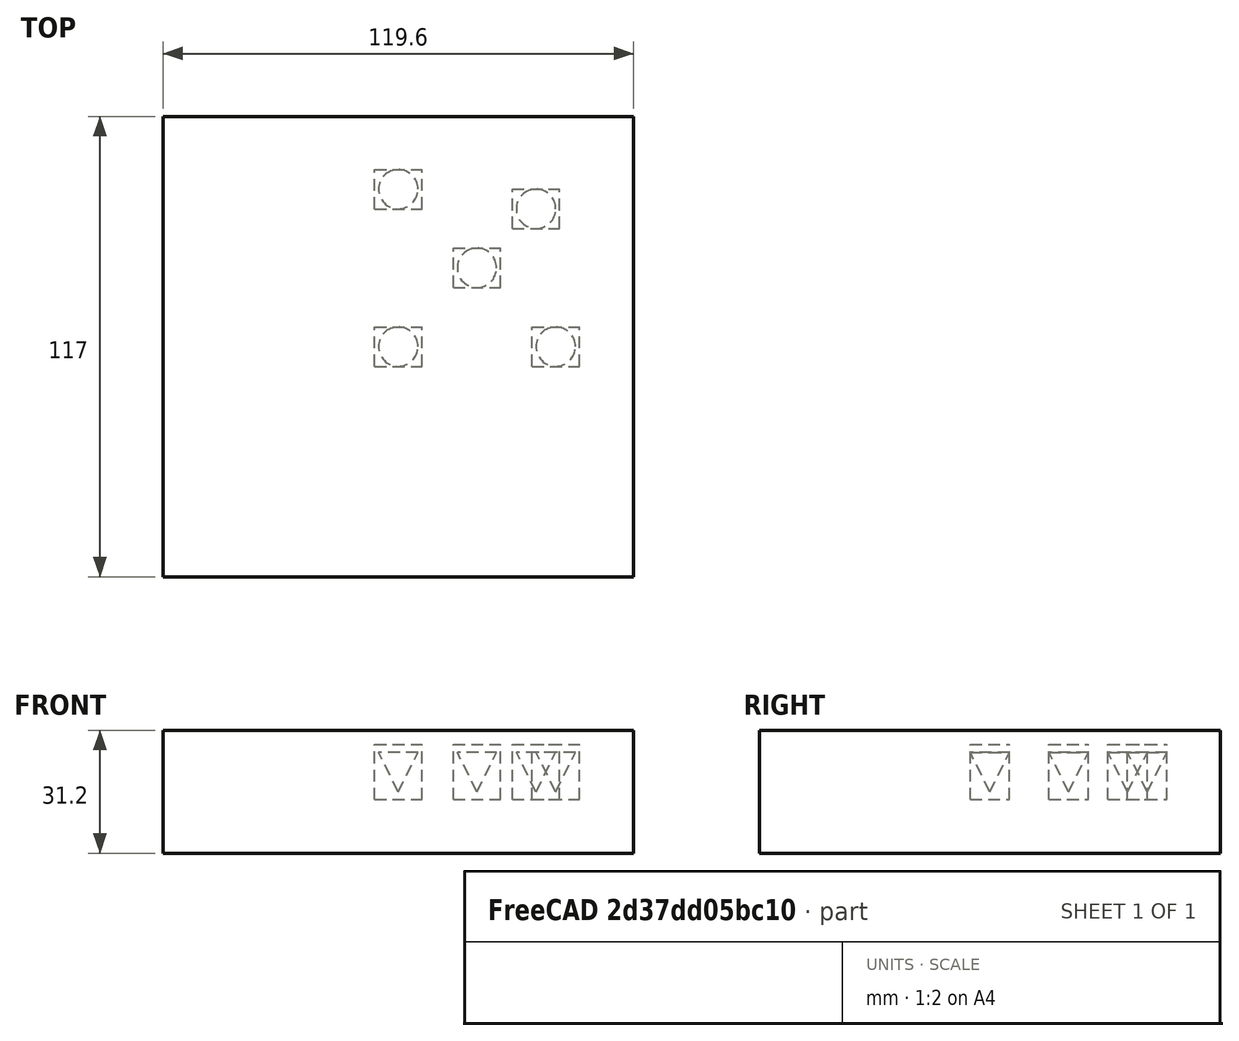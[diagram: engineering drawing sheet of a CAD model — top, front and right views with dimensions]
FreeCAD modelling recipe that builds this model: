
FCSTD DOCUMENT  (FreeCAD 0.21R33694 (Git))
Label: PointArray-of-part
License: All rights reserved
objects: App::DocumentObjectGroupPython×1251, Part::Vertex×5, App::Part×4, Part::FeaturePython×3, Part::Cone×2, Part::Compound×1
note: 11 computed .brp shape members not serialized (recipe doc carries the construction recipe); baked Part::Feature solids carry a one-line shape summary decoded from their .brp

FEATURE [App::DocumentObjectGroupPython] HALFPI  # scripted group (container) (typed FeaturePython)
  name = HALFPI
  value = pi/2.
FEATURE [App::DocumentObjectGroupPython] PI  # scripted group (container) (typed FeaturePython)
  name = PI
  value = 1.*pi
FEATURE [App::DocumentObjectGroupPython] TWOPI  # scripted group (container) (typed FeaturePython)
  name = TWOPI
  value = 2.*pi
FEATURE [App::DocumentObjectGroupPython] Constants  # scripted group (container) (typed FeaturePython)
  Group = -> [HALFPI,PI,TWOPI]
FEATURE [App::DocumentObjectGroupPython] Variables  # scripted group (container) (typed FeaturePython)
FEATURE [App::DocumentObjectGroupPython] Quantities  # scripted group (container) (typed FeaturePython)
FEATURE [App::DocumentObjectGroupPython] Isotopes  # scripted group (container) (typed FeaturePython)
FEATURE [App::DocumentObjectGroupPython] Elements  # scripted group (container) (typed FeaturePython)
FEATURE [App::DocumentObjectGroupPython] Matrix  # scripted group (container) (typed FeaturePython)
FEATURE [App::DocumentObjectGroupPython] Surfaces  # scripted group (container) (typed FeaturePython)
FEATURE [App::DocumentObjectGroupPython] Opticals  # scripted group (container) (typed FeaturePython)
  Group = -> [Matrix,Surfaces]
FEATURE [App::DocumentObjectGroupPython] G4Isotopes  # scripted group (container) (typed FeaturePython)
FEATURE [App::DocumentObjectGroupPython] H_element  # scripted group (container) (typed FeaturePython)
  Z = 1
  atom_value = 1.008
  formula = H
  name = H_element
FEATURE [App::DocumentObjectGroupPython] He_element  # scripted group (container) (typed FeaturePython)
  Z = 2
  atom_value = 4.0026
  formula = He
  name = He_element
FEATURE [App::DocumentObjectGroupPython] Li_element  # scripted group (container) (typed FeaturePython)
  Z = 3
  atom_value = 6.94
  formula = Li
  name = Li_element
FEATURE [App::DocumentObjectGroupPython] Be_element  # scripted group (container) (typed FeaturePython)
  Z = 4
  atom_value = 9.01218
  formula = Be
  name = Be_element
FEATURE [App::DocumentObjectGroupPython] B_element  # scripted group (container) (typed FeaturePython)
  Z = 5
  atom_value = 10.81
  formula = B
  name = B_element
FEATURE [App::DocumentObjectGroupPython] C_element  # scripted group (container) (typed FeaturePython)
  Z = 6
  atom_value = 12.011
  formula = C
  name = C_element
FEATURE [App::DocumentObjectGroupPython] N_element  # scripted group (container) (typed FeaturePython)
  Z = 7
  atom_value = 14.007
  formula = N
  name = N_element
FEATURE [App::DocumentObjectGroupPython] O_element  # scripted group (container) (typed FeaturePython)
  Z = 8
  atom_value = 15.999
  formula = O
  name = O_element
FEATURE [App::DocumentObjectGroupPython] F_element  # scripted group (container) (typed FeaturePython)
  Z = 9
  atom_value = 18.9984
  formula = F
  name = F_element
FEATURE [App::DocumentObjectGroupPython] Ne_element  # scripted group (container) (typed FeaturePython)
  Z = 10
  atom_value = 20.1797
  formula = Ne
  name = Ne_element
FEATURE [App::DocumentObjectGroupPython] Na_element  # scripted group (container) (typed FeaturePython)
  Z = 11
  atom_value = 22.9898
  formula = Na
  name = Na_element
FEATURE [App::DocumentObjectGroupPython] Mg_element  # scripted group (container) (typed FeaturePython)
  Z = 12
  atom_value = 24.305
  formula = Mg
  name = Mg_element
FEATURE [App::DocumentObjectGroupPython] Al_element  # scripted group (container) (typed FeaturePython)
  Z = 13
  atom_value = 26.9815
  formula = Al
  name = Al_element
FEATURE [App::DocumentObjectGroupPython] Si_element  # scripted group (container) (typed FeaturePython)
  Z = 14
  atom_value = 28.085
  formula = Si
  name = Si_element
FEATURE [App::DocumentObjectGroupPython] P_element  # scripted group (container) (typed FeaturePython)
  Z = 15
  atom_value = 30.9738
  formula = P
  name = P_element
FEATURE [App::DocumentObjectGroupPython] S_element  # scripted group (container) (typed FeaturePython)
  Z = 16
  atom_value = 32.06
  formula = S
  name = S_element
FEATURE [App::DocumentObjectGroupPython] Cl_element  # scripted group (container) (typed FeaturePython)
  Z = 17
  atom_value = 35.45
  formula = Cl
  name = Cl_element
FEATURE [App::DocumentObjectGroupPython] Ar_element  # scripted group (container) (typed FeaturePython)
  Z = 18
  atom_value = 39.95
  formula = Ar
  name = Ar_element
FEATURE [App::DocumentObjectGroupPython] K_element  # scripted group (container) (typed FeaturePython)
  Z = 19
  atom_value = 39.0983
  formula = K
  name = K_element
FEATURE [App::DocumentObjectGroupPython] Ca_element  # scripted group (container) (typed FeaturePython)
  Z = 20
  atom_value = 40.078
  formula = Ca
  name = Ca_element
FEATURE [App::DocumentObjectGroupPython] Sc_element  # scripted group (container) (typed FeaturePython)
  Z = 21
  atom_value = 44.9559
  formula = Sc
  name = Sc_element
FEATURE [App::DocumentObjectGroupPython] Ti_element  # scripted group (container) (typed FeaturePython)
  Z = 22
  atom_value = 47.867
  formula = Ti
  name = Ti_element
FEATURE [App::DocumentObjectGroupPython] V_element  # scripted group (container) (typed FeaturePython)
  Z = 23
  atom_value = 50.9415
  formula = V
  name = V_element
FEATURE [App::DocumentObjectGroupPython] Cr_element  # scripted group (container) (typed FeaturePython)
  Z = 24
  atom_value = 51.9961
  formula = Cr
  name = Cr_element
FEATURE [App::DocumentObjectGroupPython] Mn_element  # scripted group (container) (typed FeaturePython)
  Z = 25
  atom_value = 54.938
  formula = Mn
  name = Mn_element
FEATURE [App::DocumentObjectGroupPython] Fe_element  # scripted group (container) (typed FeaturePython)
  Z = 26
  atom_value = 55.845
  formula = Fe
  name = Fe_element
FEATURE [App::DocumentObjectGroupPython] Co_element  # scripted group (container) (typed FeaturePython)
  Z = 27
  atom_value = 58.9332
  formula = Co
  name = Co_element
FEATURE [App::DocumentObjectGroupPython] Ni_element  # scripted group (container) (typed FeaturePython)
  Z = 28
  atom_value = 58.6934
  formula = Ni
  name = Ni_element
FEATURE [App::DocumentObjectGroupPython] Cu_element  # scripted group (container) (typed FeaturePython)
  Z = 29
  atom_value = 63.546
  formula = Cu
  name = Cu_element
FEATURE [App::DocumentObjectGroupPython] Zn_element  # scripted group (container) (typed FeaturePython)
  Z = 30
  atom_value = 65.38
  formula = Zn
  name = Zn_element
FEATURE [App::DocumentObjectGroupPython] Ga_element  # scripted group (container) (typed FeaturePython)
  Z = 31
  atom_value = 69.723
  formula = Ga
  name = Ga_element
FEATURE [App::DocumentObjectGroupPython] Ge_element  # scripted group (container) (typed FeaturePython)
  Z = 32
  atom_value = 72.63
  formula = Ge
  name = Ge_element
FEATURE [App::DocumentObjectGroupPython] As_element  # scripted group (container) (typed FeaturePython)
  Z = 33
  atom_value = 74.9216
  formula = As
  name = As_element
FEATURE [App::DocumentObjectGroupPython] Se_element  # scripted group (container) (typed FeaturePython)
  Z = 34
  atom_value = 78.971
  formula = Se
  name = Se_element
FEATURE [App::DocumentObjectGroupPython] Br_element  # scripted group (container) (typed FeaturePython)
  Z = 35
  atom_value = 79.904
  formula = Br
  name = Br_element
FEATURE [App::DocumentObjectGroupPython] Kr_element  # scripted group (container) (typed FeaturePython)
  Z = 36
  atom_value = 83.798
  formula = Kr
  name = Kr_element
FEATURE [App::DocumentObjectGroupPython] Rb_element  # scripted group (container) (typed FeaturePython)
  Z = 37
  atom_value = 85.4678
  formula = Rb
  name = Rb_element
FEATURE [App::DocumentObjectGroupPython] Sr_element  # scripted group (container) (typed FeaturePython)
  Z = 38
  atom_value = 87.62
  formula = Sr
  name = Sr_element
FEATURE [App::DocumentObjectGroupPython] Y_element  # scripted group (container) (typed FeaturePython)
  Z = 39
  atom_value = 88.9058
  formula = Y
  name = Y_element
FEATURE [App::DocumentObjectGroupPython] Zr_element  # scripted group (container) (typed FeaturePython)
  Z = 40
  atom_value = 91.224
  formula = Zr
  name = Zr_element
FEATURE [App::DocumentObjectGroupPython] Nb_element  # scripted group (container) (typed FeaturePython)
  Z = 41
  atom_value = 92.9064
  formula = Nb
  name = Nb_element
FEATURE [App::DocumentObjectGroupPython] Mo_element  # scripted group (container) (typed FeaturePython)
  Z = 42
  atom_value = 95.95
  formula = Mo
  name = Mo_element
FEATURE [App::DocumentObjectGroupPython] Tc_element  # scripted group (container) (typed FeaturePython)
  Z = 43
  atom_value = 97
  formula = Tc
  name = Tc_element
FEATURE [App::DocumentObjectGroupPython] Ru_element  # scripted group (container) (typed FeaturePython)
  Z = 44
  atom_value = 101.07
  formula = Ru
  name = Ru_element
FEATURE [App::DocumentObjectGroupPython] Rh_element  # scripted group (container) (typed FeaturePython)
  Z = 45
  atom_value = 102.905
  formula = Rh
  name = Rh_element
FEATURE [App::DocumentObjectGroupPython] Pd_element  # scripted group (container) (typed FeaturePython)
  Z = 46
  atom_value = 106.42
  formula = Pd
  name = Pd_element
FEATURE [App::DocumentObjectGroupPython] Ag_element  # scripted group (container) (typed FeaturePython)
  Z = 47
  atom_value = 107.868
  formula = Ag
  name = Ag_element
FEATURE [App::DocumentObjectGroupPython] Cd_element  # scripted group (container) (typed FeaturePython)
  Z = 48
  atom_value = 112.414
  formula = Cd
  name = Cd_element
FEATURE [App::DocumentObjectGroupPython] In_element  # scripted group (container) (typed FeaturePython)
  Z = 49
  atom_value = 114.818
  formula = In
  name = In_element
FEATURE [App::DocumentObjectGroupPython] Sn_element  # scripted group (container) (typed FeaturePython)
  Z = 50
  atom_value = 118.71
  formula = Sn
  name = Sn_element
FEATURE [App::DocumentObjectGroupPython] Sb_element  # scripted group (container) (typed FeaturePython)
  Z = 51
  atom_value = 121.76
  formula = Sb
  name = Sb_element
FEATURE [App::DocumentObjectGroupPython] Te_element  # scripted group (container) (typed FeaturePython)
  Z = 52
  atom_value = 127.6
  formula = Te
  name = Te_element
FEATURE [App::DocumentObjectGroupPython] I_element  # scripted group (container) (typed FeaturePython)
  Z = 53
  atom_value = 126.904
  formula = I
  name = I_element
FEATURE [App::DocumentObjectGroupPython] Xe_element  # scripted group (container) (typed FeaturePython)
  Z = 54
  atom_value = 131.293
  formula = Xe
  name = Xe_element
FEATURE [App::DocumentObjectGroupPython] Cs_element  # scripted group (container) (typed FeaturePython)
  Z = 55
  atom_value = 132.905
  formula = Cs
  name = Cs_element
FEATURE [App::DocumentObjectGroupPython] Ba_element  # scripted group (container) (typed FeaturePython)
  Z = 56
  atom_value = 137.327
  formula = Ba
  name = Ba_element
FEATURE [App::DocumentObjectGroupPython] La_element  # scripted group (container) (typed FeaturePython)
  Z = 57
  atom_value = 138.905
  formula = La
  name = La_element
FEATURE [App::DocumentObjectGroupPython] Ce_element  # scripted group (container) (typed FeaturePython)
  Z = 58
  atom_value = 140.116
  formula = Ce
  name = Ce_element
FEATURE [App::DocumentObjectGroupPython] Pr_element  # scripted group (container) (typed FeaturePython)
  Z = 59
  atom_value = 140.908
  formula = Pr
  name = Pr_element
FEATURE [App::DocumentObjectGroupPython] Nd_element  # scripted group (container) (typed FeaturePython)
  Z = 60
  atom_value = 144.242
  formula = Nd
  name = Nd_element
FEATURE [App::DocumentObjectGroupPython] Pm_element  # scripted group (container) (typed FeaturePython)
  Z = 61
  atom_value = 145
  formula = Pm
  name = Pm_element
FEATURE [App::DocumentObjectGroupPython] Sm_element  # scripted group (container) (typed FeaturePython)
  Z = 62
  atom_value = 150.36
  formula = Sm
  name = Sm_element
FEATURE [App::DocumentObjectGroupPython] Eu_element  # scripted group (container) (typed FeaturePython)
  Z = 63
  atom_value = 151.964
  formula = Eu
  name = Eu_element
FEATURE [App::DocumentObjectGroupPython] Gd_element  # scripted group (container) (typed FeaturePython)
  Z = 64
  atom_value = 157.25
  formula = Gd
  name = Gd_element
FEATURE [App::DocumentObjectGroupPython] Tb_element  # scripted group (container) (typed FeaturePython)
  Z = 65
  atom_value = 158.925
  formula = Tb
  name = Tb_element
FEATURE [App::DocumentObjectGroupPython] Dy_element  # scripted group (container) (typed FeaturePython)
  Z = 66
  atom_value = 162.5
  formula = Dy
  name = Dy_element
FEATURE [App::DocumentObjectGroupPython] Ho_element  # scripted group (container) (typed FeaturePython)
  Z = 67
  atom_value = 164.93
  formula = Ho
  name = Ho_element
FEATURE [App::DocumentObjectGroupPython] Er_element  # scripted group (container) (typed FeaturePython)
  Z = 68
  atom_value = 167.259
  formula = Er
  name = Er_element
FEATURE [App::DocumentObjectGroupPython] Tm_element  # scripted group (container) (typed FeaturePython)
  Z = 69
  atom_value = 168.934
  formula = Tm
  name = Tm_element
FEATURE [App::DocumentObjectGroupPython] Yb_element  # scripted group (container) (typed FeaturePython)
  Z = 70
  atom_value = 173.045
  formula = Yb
  name = Yb_element
FEATURE [App::DocumentObjectGroupPython] Lu_element  # scripted group (container) (typed FeaturePython)
  Z = 71
  atom_value = 174.967
  formula = Lu
  name = Lu_element
FEATURE [App::DocumentObjectGroupPython] Hf_element  # scripted group (container) (typed FeaturePython)
  Z = 72
  atom_value = 178.49
  formula = Hf
  name = Hf_element
FEATURE [App::DocumentObjectGroupPython] Ta_element  # scripted group (container) (typed FeaturePython)
  Z = 73
  atom_value = 180.948
  formula = Ta
  name = Ta_element
FEATURE [App::DocumentObjectGroupPython] W_element  # scripted group (container) (typed FeaturePython)
  Z = 74
  atom_value = 183.84
  formula = W
  name = W_element
FEATURE [App::DocumentObjectGroupPython] Re_element  # scripted group (container) (typed FeaturePython)
  Z = 75
  atom_value = 186.207
  formula = Re
  name = Re_element
FEATURE [App::DocumentObjectGroupPython] Os_element  # scripted group (container) (typed FeaturePython)
  Z = 76
  atom_value = 190.23
  formula = Os
  name = Os_element
FEATURE [App::DocumentObjectGroupPython] Ir_element  # scripted group (container) (typed FeaturePython)
  Z = 77
  atom_value = 192.217
  formula = Ir
  name = Ir_element
FEATURE [App::DocumentObjectGroupPython] Pt_element  # scripted group (container) (typed FeaturePython)
  Z = 78
  atom_value = 195.084
  formula = Pt
  name = Pt_element
FEATURE [App::DocumentObjectGroupPython] Au_element  # scripted group (container) (typed FeaturePython)
  Z = 79
  atom_value = 196.967
  formula = Au
  name = Au_element
FEATURE [App::DocumentObjectGroupPython] Hg_element  # scripted group (container) (typed FeaturePython)
  Z = 80
  atom_value = 200.592
  formula = Hg
  name = Hg_element
FEATURE [App::DocumentObjectGroupPython] Tl_element  # scripted group (container) (typed FeaturePython)
  Z = 81
  atom_value = 204.38
  formula = Tl
  name = Tl_element
FEATURE [App::DocumentObjectGroupPython] Pb_element  # scripted group (container) (typed FeaturePython)
  Z = 82
  atom_value = 207.2
  formula = Pb
  name = Pb_element
FEATURE [App::DocumentObjectGroupPython] Bi_element  # scripted group (container) (typed FeaturePython)
  Z = 83
  atom_value = 208.98
  formula = Bi
  name = Bi_element
FEATURE [App::DocumentObjectGroupPython] Po_element  # scripted group (container) (typed FeaturePython)
  Z = 84
  atom_value = 209
  formula = Po
  name = Po_element
FEATURE [App::DocumentObjectGroupPython] At_element  # scripted group (container) (typed FeaturePython)
  Z = 85
  atom_value = 210
  formula = At
  name = At_element
FEATURE [App::DocumentObjectGroupPython] Rn_element  # scripted group (container) (typed FeaturePython)
  Z = 86
  atom_value = 222
  formula = Rn
  name = Rn_element
FEATURE [App::DocumentObjectGroupPython] Fr_element  # scripted group (container) (typed FeaturePython)
  Z = 87
  atom_value = 223
  formula = Fr
  name = Fr_element
FEATURE [App::DocumentObjectGroupPython] Ra_element  # scripted group (container) (typed FeaturePython)
  Z = 88
  atom_value = 226
  formula = Ra
  name = Ra_element
FEATURE [App::DocumentObjectGroupPython] Ac_element  # scripted group (container) (typed FeaturePython)
  Z = 89
  atom_value = 227
  formula = Ac
  name = Ac_element
FEATURE [App::DocumentObjectGroupPython] Th_element  # scripted group (container) (typed FeaturePython)
  Z = 90
  atom_value = 232.038
  formula = Th
  name = Th_element
FEATURE [App::DocumentObjectGroupPython] Pa_element  # scripted group (container) (typed FeaturePython)
  Z = 91
  atom_value = 231.036
  formula = Pa
  name = Pa_element
FEATURE [App::DocumentObjectGroupPython] U_element  # scripted group (container) (typed FeaturePython)
  Z = 92
  atom_value = 238.029
  formula = U
  name = U_element
FEATURE [App::DocumentObjectGroupPython] Np_element  # scripted group (container) (typed FeaturePython)
  Z = 93
  atom_value = 237
  formula = Np
  name = Np_element
FEATURE [App::DocumentObjectGroupPython] Pu_element  # scripted group (container) (typed FeaturePython)
  Z = 94
  atom_value = 244
  formula = Pu
  name = Pu_element
FEATURE [App::DocumentObjectGroupPython] Am_element  # scripted group (container) (typed FeaturePython)
  Z = 95
  atom_value = 243
  formula = Am
  name = Am_element
FEATURE [App::DocumentObjectGroupPython] Cm_element  # scripted group (container) (typed FeaturePython)
  Z = 96
  atom_value = 247
  formula = Cm
  name = Cm_element
FEATURE [App::DocumentObjectGroupPython] Bk_element  # scripted group (container) (typed FeaturePython)
  Z = 97
  atom_value = 247
  formula = Bk
  name = Bk_element
FEATURE [App::DocumentObjectGroupPython] Cf_element  # scripted group (container) (typed FeaturePython)
  Z = 98
  atom_value = 251
  formula = Cf
  name = Cf_element
FEATURE [App::DocumentObjectGroupPython] G4Elements  # scripted group (container) (typed FeaturePython)
  Group = -> [H_element,He_element,Li_element,Be_element,B_element,C_element,N_element,O_element,F_element,Ne_element,Na_element,Mg_element,Al_element,Si_element,P_element,S_element,Cl_element,Ar_element,K_element,Ca_element,Sc_element,Ti_element,V_element,Cr_element,Mn_element,Fe_element,Co_element,Ni_element,Cu_element,Zn_element,Ga_element,Ge_element,As_element,Se_element,Br_element,Kr_element,Rb_element,+61 more]
FEATURE [App::DocumentObjectGroupPython] H_element001  label="H_element : 0.101"  # scripted group (container) (typed FeaturePython)
  n = 0.101327
FEATURE [App::DocumentObjectGroupPython] C_element001  label="C_element : 0.775"  # scripted group (container) (typed FeaturePython)
  n = 0.7755
FEATURE [App::DocumentObjectGroupPython] N_element001  label="N_element : 0.035"  # scripted group (container) (typed FeaturePython)
  n = 0.035057
FEATURE [App::DocumentObjectGroupPython] O_element001  label="O_element : 0.052"  # scripted group (container) (typed FeaturePython)
  n = 0.0523159
FEATURE [App::DocumentObjectGroupPython] F_element001  label="F_element : 0.017"  # scripted group (container) (typed FeaturePython)
  n = 0.017422
FEATURE [App::DocumentObjectGroupPython] Ca_element001  label="Ca_element : 0.018"  # scripted group (container) (typed FeaturePython)
  n = 0.018378
FEATURE [App::DocumentObjectGroupPython] G4_A_150_TISSUE  label="G4_A-150_TISSUE"  # scripted group (container) (typed FeaturePython)
  Dunit = g/cm3
  Dvalue = 1.127
  Group = -> [H_element001,C_element001,N_element001,O_element001,F_element001,Ca_element001]
  conduct = 2
  density = 1
  expand = 3
  formula = G4_A-150_TISSUE
  name = G4_A-150_TISSUE
  specific = 4
FEATURE [App::DocumentObjectGroupPython] C_element002  label="C_element : 3"  # scripted group (container) (typed FeaturePython)
  n = 3
  ref = C_element
FEATURE [App::DocumentObjectGroupPython] H_element002  label="H_element : 6"  # scripted group (container) (typed FeaturePython)
  n = 6
  ref = H_element
FEATURE [App::DocumentObjectGroupPython] O_element002  label="O_element : 1"  # scripted group (container) (typed FeaturePython)
  n = 1
  ref = O_element
FEATURE [App::DocumentObjectGroupPython] G4_ACETONE  # scripted group (container) (typed FeaturePython)
  Dunit = g/cm3
  Dvalue = 0.7899
  Group = -> [C_element002,H_element002,O_element002]
  conduct = 2
  density = 1
  expand = 3
  formula = G4_ACETONE
  name = G4_ACETONE
  specific = 4
FEATURE [App::DocumentObjectGroupPython] C_element003  label="C_element : 2"  # scripted group (container) (typed FeaturePython)
  n = 2
  ref = C_element
FEATURE [App::DocumentObjectGroupPython] H_element003  label="H_element : 2"  # scripted group (container) (typed FeaturePython)
  n = 2
  ref = H_element
FEATURE [App::DocumentObjectGroupPython] G4_ACETYLENE  # scripted group (container) (typed FeaturePython)
  Dunit = g/cm3
  Dvalue = 0.0010967
  Group = -> [C_element003,H_element003]
  conduct = 2
  density = 1
  expand = 3
  formula = G4_ACETYLENE
  name = G4_ACETYLENE
  specific = 4
FEATURE [App::DocumentObjectGroupPython] C_element004  label="C_element : 5"  # scripted group (container) (typed FeaturePython)
  n = 5
  ref = C_element
FEATURE [App::DocumentObjectGroupPython] H_element004  label="H_element : 5"  # scripted group (container) (typed FeaturePython)
  n = 5
  ref = H_element
FEATURE [App::DocumentObjectGroupPython] N_element002  label="N_element : 5"  # scripted group (container) (typed FeaturePython)
  n = 5
  ref = N_element
FEATURE [App::DocumentObjectGroupPython] G4_ADENINE  # scripted group (container) (typed FeaturePython)
  Dunit = g/cm3
  Dvalue = 1.6
  Group = -> [C_element004,H_element004,N_element002]
  conduct = 2
  density = 1
  expand = 3
  formula = G4_ADENINE
  name = G4_ADENINE
  specific = 4
FEATURE [App::DocumentObjectGroupPython] H_element005  label="H_element : 0.114"  # scripted group (container) (typed FeaturePython)
  n = 0.114
FEATURE [App::DocumentObjectGroupPython] C_element005  label="C_element : 0.598"  # scripted group (container) (typed FeaturePython)
  n = 0.598
FEATURE [App::DocumentObjectGroupPython] N_element003  label="N_element : 0.007"  # scripted group (container) (typed FeaturePython)
  n = 0.007
FEATURE [App::DocumentObjectGroupPython] O_element003  label="O_element : 0.278"  # scripted group (container) (typed FeaturePython)
  n = 0.278
FEATURE [App::DocumentObjectGroupPython] Na_element001  label="Na_element : 0.001"  # scripted group (container) (typed FeaturePython)
  n = 0.001
FEATURE [App::DocumentObjectGroupPython] S_element001  label="S_element : 0.001"  # scripted group (container) (typed FeaturePython)
  n = 0.001
FEATURE [App::DocumentObjectGroupPython] Cl_element001  label="Cl_element : 0.001"  # scripted group (container) (typed FeaturePython)
  n = 0.001
FEATURE [App::DocumentObjectGroupPython] G4_ADIPOSE_TISSUE_ICRP  # scripted group (container) (typed FeaturePython)
  Dunit = g/cm3
  Dvalue = 0.95
  Group = -> [H_element005,C_element005,N_element003,O_element003,Na_element001,S_element001,Cl_element001]
  conduct = 2
  density = 1
  expand = 3
  formula = G4_ADIPOSE_TISSUE_ICRP
  name = G4_ADIPOSE_TISSUE_ICRP
  specific = 4
FEATURE [App::DocumentObjectGroupPython] C_element006  label="C_element : 0.000"  # scripted group (container) (typed FeaturePython)
  n = 0.000124
FEATURE [App::DocumentObjectGroupPython] N_element004  label="N_element : 0.755"  # scripted group (container) (typed FeaturePython)
  n = 0.755268
FEATURE [App::DocumentObjectGroupPython] O_element004  label="O_element : 0.232"  # scripted group (container) (typed FeaturePython)
  n = 0.231781
FEATURE [App::DocumentObjectGroupPython] Ar_element001  label="Ar_element : 0.013"  # scripted group (container) (typed FeaturePython)
  n = 0.012827
FEATURE [App::DocumentObjectGroupPython] G4_AIR  # scripted group (container) (typed FeaturePython)
  Dunit = g/cm3
  Dvalue = 0.00120479
  Group = -> [C_element006,N_element004,O_element004,Ar_element001]
  conduct = 2
  density = 1
  expand = 3
  formula = G4_AIR
  name = G4_AIR
  specific = 4
FEATURE [App::DocumentObjectGroupPython] C_element007  label="C_element : 006"  # scripted group (container) (typed FeaturePython)
  n = 3
  ref = C_element
FEATURE [App::DocumentObjectGroupPython] H_element006  label="H_element : 7"  # scripted group (container) (typed FeaturePython)
  n = 7
  ref = H_element
FEATURE [App::DocumentObjectGroupPython] N_element005  label="N_element : 1"  # scripted group (container) (typed FeaturePython)
  n = 1
  ref = N_element
FEATURE [App::DocumentObjectGroupPython] O_element005  label="O_element : 2"  # scripted group (container) (typed FeaturePython)
  n = 2
  ref = O_element
FEATURE [App::DocumentObjectGroupPython] G4_ALANINE  # scripted group (container) (typed FeaturePython)
  Dunit = g/cm3
  Dvalue = 1.42
  Group = -> [C_element007,H_element006,N_element005,O_element005]
  conduct = 2
  density = 1
  expand = 3
  formula = G4_ALANINE
  name = G4_ALANINE
  specific = 4
FEATURE [App::DocumentObjectGroupPython] Al_element001  label="Al_element : 2"  # scripted group (container) (typed FeaturePython)
  n = 2
  ref = Al_element
FEATURE [App::DocumentObjectGroupPython] O_element006  label="O_element : 3"  # scripted group (container) (typed FeaturePython)
  n = 3
  ref = O_element
FEATURE [App::DocumentObjectGroupPython] G4_ALUMINUM_OXIDE  # scripted group (container) (typed FeaturePython)
  Dunit = g/cm3
  Dvalue = 3.97
  Group = -> [Al_element001,O_element006]
  conduct = 2
  density = 1
  expand = 3
  formula = G4_ALUMINUM_OXIDE
  name = G4_ALUMINUM_OXIDE
  specific = 4
FEATURE [App::DocumentObjectGroupPython] H_element007  label="H_element : 0.106"  # scripted group (container) (typed FeaturePython)
  n = 0.10593
FEATURE [App::DocumentObjectGroupPython] C_element008  label="C_element : 0.789"  # scripted group (container) (typed FeaturePython)
  n = 0.788974
FEATURE [App::DocumentObjectGroupPython] O_element007  label="O_element : 0.105"  # scripted group (container) (typed FeaturePython)
  n = 0.105096
FEATURE [App::DocumentObjectGroupPython] G4_AMBER  # scripted group (container) (typed FeaturePython)
  Dunit = g/cm3
  Dvalue = 1.1
  Group = -> [H_element007,C_element008,O_element007]
  conduct = 2
  density = 1
  expand = 3
  formula = G4_AMBER
  name = G4_AMBER
  specific = 4
FEATURE [App::DocumentObjectGroupPython] N_element006  label="N_element : 006"  # scripted group (container) (typed FeaturePython)
  n = 1
  ref = N_element
FEATURE [App::DocumentObjectGroupPython] H_element008  label="H_element : 3"  # scripted group (container) (typed FeaturePython)
  n = 3
  ref = H_element
FEATURE [App::DocumentObjectGroupPython] G4_AMMONIA  # scripted group (container) (typed FeaturePython)
  Dunit = g/cm3
  Dvalue = 0.000826019
  Group = -> [N_element006,H_element008]
  conduct = 2
  density = 1
  expand = 3
  formula = G4_AMMONIA
  name = G4_AMMONIA
  specific = 4
FEATURE [App::DocumentObjectGroupPython] C_element009  label="C_element : 6"  # scripted group (container) (typed FeaturePython)
  n = 6
  ref = C_element
FEATURE [App::DocumentObjectGroupPython] H_element009  label="H_element : 008"  # scripted group (container) (typed FeaturePython)
  n = 7
  ref = H_element
FEATURE [App::DocumentObjectGroupPython] N_element007  label="N_element : 007"  # scripted group (container) (typed FeaturePython)
  n = 1
  ref = N_element
FEATURE [App::DocumentObjectGroupPython] G4_ANILINE  # scripted group (container) (typed FeaturePython)
  Dunit = g/cm3
  Dvalue = 1.0235
  Group = -> [C_element009,H_element009,N_element007]
  conduct = 2
  density = 1
  expand = 3
  formula = G4_ANILINE
  name = G4_ANILINE
  specific = 4
FEATURE [App::DocumentObjectGroupPython] C_element010  label="C_element : 14"  # scripted group (container) (typed FeaturePython)
  n = 14
  ref = C_element
FEATURE [App::DocumentObjectGroupPython] H_element010  label="H_element : 10"  # scripted group (container) (typed FeaturePython)
  n = 10
  ref = H_element
FEATURE [App::DocumentObjectGroupPython] G4_ANTHRACENE  # scripted group (container) (typed FeaturePython)
  Dunit = g/cm3
  Dvalue = 1.283
  Group = -> [C_element010,H_element010]
  conduct = 2
  density = 1
  expand = 3
  formula = G4_ANTHRACENE
  name = G4_ANTHRACENE
  specific = 4
FEATURE [App::DocumentObjectGroupPython] H_element011  label="H_element : 0.065"  # scripted group (container) (typed FeaturePython)
  n = 0.0654709
FEATURE [App::DocumentObjectGroupPython] C_element011  label="C_element : 0.537"  # scripted group (container) (typed FeaturePython)
  n = 0.536944
FEATURE [App::DocumentObjectGroupPython] N_element008  label="N_element : 0.021"  # scripted group (container) (typed FeaturePython)
  n = 0.0215
FEATURE [App::DocumentObjectGroupPython] O_element008  label="O_element : 0.032"  # scripted group (container) (typed FeaturePython)
  n = 0.032085
FEATURE [App::DocumentObjectGroupPython] F_element002  label="F_element : 0.167"  # scripted group (container) (typed FeaturePython)
  n = 0.167411
FEATURE [App::DocumentObjectGroupPython] Ca_element002  label="Ca_element : 0.177"  # scripted group (container) (typed FeaturePython)
  n = 0.176589
FEATURE [App::DocumentObjectGroupPython] G4_B_100_BONE  label="G4_B-100_BONE"  # scripted group (container) (typed FeaturePython)
  Dunit = g/cm3
  Dvalue = 1.45
  Group = -> [H_element011,C_element011,N_element008,O_element008,F_element002,Ca_element002]
  conduct = 2
  density = 1
  expand = 3
  formula = G4_B-100_BONE
  name = G4_B-100_BONE
  specific = 4
FEATURE [App::DocumentObjectGroupPython] H_element012  label="H_element : 0.057"  # scripted group (container) (typed FeaturePython)
  n = 0.057441
FEATURE [App::DocumentObjectGroupPython] C_element012  label="C_element : 0.790"  # scripted group (container) (typed FeaturePython)
  n = 0.774591
FEATURE [App::DocumentObjectGroupPython] O_element009  label="O_element : 0.168"  # scripted group (container) (typed FeaturePython)
  n = 0.167968
FEATURE [App::DocumentObjectGroupPython] G4_BAKELITE  # scripted group (container) (typed FeaturePython)
  Dunit = g/cm3
  Dvalue = 1.25
  Group = -> [H_element012,C_element012,O_element009]
  conduct = 2
  density = 1
  expand = 3
  formula = G4_BAKELITE
  name = G4_BAKELITE
  specific = 4
FEATURE [App::DocumentObjectGroupPython] Ba_element001  label="Ba_element : 1"  # scripted group (container) (typed FeaturePython)
  n = 1
  ref = Ba_element
FEATURE [App::DocumentObjectGroupPython] F_element003  label="F_element : 2"  # scripted group (container) (typed FeaturePython)
  n = 2
  ref = F_element
FEATURE [App::DocumentObjectGroupPython] G4_BARIUM_FLUORIDE  # scripted group (container) (typed FeaturePython)
  Dunit = g/cm3
  Dvalue = 4.89
  Group = -> [Ba_element001,F_element003]
  conduct = 2
  density = 1
  expand = 3
  formula = G4_BARIUM_FLUORIDE
  name = G4_BARIUM_FLUORIDE
  specific = 4
FEATURE [App::DocumentObjectGroupPython] Ba_element002  label="Ba_element : 002"  # scripted group (container) (typed FeaturePython)
  n = 1
  ref = Ba_element
FEATURE [App::DocumentObjectGroupPython] S_element002  label="S_element : 1"  # scripted group (container) (typed FeaturePython)
  n = 1
  ref = S_element
FEATURE [App::DocumentObjectGroupPython] O_element010  label="O_element : 4"  # scripted group (container) (typed FeaturePython)
  n = 4
  ref = O_element
FEATURE [App::DocumentObjectGroupPython] G4_BARIUM_SULFATE  # scripted group (container) (typed FeaturePython)
  Dunit = g/cm3
  Dvalue = 4.5
  Group = -> [Ba_element002,S_element002,O_element010]
  conduct = 2
  density = 1
  expand = 3
  formula = G4_BARIUM_SULFATE
  name = G4_BARIUM_SULFATE
  specific = 4
FEATURE [App::DocumentObjectGroupPython] C_element013  label="C_element : 007"  # scripted group (container) (typed FeaturePython)
  n = 6
  ref = C_element
FEATURE [App::DocumentObjectGroupPython] H_element013  label="H_element : 009"  # scripted group (container) (typed FeaturePython)
  n = 6
  ref = H_element
FEATURE [App::DocumentObjectGroupPython] G4_BENZENE  # scripted group (container) (typed FeaturePython)
  Dunit = g/cm3
  Dvalue = 0.87865
  Group = -> [C_element013,H_element013]
  conduct = 2
  density = 1
  expand = 3
  formula = G4_BENZENE
  name = G4_BENZENE
  specific = 4
FEATURE [App::DocumentObjectGroupPython] Be_element001  label="Be_element : 1"  # scripted group (container) (typed FeaturePython)
  n = 1
  ref = Be_element
FEATURE [App::DocumentObjectGroupPython] O_element011  label="O_element : 005"  # scripted group (container) (typed FeaturePython)
  n = 1
  ref = O_element
FEATURE [App::DocumentObjectGroupPython] G4_BERYLLIUM_OXIDE  # scripted group (container) (typed FeaturePython)
  Dunit = g/cm3
  Dvalue = 3.01
  Group = -> [Be_element001,O_element011]
  conduct = 2
  density = 1
  expand = 3
  formula = G4_BERYLLIUM_OXIDE
  name = G4_BERYLLIUM_OXIDE
  specific = 4
FEATURE [App::DocumentObjectGroupPython] Bi_element001  label="Bi_element : 4"  # scripted group (container) (typed FeaturePython)
  n = 4
  ref = Bi_element
FEATURE [App::DocumentObjectGroupPython] Ge_element001  label="Ge_element : 3"  # scripted group (container) (typed FeaturePython)
  n = 3
  ref = Ge_element
FEATURE [App::DocumentObjectGroupPython] O_element012  label="O_element : 12"  # scripted group (container) (typed FeaturePython)
  n = 12
  ref = O_element
FEATURE [App::DocumentObjectGroupPython] G4_BGO  # scripted group (container) (typed FeaturePython)
  Dunit = g/cm3
  Dvalue = 7.13
  Group = -> [Bi_element001,Ge_element001,O_element012]
  conduct = 2
  density = 1
  expand = 3
  formula = G4_BGO
  name = G4_BGO
  specific = 4
FEATURE [App::DocumentObjectGroupPython] H_element014  label="H_element : 0.102"  # scripted group (container) (typed FeaturePython)
  n = 0.102
FEATURE [App::DocumentObjectGroupPython] C_element014  label="C_element : 0.110"  # scripted group (container) (typed FeaturePython)
  n = 0.11
FEATURE [App::DocumentObjectGroupPython] N_element009  label="N_element : 0.033"  # scripted group (container) (typed FeaturePython)
  n = 0.033
FEATURE [App::DocumentObjectGroupPython] O_element013  label="O_element : 0.745"  # scripted group (container) (typed FeaturePython)
  n = 0.745
FEATURE [App::DocumentObjectGroupPython] Na_element002  label="Na_element : 0.002"  # scripted group (container) (typed FeaturePython)
  n = 0.001
FEATURE [App::DocumentObjectGroupPython] P_element001  label="P_element : 0.001"  # scripted group (container) (typed FeaturePython)
  n = 0.001
FEATURE [App::DocumentObjectGroupPython] S_element003  label="S_element : 0.002"  # scripted group (container) (typed FeaturePython)
  n = 0.002
FEATURE [App::DocumentObjectGroupPython] Cl_element002  label="Cl_element : 0.003"  # scripted group (container) (typed FeaturePython)
  n = 0.003
FEATURE [App::DocumentObjectGroupPython] K_element001  label="K_element : 0.002"  # scripted group (container) (typed FeaturePython)
  n = 0.002
FEATURE [App::DocumentObjectGroupPython] Fe_element001  label="Fe_element : 0.001"  # scripted group (container) (typed FeaturePython)
  n = 0.001
FEATURE [App::DocumentObjectGroupPython] G4_BLOOD_ICRP  # scripted group (container) (typed FeaturePython)
  Dunit = g/cm3
  Dvalue = 1.06
  Group = -> [H_element014,C_element014,N_element009,O_element013,Na_element002,P_element001,S_element003,Cl_element002,K_element001,Fe_element001]
  conduct = 2
  density = 1
  expand = 3
  formula = G4_BLOOD_ICRP
  name = G4_BLOOD_ICRP
  specific = 4
FEATURE [App::DocumentObjectGroupPython] H_element015  label="H_element : 0.064"  # scripted group (container) (typed FeaturePython)
  n = 0.064
FEATURE [App::DocumentObjectGroupPython] C_element015  label="C_element : 0.278"  # scripted group (container) (typed FeaturePython)
  n = 0.278
FEATURE [App::DocumentObjectGroupPython] N_element010  label="N_element : 0.027"  # scripted group (container) (typed FeaturePython)
  n = 0.027
FEATURE [App::DocumentObjectGroupPython] O_element014  label="O_element : 0.410"  # scripted group (container) (typed FeaturePython)
  n = 0.41
FEATURE [App::DocumentObjectGroupPython] Mg_element001  label="Mg_element : 0.002"  # scripted group (container) (typed FeaturePython)
  n = 0.002
FEATURE [App::DocumentObjectGroupPython] P_element002  label="P_element : 0.070"  # scripted group (container) (typed FeaturePython)
  n = 0.07
FEATURE [App::DocumentObjectGroupPython] S_element004  label="S_element : 0.003"  # scripted group (container) (typed FeaturePython)
  n = 0.002
FEATURE [App::DocumentObjectGroupPython] Ca_element003  label="Ca_element : 0.147"  # scripted group (container) (typed FeaturePython)
  n = 0.147
FEATURE [App::DocumentObjectGroupPython] G4_BONE_COMPACT_ICRU  # scripted group (container) (typed FeaturePython)
  Dunit = g/cm3
  Dvalue = 1.85
  Group = -> [H_element015,C_element015,N_element010,O_element014,Mg_element001,P_element002,S_element004,Ca_element003]
  conduct = 2
  density = 1
  expand = 3
  formula = G4_BONE_COMPACT_ICRU
  name = G4_BONE_COMPACT_ICRU
  specific = 4
FEATURE [App::DocumentObjectGroupPython] H_element016  label="H_element : 0.034"  # scripted group (container) (typed FeaturePython)
  n = 0.034
FEATURE [App::DocumentObjectGroupPython] C_element016  label="C_element : 0.155"  # scripted group (container) (typed FeaturePython)
  n = 0.155
FEATURE [App::DocumentObjectGroupPython] N_element011  label="N_element : 0.042"  # scripted group (container) (typed FeaturePython)
  n = 0.042
FEATURE [App::DocumentObjectGroupPython] O_element015  label="O_element : 0.435"  # scripted group (container) (typed FeaturePython)
  n = 0.435
FEATURE [App::DocumentObjectGroupPython] Na_element003  label="Na_element : 0.003"  # scripted group (container) (typed FeaturePython)
  n = 0.001
FEATURE [App::DocumentObjectGroupPython] Mg_element002  label="Mg_element : 0.003"  # scripted group (container) (typed FeaturePython)
  n = 0.002
FEATURE [App::DocumentObjectGroupPython] P_element003  label="P_element : 0.103"  # scripted group (container) (typed FeaturePython)
  n = 0.103
FEATURE [App::DocumentObjectGroupPython] S_element005  label="S_element : 0.004"  # scripted group (container) (typed FeaturePython)
  n = 0.003
FEATURE [App::DocumentObjectGroupPython] Ca_element004  label="Ca_element : 0.225"  # scripted group (container) (typed FeaturePython)
  n = 0.225
FEATURE [App::DocumentObjectGroupPython] G4_BONE_CORTICAL_ICRP  # scripted group (container) (typed FeaturePython)
  Dunit = g/cm3
  Dvalue = 1.92
  Group = -> [H_element016,C_element016,N_element011,O_element015,Na_element003,Mg_element002,P_element003,S_element005,Ca_element004]
  conduct = 2
  density = 1
  expand = 3
  formula = G4_BONE_CORTICAL_ICRP
  name = G4_BONE_CORTICAL_ICRP
  specific = 4
FEATURE [App::DocumentObjectGroupPython] B_element001  label="B_element : 4"  # scripted group (container) (typed FeaturePython)
  n = 4
  ref = B_element
FEATURE [App::DocumentObjectGroupPython] C_element017  label="C_element : 1"  # scripted group (container) (typed FeaturePython)
  n = 1
  ref = C_element
FEATURE [App::DocumentObjectGroupPython] G4_BORON_CARBIDE  # scripted group (container) (typed FeaturePython)
  Dunit = g/cm3
  Dvalue = 2.52
  Group = -> [B_element001,C_element017]
  conduct = 2
  density = 1
  expand = 3
  formula = G4_BORON_CARBIDE
  name = G4_BORON_CARBIDE
  specific = 4
FEATURE [App::DocumentObjectGroupPython] B_element002  label="B_element : 2"  # scripted group (container) (typed FeaturePython)
  n = 2
  ref = B_element
FEATURE [App::DocumentObjectGroupPython] O_element016  label="O_element : 006"  # scripted group (container) (typed FeaturePython)
  n = 3
  ref = O_element
FEATURE [App::DocumentObjectGroupPython] G4_BORON_OXIDE  # scripted group (container) (typed FeaturePython)
  Dunit = g/cm3
  Dvalue = 1.812
  Group = -> [B_element002,O_element016]
  conduct = 2
  density = 1
  expand = 3
  formula = G4_BORON_OXIDE
  name = G4_BORON_OXIDE
  specific = 4
FEATURE [App::DocumentObjectGroupPython] H_element017  label="H_element : 0.107"  # scripted group (container) (typed FeaturePython)
  n = 0.107
FEATURE [App::DocumentObjectGroupPython] C_element018  label="C_element : 0.145"  # scripted group (container) (typed FeaturePython)
  n = 0.145
FEATURE [App::DocumentObjectGroupPython] N_element012  label="N_element : 0.022"  # scripted group (container) (typed FeaturePython)
  n = 0.022
FEATURE [App::DocumentObjectGroupPython] O_element017  label="O_element : 0.712"  # scripted group (container) (typed FeaturePython)
  n = 0.712
FEATURE [App::DocumentObjectGroupPython] Na_element004  label="Na_element : 0.004"  # scripted group (container) (typed FeaturePython)
  n = 0.002
FEATURE [App::DocumentObjectGroupPython] P_element004  label="P_element : 0.004"  # scripted group (container) (typed FeaturePython)
  n = 0.004
FEATURE [App::DocumentObjectGroupPython] S_element006  label="S_element : 0.005"  # scripted group (container) (typed FeaturePython)
  n = 0.002
FEATURE [App::DocumentObjectGroupPython] Cl_element003  label="Cl_element : 0.004"  # scripted group (container) (typed FeaturePython)
  n = 0.003
FEATURE [App::DocumentObjectGroupPython] K_element002  label="K_element : 0.003"  # scripted group (container) (typed FeaturePython)
  n = 0.003
FEATURE [App::DocumentObjectGroupPython] G4_BRAIN_ICRP  # scripted group (container) (typed FeaturePython)
  Dunit = g/cm3
  Dvalue = 1.04
  Group = -> [H_element017,C_element018,N_element012,O_element017,Na_element004,P_element004,S_element006,Cl_element003,K_element002]
  conduct = 2
  density = 1
  expand = 3
  formula = G4_BRAIN_ICRP
  name = G4_BRAIN_ICRP
  specific = 4
FEATURE [App::DocumentObjectGroupPython] C_element019  label="C_element : 4"  # scripted group (container) (typed FeaturePython)
  n = 4
  ref = C_element
FEATURE [App::DocumentObjectGroupPython] H_element018  label="H_element : 010"  # scripted group (container) (typed FeaturePython)
  n = 10
  ref = H_element
FEATURE [App::DocumentObjectGroupPython] G4_BUTANE  # scripted group (container) (typed FeaturePython)
  Dunit = g/cm3
  Dvalue = 0.00249343
  Group = -> [C_element019,H_element018]
  conduct = 2
  density = 1
  expand = 3
  formula = G4_BUTANE
  name = G4_BUTANE
  specific = 4
FEATURE [App::DocumentObjectGroupPython] C_element020  label="C_element : 008"  # scripted group (container) (typed FeaturePython)
  n = 4
  ref = C_element
FEATURE [App::DocumentObjectGroupPython] H_element019  label="H_element : 011"  # scripted group (container) (typed FeaturePython)
  n = 10
  ref = H_element
FEATURE [App::DocumentObjectGroupPython] O_element018  label="O_element : 007"  # scripted group (container) (typed FeaturePython)
  n = 1
  ref = O_element
FEATURE [App::DocumentObjectGroupPython] G4_N_BUTYL_ALCOHOL  label="G4_N-BUTYL_ALCOHOL"  # scripted group (container) (typed FeaturePython)
  Dunit = g/cm3
  Dvalue = 0.8098
  Group = -> [C_element020,H_element019,O_element018]
  conduct = 2
  density = 1
  expand = 3
  formula = G4_N-BUTYL_ALCOHOL
  name = G4_N-BUTYL_ALCOHOL
  specific = 4
FEATURE [App::DocumentObjectGroupPython] H_element020  label="H_element : 0.025"  # scripted group (container) (typed FeaturePython)
  n = 0.02468
FEATURE [App::DocumentObjectGroupPython] C_element021  label="C_element : 0.502"  # scripted group (container) (typed FeaturePython)
  n = 0.501611
FEATURE [App::DocumentObjectGroupPython] O_element019  label="O_element : 0.005"  # scripted group (container) (typed FeaturePython)
  n = 0.004527
FEATURE [App::DocumentObjectGroupPython] F_element004  label="F_element : 0.465"  # scripted group (container) (typed FeaturePython)
  n = 0.465209
FEATURE [App::DocumentObjectGroupPython] Si_element001  label="Si_element : 0.004"  # scripted group (container) (typed FeaturePython)
  n = 0.003973
FEATURE [App::DocumentObjectGroupPython] G4_C_552  label="G4_C-552"  # scripted group (container) (typed FeaturePython)
  Dunit = g/cm3
  Dvalue = 1.76
  Group = -> [H_element020,C_element021,O_element019,F_element004,Si_element001]
  conduct = 2
  density = 1
  expand = 3
  formula = G4_C-552
  name = G4_C-552
  specific = 4
FEATURE [App::DocumentObjectGroupPython] Cd_element001  label="Cd_element : 1"  # scripted group (container) (typed FeaturePython)
  n = 1
  ref = Cd_element
FEATURE [App::DocumentObjectGroupPython] Te_element001  label="Te_element : 1"  # scripted group (container) (typed FeaturePython)
  n = 1
  ref = Te_element
FEATURE [App::DocumentObjectGroupPython] G4_CADMIUM_TELLURIDE  # scripted group (container) (typed FeaturePython)
  Dunit = g/cm3
  Dvalue = 6.2
  Group = -> [Cd_element001,Te_element001]
  conduct = 2
  density = 1
  expand = 3
  formula = G4_CADMIUM_TELLURIDE
  name = G4_CADMIUM_TELLURIDE
  specific = 4
FEATURE [App::DocumentObjectGroupPython] Cd_element002  label="Cd_element : 002"  # scripted group (container) (typed FeaturePython)
  n = 1
  ref = Cd_element
FEATURE [App::DocumentObjectGroupPython] W_element001  label="W_element : 1"  # scripted group (container) (typed FeaturePython)
  n = 1
  ref = W_element
FEATURE [App::DocumentObjectGroupPython] O_element020  label="O_element : 008"  # scripted group (container) (typed FeaturePython)
  n = 4
  ref = O_element
FEATURE [App::DocumentObjectGroupPython] G4_CADMIUM_TUNGSTATE  # scripted group (container) (typed FeaturePython)
  Dunit = g/cm3
  Dvalue = 7.9
  Group = -> [Cd_element002,W_element001,O_element020]
  conduct = 2
  density = 1
  expand = 3
  formula = G4_CADMIUM_TUNGSTATE
  name = G4_CADMIUM_TUNGSTATE
  specific = 4
FEATURE [App::DocumentObjectGroupPython] Ca_element005  label="Ca_element : 1"  # scripted group (container) (typed FeaturePython)
  n = 1
  ref = Ca_element
FEATURE [App::DocumentObjectGroupPython] C_element022  label="C_element : 009"  # scripted group (container) (typed FeaturePython)
  n = 1
  ref = C_element
FEATURE [App::DocumentObjectGroupPython] O_element021  label="O_element : 009"  # scripted group (container) (typed FeaturePython)
  n = 3
  ref = O_element
FEATURE [App::DocumentObjectGroupPython] G4_CALCIUM_CARBONATE  # scripted group (container) (typed FeaturePython)
  Dunit = g/cm3
  Dvalue = 2.8
  Group = -> [Ca_element005,C_element022,O_element021]
  conduct = 2
  density = 1
  expand = 3
  formula = G4_CALCIUM_CARBONATE
  name = G4_CALCIUM_CARBONATE
  specific = 4
FEATURE [App::DocumentObjectGroupPython] Ca_element006  label="Ca_element : 002"  # scripted group (container) (typed FeaturePython)
  n = 1
  ref = Ca_element
FEATURE [App::DocumentObjectGroupPython] F_element005  label="F_element : 003"  # scripted group (container) (typed FeaturePython)
  n = 2
  ref = F_element
FEATURE [App::DocumentObjectGroupPython] G4_CALCIUM_FLUORIDE  # scripted group (container) (typed FeaturePython)
  Dunit = g/cm3
  Dvalue = 3.18
  Group = -> [Ca_element006,F_element005]
  conduct = 2
  density = 1
  expand = 3
  formula = G4_CALCIUM_FLUORIDE
  name = G4_CALCIUM_FLUORIDE
  specific = 4
FEATURE [App::DocumentObjectGroupPython] Ca_element007  label="Ca_element : 003"  # scripted group (container) (typed FeaturePython)
  n = 1
  ref = Ca_element
FEATURE [App::DocumentObjectGroupPython] O_element022  label="O_element : 010"  # scripted group (container) (typed FeaturePython)
  n = 1
  ref = O_element
FEATURE [App::DocumentObjectGroupPython] G4_CALCIUM_OXIDE  # scripted group (container) (typed FeaturePython)
  Dunit = g/cm3
  Dvalue = 3.3
  Group = -> [Ca_element007,O_element022]
  conduct = 2
  density = 1
  expand = 3
  formula = G4_CALCIUM_OXIDE
  name = G4_CALCIUM_OXIDE
  specific = 4
FEATURE [App::DocumentObjectGroupPython] Ca_element008  label="Ca_element : 004"  # scripted group (container) (typed FeaturePython)
  n = 1
  ref = Ca_element
FEATURE [App::DocumentObjectGroupPython] S_element007  label="S_element : 002"  # scripted group (container) (typed FeaturePython)
  n = 1
  ref = S_element
FEATURE [App::DocumentObjectGroupPython] O_element023  label="O_element : 011"  # scripted group (container) (typed FeaturePython)
  n = 4
  ref = O_element
FEATURE [App::DocumentObjectGroupPython] G4_CALCIUM_SULFATE  # scripted group (container) (typed FeaturePython)
  Dunit = g/cm3
  Dvalue = 2.96
  Group = -> [Ca_element008,S_element007,O_element023]
  conduct = 2
  density = 1
  expand = 3
  formula = G4_CALCIUM_SULFATE
  name = G4_CALCIUM_SULFATE
  specific = 4
FEATURE [App::DocumentObjectGroupPython] Ca_element009  label="Ca_element : 005"  # scripted group (container) (typed FeaturePython)
  n = 1
  ref = Ca_element
FEATURE [App::DocumentObjectGroupPython] W_element002  label="W_element : 002"  # scripted group (container) (typed FeaturePython)
  n = 1
  ref = W_element
FEATURE [App::DocumentObjectGroupPython] O_element024  label="O_element : 012"  # scripted group (container) (typed FeaturePython)
  n = 4
  ref = O_element
FEATURE [App::DocumentObjectGroupPython] G4_CALCIUM_TUNGSTATE  # scripted group (container) (typed FeaturePython)
  Dunit = g/cm3
  Dvalue = 6.062
  Group = -> [Ca_element009,W_element002,O_element024]
  conduct = 2
  density = 1
  expand = 3
  formula = G4_CALCIUM_TUNGSTATE
  name = G4_CALCIUM_TUNGSTATE
  specific = 4
FEATURE [App::DocumentObjectGroupPython] C_element023  label="C_element : 010"  # scripted group (container) (typed FeaturePython)
  n = 1
  ref = C_element
FEATURE [App::DocumentObjectGroupPython] O_element025  label="O_element : 013"  # scripted group (container) (typed FeaturePython)
  n = 2
  ref = O_element
FEATURE [App::DocumentObjectGroupPython] G4_CARBON_DIOXIDE  # scripted group (container) (typed FeaturePython)
  Dunit = g/cm3
  Dvalue = 0.00184212
  Group = -> [C_element023,O_element025]
  conduct = 2
  density = 1
  expand = 3
  formula = G4_CARBON_DIOXIDE
  name = G4_CARBON_DIOXIDE
  specific = 4
FEATURE [App::DocumentObjectGroupPython] C_element024  label="C_element : 011"  # scripted group (container) (typed FeaturePython)
  n = 1
  ref = C_element
FEATURE [App::DocumentObjectGroupPython] Cl_element004  label="Cl_element : 4"  # scripted group (container) (typed FeaturePython)
  n = 4
  ref = Cl_element
FEATURE [App::DocumentObjectGroupPython] G4_CARBON_TETRACHLORIDE  # scripted group (container) (typed FeaturePython)
  Dunit = g/cm3
  Dvalue = 1.594
  Group = -> [C_element024,Cl_element004]
  conduct = 2
  density = 1
  expand = 3
  formula = G4_CARBON_TETRACHLORIDE
  name = G4_CARBON_TETRACHLORIDE
  specific = 4
FEATURE [App::DocumentObjectGroupPython] C_element025  label="C_element : 012"  # scripted group (container) (typed FeaturePython)
  n = 6
  ref = C_element
FEATURE [App::DocumentObjectGroupPython] H_element021  label="H_element : 012"  # scripted group (container) (typed FeaturePython)
  n = 10
  ref = H_element
FEATURE [App::DocumentObjectGroupPython] O_element026  label="O_element : 5"  # scripted group (container) (typed FeaturePython)
  n = 5
  ref = O_element
FEATURE [App::DocumentObjectGroupPython] G4_CELLULOSE_CELLOPHANE  # scripted group (container) (typed FeaturePython)
  Dunit = g/cm3
  Dvalue = 1.42
  Group = -> [C_element025,H_element021,O_element026]
  conduct = 2
  density = 1
  expand = 3
  formula = G4_CELLULOSE_CELLOPHANE
  name = G4_CELLULOSE_CELLOPHANE
  specific = 4
FEATURE [App::DocumentObjectGroupPython] H_element022  label="H_element : 0.067"  # scripted group (container) (typed FeaturePython)
  n = 0.067125
FEATURE [App::DocumentObjectGroupPython] C_element026  label="C_element : 0.545"  # scripted group (container) (typed FeaturePython)
  n = 0.545403
FEATURE [App::DocumentObjectGroupPython] O_element027  label="O_element : 0.387"  # scripted group (container) (typed FeaturePython)
  n = 0.387472
FEATURE [App::DocumentObjectGroupPython] G4_CELLULOSE_BUTYRATE  # scripted group (container) (typed FeaturePython)
  Dunit = g/cm3
  Dvalue = 1.2
  Group = -> [H_element022,C_element026,O_element027]
  conduct = 2
  density = 1
  expand = 3
  formula = G4_CELLULOSE_BUTYRATE
  name = G4_CELLULOSE_BUTYRATE
  specific = 4
FEATURE [App::DocumentObjectGroupPython] H_element023  label="H_element : 0.029"  # scripted group (container) (typed FeaturePython)
  n = 0.029216
FEATURE [App::DocumentObjectGroupPython] C_element027  label="C_element : 0.271"  # scripted group (container) (typed FeaturePython)
  n = 0.271296
FEATURE [App::DocumentObjectGroupPython] N_element013  label="N_element : 0.121"  # scripted group (container) (typed FeaturePython)
  n = 0.121276
FEATURE [App::DocumentObjectGroupPython] O_element028  label="O_element : 0.578"  # scripted group (container) (typed FeaturePython)
  n = 0.578212
FEATURE [App::DocumentObjectGroupPython] G4_CELLULOSE_NITRATE  # scripted group (container) (typed FeaturePython)
  Dunit = g/cm3
  Dvalue = 1.49
  Group = -> [H_element023,C_element027,N_element013,O_element028]
  conduct = 2
  density = 1
  expand = 3
  formula = G4_CELLULOSE_NITRATE
  name = G4_CELLULOSE_NITRATE
  specific = 4
FEATURE [App::DocumentObjectGroupPython] H_element024  label="H_element : 0.108"  # scripted group (container) (typed FeaturePython)
  n = 0.107596
FEATURE [App::DocumentObjectGroupPython] N_element014  label="N_element : 0.001"  # scripted group (container) (typed FeaturePython)
  n = 0.0008
FEATURE [App::DocumentObjectGroupPython] O_element029  label="O_element : 0.875"  # scripted group (container) (typed FeaturePython)
  n = 0.874976
FEATURE [App::DocumentObjectGroupPython] S_element008  label="S_element : 0.015"  # scripted group (container) (typed FeaturePython)
  n = 0.014627
FEATURE [App::DocumentObjectGroupPython] Ce_element001  label="Ce_element : 0.002"  # scripted group (container) (typed FeaturePython)
  n = 0.002001
FEATURE [App::DocumentObjectGroupPython] G4_CERIC_SULFATE  # scripted group (container) (typed FeaturePython)
  Dunit = g/cm3
  Dvalue = 1.03
  Group = -> [H_element024,N_element014,O_element029,S_element008,Ce_element001]
  conduct = 2
  density = 1
  expand = 3
  formula = G4_CERIC_SULFATE
  name = G4_CERIC_SULFATE
  specific = 4
FEATURE [App::DocumentObjectGroupPython] Cs_element001  label="Cs_element : 1"  # scripted group (container) (typed FeaturePython)
  n = 1
  ref = Cs_element
FEATURE [App::DocumentObjectGroupPython] F_element006  label="F_element : 1"  # scripted group (container) (typed FeaturePython)
  n = 1
  ref = F_element
FEATURE [App::DocumentObjectGroupPython] G4_CESIUM_FLUORIDE  # scripted group (container) (typed FeaturePython)
  Dunit = g/cm3
  Dvalue = 4.115
  Group = -> [Cs_element001,F_element006]
  conduct = 2
  density = 1
  expand = 3
  formula = G4_CESIUM_FLUORIDE
  name = G4_CESIUM_FLUORIDE
  specific = 4
FEATURE [App::DocumentObjectGroupPython] Cs_element002  label="Cs_element : 002"  # scripted group (container) (typed FeaturePython)
  n = 1
  ref = Cs_element
FEATURE [App::DocumentObjectGroupPython] I_element001  label="I_element : 1"  # scripted group (container) (typed FeaturePython)
  n = 1
  ref = I_element
FEATURE [App::DocumentObjectGroupPython] G4_CESIUM_IODIDE  # scripted group (container) (typed FeaturePython)
  Dunit = g/cm3
  Dvalue = 4.51
  Group = -> [Cs_element002,I_element001]
  conduct = 2
  density = 1
  expand = 3
  formula = G4_CESIUM_IODIDE
  name = G4_CESIUM_IODIDE
  specific = 4
FEATURE [App::DocumentObjectGroupPython] C_element028  label="C_element : 013"  # scripted group (container) (typed FeaturePython)
  n = 6
  ref = C_element
FEATURE [App::DocumentObjectGroupPython] H_element025  label="H_element : 013"  # scripted group (container) (typed FeaturePython)
  n = 5
  ref = H_element
FEATURE [App::DocumentObjectGroupPython] Cl_element005  label="Cl_element : 1"  # scripted group (container) (typed FeaturePython)
  n = 1
  ref = Cl_element
FEATURE [App::DocumentObjectGroupPython] G4_CHLOROBENZENE  # scripted group (container) (typed FeaturePython)
  Dunit = g/cm3
  Dvalue = 1.1058
  Group = -> [C_element028,H_element025,Cl_element005]
  conduct = 2
  density = 1
  expand = 3
  formula = G4_CHLOROBENZENE
  name = G4_CHLOROBENZENE
  specific = 4
FEATURE [App::DocumentObjectGroupPython] C_element029  label="C_element : 014"  # scripted group (container) (typed FeaturePython)
  n = 1
  ref = C_element
FEATURE [App::DocumentObjectGroupPython] H_element026  label="H_element : 1"  # scripted group (container) (typed FeaturePython)
  n = 1
  ref = H_element
FEATURE [App::DocumentObjectGroupPython] Cl_element006  label="Cl_element : 3"  # scripted group (container) (typed FeaturePython)
  n = 3
  ref = Cl_element
FEATURE [App::DocumentObjectGroupPython] G4_CHLOROFORM  # scripted group (container) (typed FeaturePython)
  Dunit = g/cm3
  Dvalue = 1.4832
  Group = -> [C_element029,H_element026,Cl_element006]
  conduct = 2
  density = 1
  expand = 3
  formula = G4_CHLOROFORM
  name = G4_CHLOROFORM
  specific = 4
FEATURE [App::DocumentObjectGroupPython] H_element027  label="H_element : 0.010"  # scripted group (container) (typed FeaturePython)
  n = 0.01
FEATURE [App::DocumentObjectGroupPython] C_element030  label="C_element : 0.001"  # scripted group (container) (typed FeaturePython)
  n = 0.001
FEATURE [App::DocumentObjectGroupPython] O_element030  label="O_element : 0.529"  # scripted group (container) (typed FeaturePython)
  n = 0.529107
FEATURE [App::DocumentObjectGroupPython] Na_element005  label="Na_element : 0.016"  # scripted group (container) (typed FeaturePython)
  n = 0.016
FEATURE [App::DocumentObjectGroupPython] Mg_element003  label="Mg_element : 0.004"  # scripted group (container) (typed FeaturePython)
  n = 0.002
FEATURE [App::DocumentObjectGroupPython] Al_element002  label="Al_element : 0.034"  # scripted group (container) (typed FeaturePython)
  n = 0.033872
FEATURE [App::DocumentObjectGroupPython] Si_element002  label="Si_element : 0.337"  # scripted group (container) (typed FeaturePython)
  n = 0.337021
FEATURE [App::DocumentObjectGroupPython] K_element003  label="K_element : 0.013"  # scripted group (container) (typed FeaturePython)
  n = 0.013
FEATURE [App::DocumentObjectGroupPython] Ca_element010  label="Ca_element : 0.044"  # scripted group (container) (typed FeaturePython)
  n = 0.044
FEATURE [App::DocumentObjectGroupPython] Fe_element002  label="Fe_element : 0.014"  # scripted group (container) (typed FeaturePython)
  n = 0.014
FEATURE [App::DocumentObjectGroupPython] G4_CONCRETE  # scripted group (container) (typed FeaturePython)
  Dunit = g/cm3
  Dvalue = 2.3
  Group = -> [H_element027,C_element030,O_element030,Na_element005,Mg_element003,Al_element002,Si_element002,K_element003,Ca_element010,Fe_element002]
  conduct = 2
  density = 1
  expand = 3
  formula = G4_CONCRETE
  name = G4_CONCRETE
  specific = 4
FEATURE [App::DocumentObjectGroupPython] C_element031  label="C_element : 015"  # scripted group (container) (typed FeaturePython)
  n = 6
  ref = C_element
FEATURE [App::DocumentObjectGroupPython] H_element028  label="H_element : 12"  # scripted group (container) (typed FeaturePython)
  n = 12
  ref = H_element
FEATURE [App::DocumentObjectGroupPython] G4_CYCLOHEXANE  # scripted group (container) (typed FeaturePython)
  Dunit = g/cm3
  Dvalue = 0.779
  Group = -> [C_element031,H_element028]
  conduct = 2
  density = 1
  expand = 3
  formula = G4_CYCLOHEXANE
  name = G4_CYCLOHEXANE
  specific = 4
FEATURE [App::DocumentObjectGroupPython] C_element032  label="C_element : 016"  # scripted group (container) (typed FeaturePython)
  n = 6
  ref = C_element
FEATURE [App::DocumentObjectGroupPython] H_element029  label="H_element : 4"  # scripted group (container) (typed FeaturePython)
  n = 4
  ref = H_element
FEATURE [App::DocumentObjectGroupPython] Cl_element007  label="Cl_element : 2"  # scripted group (container) (typed FeaturePython)
  n = 2
  ref = Cl_element
FEATURE [App::DocumentObjectGroupPython] G4_1_2_DICHLOROBENZENE  label="G4_1.2-DICHLOROBENZENE"  # scripted group (container) (typed FeaturePython)
  Dunit = g/cm3
  Dvalue = 1.3048
  Group = -> [C_element032,H_element029,Cl_element007]
  conduct = 2
  density = 1
  expand = 3
  formula = G4_1.2-DICHLOROBENZENE
  name = G4_1.2-DICHLOROBENZENE
  specific = 4
FEATURE [App::DocumentObjectGroupPython] C_element033  label="C_element : 017"  # scripted group (container) (typed FeaturePython)
  n = 4
  ref = C_element
FEATURE [App::DocumentObjectGroupPython] H_element030  label="H_element : 8"  # scripted group (container) (typed FeaturePython)
  n = 8
  ref = H_element
FEATURE [App::DocumentObjectGroupPython] O_element031  label="O_element : 014"  # scripted group (container) (typed FeaturePython)
  n = 1
  ref = O_element
FEATURE [App::DocumentObjectGroupPython] Cl_element008  label="Cl_element : 005"  # scripted group (container) (typed FeaturePython)
  n = 2
  ref = Cl_element
FEATURE [App::DocumentObjectGroupPython] G4_DICHLORODIETHYL_ETHER  # scripted group (container) (typed FeaturePython)
  Dunit = g/cm3
  Dvalue = 1.2199
  Group = -> [C_element033,H_element030,O_element031,Cl_element008]
  conduct = 2
  density = 1
  expand = 3
  formula = G4_DICHLORODIETHYL_ETHER
  name = G4_DICHLORODIETHYL_ETHER
  specific = 4
FEATURE [App::DocumentObjectGroupPython] C_element034  label="C_element : 018"  # scripted group (container) (typed FeaturePython)
  n = 2
  ref = C_element
FEATURE [App::DocumentObjectGroupPython] H_element031  label="H_element : 014"  # scripted group (container) (typed FeaturePython)
  n = 4
  ref = H_element
FEATURE [App::DocumentObjectGroupPython] Cl_element009  label="Cl_element : 006"  # scripted group (container) (typed FeaturePython)
  n = 2
  ref = Cl_element
FEATURE [App::DocumentObjectGroupPython] G4_1_2_DICHLOROETHANE  label="G4_1.2-DICHLOROETHANE"  # scripted group (container) (typed FeaturePython)
  Dunit = g/cm3
  Dvalue = 1.2351
  Group = -> [C_element034,H_element031,Cl_element009]
  conduct = 2
  density = 1
  expand = 3
  formula = G4_1.2-DICHLOROETHANE
  name = G4_1.2-DICHLOROETHANE
  specific = 4
FEATURE [App::DocumentObjectGroupPython] C_element035  label="C_element : 019"  # scripted group (container) (typed FeaturePython)
  n = 4
  ref = C_element
FEATURE [App::DocumentObjectGroupPython] H_element032  label="H_element : 015"  # scripted group (container) (typed FeaturePython)
  n = 10
  ref = H_element
FEATURE [App::DocumentObjectGroupPython] O_element032  label="O_element : 015"  # scripted group (container) (typed FeaturePython)
  n = 1
  ref = O_element
FEATURE [App::DocumentObjectGroupPython] G4_DIETHYL_ETHER  # scripted group (container) (typed FeaturePython)
  Dunit = g/cm3
  Dvalue = 0.71378
  Group = -> [C_element035,H_element032,O_element032]
  conduct = 2
  density = 1
  expand = 3
  formula = G4_DIETHYL_ETHER
  name = G4_DIETHYL_ETHER
  specific = 4
FEATURE [App::DocumentObjectGroupPython] C_element036  label="C_element : 020"  # scripted group (container) (typed FeaturePython)
  n = 3
  ref = C_element
FEATURE [App::DocumentObjectGroupPython] H_element033  label="H_element : 016"  # scripted group (container) (typed FeaturePython)
  n = 7
  ref = H_element
FEATURE [App::DocumentObjectGroupPython] N_element015  label="N_element : 008"  # scripted group (container) (typed FeaturePython)
  n = 1
  ref = N_element
FEATURE [App::DocumentObjectGroupPython] O_element033  label="O_element : 016"  # scripted group (container) (typed FeaturePython)
  n = 1
  ref = O_element
FEATURE [App::DocumentObjectGroupPython] G4_N_N_DIMETHYL_FORMAMIDE  label="G4_N.N-DIMETHYL_FORMAMIDE"  # scripted group (container) (typed FeaturePython)
  Dunit = g/cm3
  Dvalue = 0.9487
  Group = -> [C_element036,H_element033,N_element015,O_element033]
  conduct = 2
  density = 1
  expand = 3
  formula = G4_N.N-DIMETHYL_FORMAMIDE
  name = G4_N.N-DIMETHYL_FORMAMIDE
  specific = 4
FEATURE [App::DocumentObjectGroupPython] C_element037  label="C_element : 021"  # scripted group (container) (typed FeaturePython)
  n = 2
  ref = C_element
FEATURE [App::DocumentObjectGroupPython] H_element034  label="H_element : 017"  # scripted group (container) (typed FeaturePython)
  n = 6
  ref = H_element
FEATURE [App::DocumentObjectGroupPython] O_element034  label="O_element : 017"  # scripted group (container) (typed FeaturePython)
  n = 1
  ref = O_element
FEATURE [App::DocumentObjectGroupPython] S_element009  label="S_element : 003"  # scripted group (container) (typed FeaturePython)
  n = 1
  ref = S_element
FEATURE [App::DocumentObjectGroupPython] G4_DIMETHYL_SULFOXIDE  # scripted group (container) (typed FeaturePython)
  Dunit = g/cm3
  Dvalue = 1.1014
  Group = -> [C_element037,H_element034,O_element034,S_element009]
  conduct = 2
  density = 1
  expand = 3
  formula = G4_DIMETHYL_SULFOXIDE
  name = G4_DIMETHYL_SULFOXIDE
  specific = 4
FEATURE [App::DocumentObjectGroupPython] C_element038  label="C_element : 022"  # scripted group (container) (typed FeaturePython)
  n = 2
  ref = C_element
FEATURE [App::DocumentObjectGroupPython] H_element035  label="H_element : 018"  # scripted group (container) (typed FeaturePython)
  n = 6
  ref = H_element
FEATURE [App::DocumentObjectGroupPython] G4_ETHANE  # scripted group (container) (typed FeaturePython)
  Dunit = g/cm3
  Dvalue = 0.00125324
  Group = -> [C_element038,H_element035]
  conduct = 2
  density = 1
  expand = 3
  formula = G4_ETHANE
  name = G4_ETHANE
  specific = 4
FEATURE [App::DocumentObjectGroupPython] C_element039  label="C_element : 023"  # scripted group (container) (typed FeaturePython)
  n = 2
  ref = C_element
FEATURE [App::DocumentObjectGroupPython] H_element036  label="H_element : 019"  # scripted group (container) (typed FeaturePython)
  n = 6
  ref = H_element
FEATURE [App::DocumentObjectGroupPython] O_element035  label="O_element : 018"  # scripted group (container) (typed FeaturePython)
  n = 1
  ref = O_element
FEATURE [App::DocumentObjectGroupPython] G4_ETHYL_ALCOHOL  # scripted group (container) (typed FeaturePython)
  Dunit = g/cm3
  Dvalue = 0.7893
  Group = -> [C_element039,H_element036,O_element035]
  conduct = 2
  density = 1
  expand = 3
  formula = G4_ETHYL_ALCOHOL
  name = G4_ETHYL_ALCOHOL
  specific = 4
FEATURE [App::DocumentObjectGroupPython] H_element037  label="H_element : 0.090"  # scripted group (container) (typed FeaturePython)
  n = 0.090027
FEATURE [App::DocumentObjectGroupPython] C_element040  label="C_element : 0.585"  # scripted group (container) (typed FeaturePython)
  n = 0.585182
FEATURE [App::DocumentObjectGroupPython] O_element036  label="O_element : 0.325"  # scripted group (container) (typed FeaturePython)
  n = 0.324791
FEATURE [App::DocumentObjectGroupPython] G4_ETHYL_CELLULOSE  # scripted group (container) (typed FeaturePython)
  Dunit = g/cm3
  Dvalue = 1.13
  Group = -> [H_element037,C_element040,O_element036]
  conduct = 2
  density = 1
  expand = 3
  formula = G4_ETHYL_CELLULOSE
  name = G4_ETHYL_CELLULOSE
  specific = 4
FEATURE [App::DocumentObjectGroupPython] C_element041  label="C_element : 024"  # scripted group (container) (typed FeaturePython)
  n = 2
  ref = C_element
FEATURE [App::DocumentObjectGroupPython] H_element038  label="H_element : 020"  # scripted group (container) (typed FeaturePython)
  n = 4
  ref = H_element
FEATURE [App::DocumentObjectGroupPython] G4_ETHYLENE  # scripted group (container) (typed FeaturePython)
  Dunit = g/cm3
  Dvalue = 0.00117497
  Group = -> [C_element041,H_element038]
  conduct = 2
  density = 1
  expand = 3
  formula = G4_ETHYLENE
  name = G4_ETHYLENE
  specific = 4
FEATURE [App::DocumentObjectGroupPython] H_element039  label="H_element : 0.096"  # scripted group (container) (typed FeaturePython)
  n = 0.096
FEATURE [App::DocumentObjectGroupPython] C_element042  label="C_element : 0.195"  # scripted group (container) (typed FeaturePython)
  n = 0.195
FEATURE [App::DocumentObjectGroupPython] N_element016  label="N_element : 0.057"  # scripted group (container) (typed FeaturePython)
  n = 0.057
FEATURE [App::DocumentObjectGroupPython] O_element037  label="O_element : 0.646"  # scripted group (container) (typed FeaturePython)
  n = 0.646
FEATURE [App::DocumentObjectGroupPython] Na_element006  label="Na_element : 0.017"  # scripted group (container) (typed FeaturePython)
  n = 0.001
FEATURE [App::DocumentObjectGroupPython] P_element005  label="P_element : 0.104"  # scripted group (container) (typed FeaturePython)
  n = 0.001
FEATURE [App::DocumentObjectGroupPython] S_element010  label="S_element : 0.016"  # scripted group (container) (typed FeaturePython)
  n = 0.003
FEATURE [App::DocumentObjectGroupPython] Cl_element010  label="Cl_element : 0.005"  # scripted group (container) (typed FeaturePython)
  n = 0.001
FEATURE [App::DocumentObjectGroupPython] G4_EYE_LENS_ICRP  # scripted group (container) (typed FeaturePython)
  Dunit = g/cm3
  Dvalue = 1.07
  Group = -> [H_element039,C_element042,N_element016,O_element037,Na_element006,P_element005,S_element010,Cl_element010]
  conduct = 2
  density = 1
  expand = 3
  formula = G4_EYE_LENS_ICRP
  name = G4_EYE_LENS_ICRP
  specific = 4
FEATURE [App::DocumentObjectGroupPython] Fe_element003  label="Fe_element : 2"  # scripted group (container) (typed FeaturePython)
  n = 2
  ref = Fe_element
FEATURE [App::DocumentObjectGroupPython] O_element038  label="O_element : 019"  # scripted group (container) (typed FeaturePython)
  n = 3
  ref = O_element
FEATURE [App::DocumentObjectGroupPython] G4_FERRIC_OXIDE  # scripted group (container) (typed FeaturePython)
  Dunit = g/cm3
  Dvalue = 5.2
  Group = -> [Fe_element003,O_element038]
  conduct = 2
  density = 1
  expand = 3
  formula = G4_FERRIC_OXIDE
  name = G4_FERRIC_OXIDE
  specific = 4
FEATURE [App::DocumentObjectGroupPython] Fe_element004  label="Fe_element : 1"  # scripted group (container) (typed FeaturePython)
  n = 1
  ref = Fe_element
FEATURE [App::DocumentObjectGroupPython] B_element003  label="B_element : 1"  # scripted group (container) (typed FeaturePython)
  n = 1
  ref = B_element
FEATURE [App::DocumentObjectGroupPython] G4_FERROBORIDE  # scripted group (container) (typed FeaturePython)
  Dunit = g/cm3
  Dvalue = 7.15
  Group = -> [Fe_element004,B_element003]
  conduct = 2
  density = 1
  expand = 3
  formula = G4_FERROBORIDE
  name = G4_FERROBORIDE
  specific = 4
FEATURE [App::DocumentObjectGroupPython] Fe_element005  label="Fe_element : 003"  # scripted group (container) (typed FeaturePython)
  n = 1
  ref = Fe_element
FEATURE [App::DocumentObjectGroupPython] O_element039  label="O_element : 020"  # scripted group (container) (typed FeaturePython)
  n = 1
  ref = O_element
FEATURE [App::DocumentObjectGroupPython] G4_FERROUS_OXIDE  # scripted group (container) (typed FeaturePython)
  Dunit = g/cm3
  Dvalue = 5.7
  Group = -> [Fe_element005,O_element039]
  conduct = 2
  density = 1
  expand = 3
  formula = G4_FERROUS_OXIDE
  name = G4_FERROUS_OXIDE
  specific = 4
FEATURE [App::DocumentObjectGroupPython] H_element040  label="H_element : 0.115"  # scripted group (container) (typed FeaturePython)
  n = 0.108259
FEATURE [App::DocumentObjectGroupPython] N_element017  label="N_element : 0.000"  # scripted group (container) (typed FeaturePython)
  n = 2.7e-05
FEATURE [App::DocumentObjectGroupPython] O_element040  label="O_element : 0.879"  # scripted group (container) (typed FeaturePython)
  n = 0.878636
FEATURE [App::DocumentObjectGroupPython] Na_element007  label="Na_element : 0.000"  # scripted group (container) (typed FeaturePython)
  n = 2.2e-05
FEATURE [App::DocumentObjectGroupPython] S_element011  label="S_element : 0.013"  # scripted group (container) (typed FeaturePython)
  n = 0.012968
FEATURE [App::DocumentObjectGroupPython] Cl_element011  label="Cl_element : 0.000"  # scripted group (container) (typed FeaturePython)
  n = 3.4e-05
FEATURE [App::DocumentObjectGroupPython] Fe_element006  label="Fe_element : 0.000"  # scripted group (container) (typed FeaturePython)
  n = 5.4e-05
FEATURE [App::DocumentObjectGroupPython] G4_FERROUS_SULFATE  # scripted group (container) (typed FeaturePython)
  Dunit = g/cm3
  Dvalue = 1.024
  Group = -> [H_element040,N_element017,O_element040,Na_element007,S_element011,Cl_element011,Fe_element006]
  conduct = 2
  density = 1
  expand = 3
  formula = G4_FERROUS_SULFATE
  name = G4_FERROUS_SULFATE
  specific = 4
FEATURE [App::DocumentObjectGroupPython] C_element043  label="C_element : 0.099"  # scripted group (container) (typed FeaturePython)
  n = 0.099335
FEATURE [App::DocumentObjectGroupPython] F_element007  label="F_element : 0.314"  # scripted group (container) (typed FeaturePython)
  n = 0.314247
FEATURE [App::DocumentObjectGroupPython] Cl_element012  label="Cl_element : 0.586"  # scripted group (container) (typed FeaturePython)
  n = 0.586418
FEATURE [App::DocumentObjectGroupPython] G4_FREON_12  label="G4_FREON-12"  # scripted group (container) (typed FeaturePython)
  Dunit = g/cm3
  Dvalue = 1.12
  Group = -> [C_element043,F_element007,Cl_element012]
  conduct = 2
  density = 1
  expand = 3
  formula = G4_FREON-12
  name = G4_FREON-12
  specific = 4
FEATURE [App::DocumentObjectGroupPython] C_element044  label="C_element : 0.057"  # scripted group (container) (typed FeaturePython)
  n = 0.057245
FEATURE [App::DocumentObjectGroupPython] F_element008  label="F_element : 0.181"  # scripted group (container) (typed FeaturePython)
  n = 0.181096
FEATURE [App::DocumentObjectGroupPython] Br_element001  label="Br_element : 0.762"  # scripted group (container) (typed FeaturePython)
  n = 0.761659
FEATURE [App::DocumentObjectGroupPython] G4_FREON_12B2  label="G4_FREON-12B2"  # scripted group (container) (typed FeaturePython)
  Dunit = g/cm3
  Dvalue = 1.8
  Group = -> [C_element044,F_element008,Br_element001]
  conduct = 2
  density = 1
  expand = 3
  formula = G4_FREON-12B2
  name = G4_FREON-12B2
  specific = 4
FEATURE [App::DocumentObjectGroupPython] C_element045  label="C_element : 0.115"  # scripted group (container) (typed FeaturePython)
  n = 0.114983
FEATURE [App::DocumentObjectGroupPython] F_element009  label="F_element : 0.546"  # scripted group (container) (typed FeaturePython)
  n = 0.545621
FEATURE [App::DocumentObjectGroupPython] Cl_element013  label="Cl_element : 0.339"  # scripted group (container) (typed FeaturePython)
  n = 0.339396
FEATURE [App::DocumentObjectGroupPython] G4_FREON_13  label="G4_FREON-13"  # scripted group (container) (typed FeaturePython)
  Dunit = g/cm3
  Dvalue = 0.95
  Group = -> [C_element045,F_element009,Cl_element013]
  conduct = 2
  density = 1
  expand = 3
  formula = G4_FREON-13
  name = G4_FREON-13
  specific = 4
FEATURE [App::DocumentObjectGroupPython] C_element046  label="C_element : 025"  # scripted group (container) (typed FeaturePython)
  n = 1
  ref = C_element
FEATURE [App::DocumentObjectGroupPython] F_element010  label="F_element : 3"  # scripted group (container) (typed FeaturePython)
  n = 3
  ref = F_element
FEATURE [App::DocumentObjectGroupPython] Br_element002  label="Br_element : 1"  # scripted group (container) (typed FeaturePython)
  n = 1
  ref = Br_element
FEATURE [App::DocumentObjectGroupPython] G4_FREON_13B1  label="G4_FREON-13B1"  # scripted group (container) (typed FeaturePython)
  Dunit = g/cm3
  Dvalue = 1.5
  Group = -> [C_element046,F_element010,Br_element002]
  conduct = 2
  density = 1
  expand = 3
  formula = G4_FREON-13B1
  name = G4_FREON-13B1
  specific = 4
FEATURE [App::DocumentObjectGroupPython] C_element047  label="C_element : 0.061"  # scripted group (container) (typed FeaturePython)
  n = 0.061309
FEATURE [App::DocumentObjectGroupPython] F_element011  label="F_element : 0.291"  # scripted group (container) (typed FeaturePython)
  n = 0.290924
FEATURE [App::DocumentObjectGroupPython] I_element002  label="I_element : 0.648"  # scripted group (container) (typed FeaturePython)
  n = 0.647767
FEATURE [App::DocumentObjectGroupPython] G4_FREON_13I1  label="G4_FREON-13I1"  # scripted group (container) (typed FeaturePython)
  Dunit = g/cm3
  Dvalue = 1.8
  Group = -> [C_element047,F_element011,I_element002]
  conduct = 2
  density = 1
  expand = 3
  formula = G4_FREON-13I1
  name = G4_FREON-13I1
  specific = 4
FEATURE [App::DocumentObjectGroupPython] Gd_element001  label="Gd_element : 2"  # scripted group (container) (typed FeaturePython)
  n = 2
  ref = Gd_element
FEATURE [App::DocumentObjectGroupPython] O_element041  label="O_element : 021"  # scripted group (container) (typed FeaturePython)
  n = 2
  ref = O_element
FEATURE [App::DocumentObjectGroupPython] S_element012  label="S_element : 004"  # scripted group (container) (typed FeaturePython)
  n = 1
  ref = S_element
FEATURE [App::DocumentObjectGroupPython] G4_GADOLINIUM_OXYSULFIDE  # scripted group (container) (typed FeaturePython)
  Dunit = g/cm3
  Dvalue = 7.44
  Group = -> [Gd_element001,O_element041,S_element012]
  conduct = 2
  density = 1
  expand = 3
  formula = G4_GADOLINIUM_OXYSULFIDE
  name = G4_GADOLINIUM_OXYSULFIDE
  specific = 4
FEATURE [App::DocumentObjectGroupPython] Ga_element001  label="Ga_element : 1"  # scripted group (container) (typed FeaturePython)
  n = 1
  ref = Ga_element
FEATURE [App::DocumentObjectGroupPython] As_element001  label="As_element : 1"  # scripted group (container) (typed FeaturePython)
  n = 1
  ref = As_element
FEATURE [App::DocumentObjectGroupPython] G4_GALLIUM_ARSENIDE  # scripted group (container) (typed FeaturePython)
  Dunit = g/cm3
  Dvalue = 5.31
  Group = -> [Ga_element001,As_element001]
  conduct = 2
  density = 1
  expand = 3
  formula = G4_GALLIUM_ARSENIDE
  name = G4_GALLIUM_ARSENIDE
  specific = 4
FEATURE [App::DocumentObjectGroupPython] H_element041  label="H_element : 0.081"  # scripted group (container) (typed FeaturePython)
  n = 0.08118
FEATURE [App::DocumentObjectGroupPython] C_element048  label="C_element : 0.416"  # scripted group (container) (typed FeaturePython)
  n = 0.41606
FEATURE [App::DocumentObjectGroupPython] N_element018  label="N_element : 0.111"  # scripted group (container) (typed FeaturePython)
  n = 0.11124
FEATURE [App::DocumentObjectGroupPython] O_element042  label="O_element : 0.381"  # scripted group (container) (typed FeaturePython)
  n = 0.38064
FEATURE [App::DocumentObjectGroupPython] S_element013  label="S_element : 0.011"  # scripted group (container) (typed FeaturePython)
  n = 0.01088
FEATURE [App::DocumentObjectGroupPython] G4_GEL_PHOTO_EMULSION  # scripted group (container) (typed FeaturePython)
  Dunit = g/cm3
  Dvalue = 1.2914
  Group = -> [H_element041,C_element048,N_element018,O_element042,S_element013]
  conduct = 2
  density = 1
  expand = 3
  formula = G4_GEL_PHOTO_EMULSION
  name = G4_GEL_PHOTO_EMULSION
  specific = 4
FEATURE [App::DocumentObjectGroupPython] B_element004  label="B_element : 0.040"  # scripted group (container) (typed FeaturePython)
  n = 0.0400639
FEATURE [App::DocumentObjectGroupPython] O_element043  label="O_element : 0.540"  # scripted group (container) (typed FeaturePython)
  n = 0.539561
FEATURE [App::DocumentObjectGroupPython] Na_element008  label="Na_element : 0.028"  # scripted group (container) (typed FeaturePython)
  n = 0.0281909
FEATURE [App::DocumentObjectGroupPython] Al_element003  label="Al_element : 0.012"  # scripted group (container) (typed FeaturePython)
  n = 0.011644
FEATURE [App::DocumentObjectGroupPython] Si_element003  label="Si_element : 0.377"  # scripted group (container) (typed FeaturePython)
  n = 0.377219
FEATURE [App::DocumentObjectGroupPython] K_element004  label="K_element : 0.014"  # scripted group (container) (typed FeaturePython)
  n = 0.00332099
FEATURE [App::DocumentObjectGroupPython] G4_Pyrex_Glass  # scripted group (container) (typed FeaturePython)
  Dunit = g/cm3
  Dvalue = 2.23
  Group = -> [B_element004,O_element043,Na_element008,Al_element003,Si_element003,K_element004]
  conduct = 2
  density = 1
  expand = 3
  formula = G4_Pyrex_Glass
  name = G4_Pyrex_Glass
  specific = 4
FEATURE [App::DocumentObjectGroupPython] O_element044  label="O_element : 0.156"  # scripted group (container) (typed FeaturePython)
  n = 0.156453
FEATURE [App::DocumentObjectGroupPython] Si_element004  label="Si_element : 0.081"  # scripted group (container) (typed FeaturePython)
  n = 0.080866
FEATURE [App::DocumentObjectGroupPython] Ti_element001  label="Ti_element : 0.008"  # scripted group (container) (typed FeaturePython)
  n = 0.008092
FEATURE [App::DocumentObjectGroupPython] As_element002  label="As_element : 0.003"  # scripted group (container) (typed FeaturePython)
  n = 0.002651
FEATURE [App::DocumentObjectGroupPython] Pb_element001  label="Pb_element : 0.752"  # scripted group (container) (typed FeaturePython)
  n = 0.751938
FEATURE [App::DocumentObjectGroupPython] G4_GLASS_LEAD  # scripted group (container) (typed FeaturePython)
  Dunit = g/cm3
  Dvalue = 6.22
  Group = -> [O_element044,Si_element004,Ti_element001,As_element002,Pb_element001]
  conduct = 2
  density = 1
  expand = 3
  formula = G4_GLASS_LEAD
  name = G4_GLASS_LEAD
  specific = 4
FEATURE [App::DocumentObjectGroupPython] O_element045  label="O_element : 0.460"  # scripted group (container) (typed FeaturePython)
  n = 0.4598
FEATURE [App::DocumentObjectGroupPython] Na_element009  label="Na_element : 0.096"  # scripted group (container) (typed FeaturePython)
  n = 0.0964411
FEATURE [App::DocumentObjectGroupPython] Si_element005  label="Si_element : 0.378"  # scripted group (container) (typed FeaturePython)
  n = 0.336553
FEATURE [App::DocumentObjectGroupPython] Ca_element011  label="Ca_element : 0.107"  # scripted group (container) (typed FeaturePython)
  n = 0.107205
FEATURE [App::DocumentObjectGroupPython] G4_GLASS_PLATE  # scripted group (container) (typed FeaturePython)
  Dunit = g/cm3
  Dvalue = 2.4
  Group = -> [O_element045,Na_element009,Si_element005,Ca_element011]
  conduct = 2
  density = 1
  expand = 3
  formula = G4_GLASS_PLATE
  name = G4_GLASS_PLATE
  specific = 4
FEATURE [App::DocumentObjectGroupPython] C_element049  label="C_element : 026"  # scripted group (container) (typed FeaturePython)
  n = 5
  ref = C_element
FEATURE [App::DocumentObjectGroupPython] H_element042  label="H_element : 021"  # scripted group (container) (typed FeaturePython)
  n = 10
  ref = H_element
FEATURE [App::DocumentObjectGroupPython] N_element019  label="N_element : 2"  # scripted group (container) (typed FeaturePython)
  n = 2
  ref = N_element
FEATURE [App::DocumentObjectGroupPython] O_element046  label="O_element : 022"  # scripted group (container) (typed FeaturePython)
  n = 3
  ref = O_element
FEATURE [App::DocumentObjectGroupPython] G4_GLUTAMINE  # scripted group (container) (typed FeaturePython)
  Dunit = g/cm3
  Dvalue = 1.46
  Group = -> [C_element049,H_element042,N_element019,O_element046]
  conduct = 2
  density = 1
  expand = 3
  formula = G4_GLUTAMINE
  name = G4_GLUTAMINE
  specific = 4
FEATURE [App::DocumentObjectGroupPython] C_element050  label="C_element : 027"  # scripted group (container) (typed FeaturePython)
  n = 3
  ref = C_element
FEATURE [App::DocumentObjectGroupPython] H_element043  label="H_element : 022"  # scripted group (container) (typed FeaturePython)
  n = 8
  ref = H_element
FEATURE [App::DocumentObjectGroupPython] O_element047  label="O_element : 023"  # scripted group (container) (typed FeaturePython)
  n = 3
  ref = O_element
FEATURE [App::DocumentObjectGroupPython] G4_GLYCEROL  # scripted group (container) (typed FeaturePython)
  Dunit = g/cm3
  Dvalue = 1.2613
  Group = -> [C_element050,H_element043,O_element047]
  conduct = 2
  density = 1
  expand = 3
  formula = G4_GLYCEROL
  name = G4_GLYCEROL
  specific = 4
FEATURE [App::DocumentObjectGroupPython] C_element051  label="C_element : 028"  # scripted group (container) (typed FeaturePython)
  n = 5
  ref = C_element
FEATURE [App::DocumentObjectGroupPython] H_element044  label="H_element : 023"  # scripted group (container) (typed FeaturePython)
  n = 5
  ref = H_element
FEATURE [App::DocumentObjectGroupPython] N_element020  label="N_element : 009"  # scripted group (container) (typed FeaturePython)
  n = 5
  ref = N_element
FEATURE [App::DocumentObjectGroupPython] O_element048  label="O_element : 024"  # scripted group (container) (typed FeaturePython)
  n = 1
  ref = O_element
FEATURE [App::DocumentObjectGroupPython] G4_GUANINE  # scripted group (container) (typed FeaturePython)
  Dunit = g/cm3
  Dvalue = 2.2
  Group = -> [C_element051,H_element044,N_element020,O_element048]
  conduct = 2
  density = 1
  expand = 3
  formula = G4_GUANINE
  name = G4_GUANINE
  specific = 4
FEATURE [App::DocumentObjectGroupPython] Ca_element012  label="Ca_element : 006"  # scripted group (container) (typed FeaturePython)
  n = 1
  ref = Ca_element
FEATURE [App::DocumentObjectGroupPython] S_element014  label="S_element : 005"  # scripted group (container) (typed FeaturePython)
  n = 1
  ref = S_element
FEATURE [App::DocumentObjectGroupPython] O_element049  label="O_element : 6"  # scripted group (container) (typed FeaturePython)
  n = 6
  ref = O_element
FEATURE [App::DocumentObjectGroupPython] H_element045  label="H_element : 024"  # scripted group (container) (typed FeaturePython)
  n = 4
  ref = H_element
FEATURE [App::DocumentObjectGroupPython] G4_GYPSUM  # scripted group (container) (typed FeaturePython)
  Dunit = g/cm3
  Dvalue = 2.32
  Group = -> [Ca_element012,S_element014,O_element049,H_element045]
  conduct = 2
  density = 1
  expand = 3
  formula = G4_GYPSUM
  name = G4_GYPSUM
  specific = 4
FEATURE [App::DocumentObjectGroupPython] C_element052  label="C_element : 7"  # scripted group (container) (typed FeaturePython)
  n = 7
  ref = C_element
FEATURE [App::DocumentObjectGroupPython] H_element046  label="H_element : 16"  # scripted group (container) (typed FeaturePython)
  n = 16
  ref = H_element
FEATURE [App::DocumentObjectGroupPython] G4_N_HEPTANE  label="G4_N-HEPTANE"  # scripted group (container) (typed FeaturePython)
  Dunit = g/cm3
  Dvalue = 0.68376
  Group = -> [C_element052,H_element046]
  conduct = 2
  density = 1
  expand = 3
  formula = G4_N-HEPTANE
  name = G4_N-HEPTANE
  specific = 4
FEATURE [App::DocumentObjectGroupPython] C_element053  label="C_element : 029"  # scripted group (container) (typed FeaturePython)
  n = 6
  ref = C_element
FEATURE [App::DocumentObjectGroupPython] H_element047  label="H_element : 14"  # scripted group (container) (typed FeaturePython)
  n = 14
  ref = H_element
FEATURE [App::DocumentObjectGroupPython] G4_N_HEXANE  label="G4_N-HEXANE"  # scripted group (container) (typed FeaturePython)
  Dunit = g/cm3
  Dvalue = 0.6603
  Group = -> [C_element053,H_element047]
  conduct = 2
  density = 1
  expand = 3
  formula = G4_N-HEXANE
  name = G4_N-HEXANE
  specific = 4
FEATURE [App::DocumentObjectGroupPython] C_element054  label="C_element : 22"  # scripted group (container) (typed FeaturePython)
  n = 22
  ref = C_element
FEATURE [App::DocumentObjectGroupPython] H_element048  label="H_element : 025"  # scripted group (container) (typed FeaturePython)
  n = 10
  ref = H_element
FEATURE [App::DocumentObjectGroupPython] N_element021  label="N_element : 010"  # scripted group (container) (typed FeaturePython)
  n = 2
  ref = N_element
FEATURE [App::DocumentObjectGroupPython] O_element050  label="O_element : 025"  # scripted group (container) (typed FeaturePython)
  n = 5
  ref = O_element
FEATURE [App::DocumentObjectGroupPython] G4_KAPTON  # scripted group (container) (typed FeaturePython)
  Dunit = g/cm3
  Dvalue = 1.42
  Group = -> [C_element054,H_element048,N_element021,O_element050]
  conduct = 2
  density = 1
  expand = 3
  formula = G4_KAPTON
  name = G4_KAPTON
  specific = 4
FEATURE [App::DocumentObjectGroupPython] La_element001  label="La_element : 1"  # scripted group (container) (typed FeaturePython)
  n = 1
  ref = La_element
FEATURE [App::DocumentObjectGroupPython] Br_element003  label="Br_element : 002"  # scripted group (container) (typed FeaturePython)
  n = 1
  ref = Br_element
FEATURE [App::DocumentObjectGroupPython] O_element051  label="O_element : 026"  # scripted group (container) (typed FeaturePython)
  n = 1
  ref = O_element
FEATURE [App::DocumentObjectGroupPython] G4_LANTHANUM_OXYBROMIDE  # scripted group (container) (typed FeaturePython)
  Dunit = g/cm3
  Dvalue = 6.28
  Group = -> [La_element001,Br_element003,O_element051]
  conduct = 2
  density = 1
  expand = 3
  formula = G4_LANTHANUM_OXYBROMIDE
  name = G4_LANTHANUM_OXYBROMIDE
  specific = 4
FEATURE [App::DocumentObjectGroupPython] La_element002  label="La_element : 2"  # scripted group (container) (typed FeaturePython)
  n = 2
  ref = La_element
FEATURE [App::DocumentObjectGroupPython] O_element052  label="O_element : 027"  # scripted group (container) (typed FeaturePython)
  n = 2
  ref = O_element
FEATURE [App::DocumentObjectGroupPython] S_element015  label="S_element : 006"  # scripted group (container) (typed FeaturePython)
  n = 1
  ref = S_element
FEATURE [App::DocumentObjectGroupPython] G4_LANTHANUM_OXYSULFIDE  # scripted group (container) (typed FeaturePython)
  Dunit = g/cm3
  Dvalue = 5.86
  Group = -> [La_element002,O_element052,S_element015]
  conduct = 2
  density = 1
  expand = 3
  formula = G4_LANTHANUM_OXYSULFIDE
  name = G4_LANTHANUM_OXYSULFIDE
  specific = 4
FEATURE [App::DocumentObjectGroupPython] O_element053  label="O_element : 0.072"  # scripted group (container) (typed FeaturePython)
  n = 0.071682
FEATURE [App::DocumentObjectGroupPython] Pb_element002  label="Pb_element : 0.928"  # scripted group (container) (typed FeaturePython)
  n = 0.928318
FEATURE [App::DocumentObjectGroupPython] G4_LEAD_OXIDE  # scripted group (container) (typed FeaturePython)
  Dunit = g/cm3
  Dvalue = 9.53
  Group = -> [O_element053,Pb_element002]
  conduct = 2
  density = 1
  expand = 3
  formula = G4_LEAD_OXIDE
  name = G4_LEAD_OXIDE
  specific = 4
FEATURE [App::DocumentObjectGroupPython] Li_element001  label="Li_element : 1"  # scripted group (container) (typed FeaturePython)
  n = 1
  ref = Li_element
FEATURE [App::DocumentObjectGroupPython] N_element022  label="N_element : 011"  # scripted group (container) (typed FeaturePython)
  n = 1
  ref = N_element
FEATURE [App::DocumentObjectGroupPython] H_element049  label="H_element : 026"  # scripted group (container) (typed FeaturePython)
  n = 2
  ref = H_element
FEATURE [App::DocumentObjectGroupPython] G4_LITHIUM_AMIDE  # scripted group (container) (typed FeaturePython)
  Dunit = g/cm3
  Dvalue = 1.178
  Group = -> [Li_element001,N_element022,H_element049]
  conduct = 2
  density = 1
  expand = 3
  formula = G4_LITHIUM_AMIDE
  name = G4_LITHIUM_AMIDE
  specific = 4
FEATURE [App::DocumentObjectGroupPython] Li_element002  label="Li_element : 2"  # scripted group (container) (typed FeaturePython)
  n = 2
  ref = Li_element
FEATURE [App::DocumentObjectGroupPython] C_element055  label="C_element : 030"  # scripted group (container) (typed FeaturePython)
  n = 1
  ref = C_element
FEATURE [App::DocumentObjectGroupPython] O_element054  label="O_element : 028"  # scripted group (container) (typed FeaturePython)
  n = 3
  ref = O_element
FEATURE [App::DocumentObjectGroupPython] G4_LITHIUM_CARBONATE  # scripted group (container) (typed FeaturePython)
  Dunit = g/cm3
  Dvalue = 2.11
  Group = -> [Li_element002,C_element055,O_element054]
  conduct = 2
  density = 1
  expand = 3
  formula = G4_LITHIUM_CARBONATE
  name = G4_LITHIUM_CARBONATE
  specific = 4
FEATURE [App::DocumentObjectGroupPython] Li_element003  label="Li_element : 003"  # scripted group (container) (typed FeaturePython)
  n = 1
  ref = Li_element
FEATURE [App::DocumentObjectGroupPython] F_element012  label="F_element : 004"  # scripted group (container) (typed FeaturePython)
  n = 1
  ref = F_element
FEATURE [App::DocumentObjectGroupPython] G4_LITHIUM_FLUORIDE  # scripted group (container) (typed FeaturePython)
  Dunit = g/cm3
  Dvalue = 2.635
  Group = -> [Li_element003,F_element012]
  conduct = 2
  density = 1
  expand = 3
  formula = G4_LITHIUM_FLUORIDE
  name = G4_LITHIUM_FLUORIDE
  specific = 4
FEATURE [App::DocumentObjectGroupPython] Li_element004  label="Li_element : 004"  # scripted group (container) (typed FeaturePython)
  n = 1
  ref = Li_element
FEATURE [App::DocumentObjectGroupPython] H_element050  label="H_element : 027"  # scripted group (container) (typed FeaturePython)
  n = 1
  ref = H_element
FEATURE [App::DocumentObjectGroupPython] G4_LITHIUM_HYDRIDE  # scripted group (container) (typed FeaturePython)
  Dunit = g/cm3
  Dvalue = 0.82
  Group = -> [Li_element004,H_element050]
  conduct = 2
  density = 1
  expand = 3
  formula = G4_LITHIUM_HYDRIDE
  name = G4_LITHIUM_HYDRIDE
  specific = 4
FEATURE [App::DocumentObjectGroupPython] Li_element005  label="Li_element : 005"  # scripted group (container) (typed FeaturePython)
  n = 1
  ref = Li_element
FEATURE [App::DocumentObjectGroupPython] I_element003  label="I_element : 002"  # scripted group (container) (typed FeaturePython)
  n = 1
  ref = I_element
FEATURE [App::DocumentObjectGroupPython] G4_LITHIUM_IODIDE  # scripted group (container) (typed FeaturePython)
  Dunit = g/cm3
  Dvalue = 3.494
  Group = -> [Li_element005,I_element003]
  conduct = 2
  density = 1
  expand = 3
  formula = G4_LITHIUM_IODIDE
  name = G4_LITHIUM_IODIDE
  specific = 4
FEATURE [App::DocumentObjectGroupPython] Li_element006  label="Li_element : 006"  # scripted group (container) (typed FeaturePython)
  n = 2
  ref = Li_element
FEATURE [App::DocumentObjectGroupPython] O_element055  label="O_element : 029"  # scripted group (container) (typed FeaturePython)
  n = 1
  ref = O_element
FEATURE [App::DocumentObjectGroupPython] G4_LITHIUM_OXIDE  # scripted group (container) (typed FeaturePython)
  Dunit = g/cm3
  Dvalue = 2.013
  Group = -> [Li_element006,O_element055]
  conduct = 2
  density = 1
  expand = 3
  formula = G4_LITHIUM_OXIDE
  name = G4_LITHIUM_OXIDE
  specific = 4
FEATURE [App::DocumentObjectGroupPython] Li_element007  label="Li_element : 007"  # scripted group (container) (typed FeaturePython)
  n = 2
  ref = Li_element
FEATURE [App::DocumentObjectGroupPython] B_element005  label="B_element : 005"  # scripted group (container) (typed FeaturePython)
  n = 4
  ref = B_element
FEATURE [App::DocumentObjectGroupPython] O_element056  label="O_element : 7"  # scripted group (container) (typed FeaturePython)
  n = 7
  ref = O_element
FEATURE [App::DocumentObjectGroupPython] G4_LITHIUM_TETRABORATE  # scripted group (container) (typed FeaturePython)
  Dunit = g/cm3
  Dvalue = 2.44
  Group = -> [Li_element007,B_element005,O_element056]
  conduct = 2
  density = 1
  expand = 3
  formula = G4_LITHIUM_TETRABORATE
  name = G4_LITHIUM_TETRABORATE
  specific = 4
FEATURE [App::DocumentObjectGroupPython] H_element051  label="H_element : 0.105"  # scripted group (container) (typed FeaturePython)
  n = 0.105
FEATURE [App::DocumentObjectGroupPython] C_element056  label="C_element : 0.083"  # scripted group (container) (typed FeaturePython)
  n = 0.083
FEATURE [App::DocumentObjectGroupPython] N_element023  label="N_element : 0.023"  # scripted group (container) (typed FeaturePython)
  n = 0.023
FEATURE [App::DocumentObjectGroupPython] O_element057  label="O_element : 0.779"  # scripted group (container) (typed FeaturePython)
  n = 0.779
FEATURE [App::DocumentObjectGroupPython] Na_element010  label="Na_element : 0.097"  # scripted group (container) (typed FeaturePython)
  n = 0.002
FEATURE [App::DocumentObjectGroupPython] P_element006  label="P_element : 0.105"  # scripted group (container) (typed FeaturePython)
  n = 0.001
FEATURE [App::DocumentObjectGroupPython] S_element016  label="S_element : 0.017"  # scripted group (container) (typed FeaturePython)
  n = 0.002
FEATURE [App::DocumentObjectGroupPython] Cl_element014  label="Cl_element : 0.587"  # scripted group (container) (typed FeaturePython)
  n = 0.003
FEATURE [App::DocumentObjectGroupPython] K_element005  label="K_element : 0.015"  # scripted group (container) (typed FeaturePython)
  n = 0.002
FEATURE [App::DocumentObjectGroupPython] G4_LUNG_ICRP  # scripted group (container) (typed FeaturePython)
  Dunit = g/cm3
  Dvalue = 1.04
  Group = -> [H_element051,C_element056,N_element023,O_element057,Na_element010,P_element006,S_element016,Cl_element014,K_element005]
  conduct = 2
  density = 1
  expand = 3
  formula = G4_LUNG_ICRP
  name = G4_LUNG_ICRP
  specific = 4
FEATURE [App::DocumentObjectGroupPython] H_element052  label="H_element : 0.116"  # scripted group (container) (typed FeaturePython)
  n = 0.114318
FEATURE [App::DocumentObjectGroupPython] C_element057  label="C_element : 0.656"  # scripted group (container) (typed FeaturePython)
  n = 0.655824
FEATURE [App::DocumentObjectGroupPython] O_element058  label="O_element : 0.092"  # scripted group (container) (typed FeaturePython)
  n = 0.0921831
FEATURE [App::DocumentObjectGroupPython] Mg_element004  label="Mg_element : 0.135"  # scripted group (container) (typed FeaturePython)
  n = 0.134792
FEATURE [App::DocumentObjectGroupPython] Ca_element013  label="Ca_element : 0.003"  # scripted group (container) (typed FeaturePython)
  n = 0.002883
FEATURE [App::DocumentObjectGroupPython] G4_M3_WAX  # scripted group (container) (typed FeaturePython)
  Dunit = g/cm3
  Dvalue = 1.05
  Group = -> [H_element052,C_element057,O_element058,Mg_element004,Ca_element013]
  conduct = 2
  density = 1
  expand = 3
  formula = G4_M3_WAX
  name = G4_M3_WAX
  specific = 4
FEATURE [App::DocumentObjectGroupPython] Mg_element005  label="Mg_element : 1"  # scripted group (container) (typed FeaturePython)
  n = 1
  ref = Mg_element
FEATURE [App::DocumentObjectGroupPython] C_element058  label="C_element : 031"  # scripted group (container) (typed FeaturePython)
  n = 1
  ref = C_element
FEATURE [App::DocumentObjectGroupPython] O_element059  label="O_element : 030"  # scripted group (container) (typed FeaturePython)
  n = 3
  ref = O_element
FEATURE [App::DocumentObjectGroupPython] G4_MAGNESIUM_CARBONATE  # scripted group (container) (typed FeaturePython)
  Dunit = g/cm3
  Dvalue = 2.958
  Group = -> [Mg_element005,C_element058,O_element059]
  conduct = 2
  density = 1
  expand = 3
  formula = G4_MAGNESIUM_CARBONATE
  name = G4_MAGNESIUM_CARBONATE
  specific = 4
FEATURE [App::DocumentObjectGroupPython] Mg_element006  label="Mg_element : 002"  # scripted group (container) (typed FeaturePython)
  n = 1
  ref = Mg_element
FEATURE [App::DocumentObjectGroupPython] F_element013  label="F_element : 005"  # scripted group (container) (typed FeaturePython)
  n = 2
  ref = F_element
FEATURE [App::DocumentObjectGroupPython] G4_MAGNESIUM_FLUORIDE  # scripted group (container) (typed FeaturePython)
  Dunit = g/cm3
  Dvalue = 3
  Group = -> [Mg_element006,F_element013]
  conduct = 2
  density = 1
  expand = 3
  formula = G4_MAGNESIUM_FLUORIDE
  name = G4_MAGNESIUM_FLUORIDE
  specific = 4
FEATURE [App::DocumentObjectGroupPython] Mg_element007  label="Mg_element : 003"  # scripted group (container) (typed FeaturePython)
  n = 1
  ref = Mg_element
FEATURE [App::DocumentObjectGroupPython] O_element060  label="O_element : 031"  # scripted group (container) (typed FeaturePython)
  n = 1
  ref = O_element
FEATURE [App::DocumentObjectGroupPython] G4_MAGNESIUM_OXIDE  # scripted group (container) (typed FeaturePython)
  Dunit = g/cm3
  Dvalue = 3.58
  Group = -> [Mg_element007,O_element060]
  conduct = 2
  density = 1
  expand = 3
  formula = G4_MAGNESIUM_OXIDE
  name = G4_MAGNESIUM_OXIDE
  specific = 4
FEATURE [App::DocumentObjectGroupPython] Mg_element008  label="Mg_element : 004"  # scripted group (container) (typed FeaturePython)
  n = 1
  ref = Mg_element
FEATURE [App::DocumentObjectGroupPython] B_element006  label="B_element : 006"  # scripted group (container) (typed FeaturePython)
  n = 4
  ref = B_element
FEATURE [App::DocumentObjectGroupPython] O_element061  label="O_element : 032"  # scripted group (container) (typed FeaturePython)
  n = 7
  ref = O_element
FEATURE [App::DocumentObjectGroupPython] G4_MAGNESIUM_TETRABORATE  # scripted group (container) (typed FeaturePython)
  Dunit = g/cm3
  Dvalue = 2.53
  Group = -> [Mg_element008,B_element006,O_element061]
  conduct = 2
  density = 1
  expand = 3
  formula = G4_MAGNESIUM_TETRABORATE
  name = G4_MAGNESIUM_TETRABORATE
  specific = 4
FEATURE [App::DocumentObjectGroupPython] Hg_element001  label="Hg_element : 1"  # scripted group (container) (typed FeaturePython)
  n = 1
  ref = Hg_element
FEATURE [App::DocumentObjectGroupPython] I_element004  label="I_element : 2"  # scripted group (container) (typed FeaturePython)
  n = 2
  ref = I_element
FEATURE [App::DocumentObjectGroupPython] G4_MERCURIC_IODIDE  # scripted group (container) (typed FeaturePython)
  Dunit = g/cm3
  Dvalue = 6.36
  Group = -> [Hg_element001,I_element004]
  conduct = 2
  density = 1
  expand = 3
  formula = G4_MERCURIC_IODIDE
  name = G4_MERCURIC_IODIDE
  specific = 4
FEATURE [App::DocumentObjectGroupPython] C_element059  label="C_element : 032"  # scripted group (container) (typed FeaturePython)
  n = 1
  ref = C_element
FEATURE [App::DocumentObjectGroupPython] H_element053  label="H_element : 028"  # scripted group (container) (typed FeaturePython)
  n = 4
  ref = H_element
FEATURE [App::DocumentObjectGroupPython] G4_METHANE  # scripted group (container) (typed FeaturePython)
  Dunit = g/cm3
  Dvalue = 0.000667151
  Group = -> [C_element059,H_element053]
  conduct = 2
  density = 1
  expand = 3
  formula = G4_METHANE
  name = G4_METHANE
  specific = 4
FEATURE [App::DocumentObjectGroupPython] C_element060  label="C_element : 033"  # scripted group (container) (typed FeaturePython)
  n = 1
  ref = C_element
FEATURE [App::DocumentObjectGroupPython] H_element054  label="H_element : 029"  # scripted group (container) (typed FeaturePython)
  n = 4
  ref = H_element
FEATURE [App::DocumentObjectGroupPython] O_element062  label="O_element : 033"  # scripted group (container) (typed FeaturePython)
  n = 1
  ref = O_element
FEATURE [App::DocumentObjectGroupPython] G4_METHANOL  # scripted group (container) (typed FeaturePython)
  Dunit = g/cm3
  Dvalue = 0.7914
  Group = -> [C_element060,H_element054,O_element062]
  conduct = 2
  density = 1
  expand = 3
  formula = G4_METHANOL
  name = G4_METHANOL
  specific = 4
FEATURE [App::DocumentObjectGroupPython] H_element055  label="H_element : 0.134"  # scripted group (container) (typed FeaturePython)
  n = 0.13404
FEATURE [App::DocumentObjectGroupPython] C_element061  label="C_element : 0.778"  # scripted group (container) (typed FeaturePython)
  n = 0.77796
FEATURE [App::DocumentObjectGroupPython] O_element063  label="O_element : 0.035"  # scripted group (container) (typed FeaturePython)
  n = 0.03502
FEATURE [App::DocumentObjectGroupPython] Mg_element009  label="Mg_element : 0.039"  # scripted group (container) (typed FeaturePython)
  n = 0.038594
FEATURE [App::DocumentObjectGroupPython] Ti_element002  label="Ti_element : 0.014"  # scripted group (container) (typed FeaturePython)
  n = 0.014386
FEATURE [App::DocumentObjectGroupPython] G4_MIX_D_WAX  # scripted group (container) (typed FeaturePython)
  Dunit = g/cm3
  Dvalue = 0.99
  Group = -> [H_element055,C_element061,O_element063,Mg_element009,Ti_element002]
  conduct = 2
  density = 1
  expand = 3
  formula = G4_MIX_D_WAX
  name = G4_MIX_D_WAX
  specific = 4
FEATURE [App::DocumentObjectGroupPython] H_element056  label="H_element : 0.135"  # scripted group (container) (typed FeaturePython)
  n = 0.081192
FEATURE [App::DocumentObjectGroupPython] C_element062  label="C_element : 0.583"  # scripted group (container) (typed FeaturePython)
  n = 0.583442
FEATURE [App::DocumentObjectGroupPython] N_element024  label="N_element : 0.018"  # scripted group (container) (typed FeaturePython)
  n = 0.017798
FEATURE [App::DocumentObjectGroupPython] O_element064  label="O_element : 0.186"  # scripted group (container) (typed FeaturePython)
  n = 0.186381
FEATURE [App::DocumentObjectGroupPython] Mg_element010  label="Mg_element : 0.130"  # scripted group (container) (typed FeaturePython)
  n = 0.130287
FEATURE [App::DocumentObjectGroupPython] Cl_element015  label="Cl_element : 0.588"  # scripted group (container) (typed FeaturePython)
  n = 0.0009
FEATURE [App::DocumentObjectGroupPython] G4_MS20_TISSUE  # scripted group (container) (typed FeaturePython)
  Dunit = g/cm3
  Dvalue = 1
  Group = -> [H_element056,C_element062,N_element024,O_element064,Mg_element010,Cl_element015]
  conduct = 2
  density = 1
  expand = 3
  formula = G4_MS20_TISSUE
  name = G4_MS20_TISSUE
  specific = 4
FEATURE [App::DocumentObjectGroupPython] H_element057  label="H_element : 0.136"  # scripted group (container) (typed FeaturePython)
  n = 0.102
FEATURE [App::DocumentObjectGroupPython] C_element063  label="C_element : 0.143"  # scripted group (container) (typed FeaturePython)
  n = 0.143
FEATURE [App::DocumentObjectGroupPython] N_element025  label="N_element : 0.034"  # scripted group (container) (typed FeaturePython)
  n = 0.034
FEATURE [App::DocumentObjectGroupPython] O_element065  label="O_element : 0.710"  # scripted group (container) (typed FeaturePython)
  n = 0.71
FEATURE [App::DocumentObjectGroupPython] Na_element011  label="Na_element : 0.098"  # scripted group (container) (typed FeaturePython)
  n = 0.001
FEATURE [App::DocumentObjectGroupPython] P_element007  label="P_element : 0.002"  # scripted group (container) (typed FeaturePython)
  n = 0.002
FEATURE [App::DocumentObjectGroupPython] S_element017  label="S_element : 0.018"  # scripted group (container) (typed FeaturePython)
  n = 0.003
FEATURE [App::DocumentObjectGroupPython] Cl_element016  label="Cl_element : 0.589"  # scripted group (container) (typed FeaturePython)
  n = 0.001
FEATURE [App::DocumentObjectGroupPython] K_element006  label="K_element : 0.004"  # scripted group (container) (typed FeaturePython)
  n = 0.004
FEATURE [App::DocumentObjectGroupPython] G4_MUSCLE_SKELETAL_ICRP  # scripted group (container) (typed FeaturePython)
  Dunit = g/cm3
  Dvalue = 1.05
  Group = -> [H_element057,C_element063,N_element025,O_element065,Na_element011,P_element007,S_element017,Cl_element016,K_element006]
  conduct = 2
  density = 1
  expand = 3
  formula = G4_MUSCLE_SKELETAL_ICRP
  name = G4_MUSCLE_SKELETAL_ICRP
  specific = 4
FEATURE [App::DocumentObjectGroupPython] H_element058  label="H_element : 0.137"  # scripted group (container) (typed FeaturePython)
  n = 0.102102
FEATURE [App::DocumentObjectGroupPython] C_element064  label="C_element : 0.123"  # scripted group (container) (typed FeaturePython)
  n = 0.123123
FEATURE [App::DocumentObjectGroupPython] N_element026  label="N_element : 0.756"  # scripted group (container) (typed FeaturePython)
  n = 0.035035
FEATURE [App::DocumentObjectGroupPython] O_element066  label="O_element : 0.730"  # scripted group (container) (typed FeaturePython)
  n = 0.72973
FEATURE [App::DocumentObjectGroupPython] Na_element012  label="Na_element : 0.099"  # scripted group (container) (typed FeaturePython)
  n = 0.001001
FEATURE [App::DocumentObjectGroupPython] P_element008  label="P_element : 0.106"  # scripted group (container) (typed FeaturePython)
  n = 0.002002
FEATURE [App::DocumentObjectGroupPython] S_element018  label="S_element : 0.019"  # scripted group (container) (typed FeaturePython)
  n = 0.004004
FEATURE [App::DocumentObjectGroupPython] K_element007  label="K_element : 0.016"  # scripted group (container) (typed FeaturePython)
  n = 0.003003
FEATURE [App::DocumentObjectGroupPython] G4_MUSCLE_STRIATED_ICRU  # scripted group (container) (typed FeaturePython)
  Dunit = g/cm3
  Dvalue = 1.04
  Group = -> [H_element058,C_element064,N_element026,O_element066,Na_element012,P_element008,S_element018,K_element007]
  conduct = 2
  density = 1
  expand = 3
  formula = G4_MUSCLE_STRIATED_ICRU
  name = G4_MUSCLE_STRIATED_ICRU
  specific = 4
FEATURE [App::DocumentObjectGroupPython] H_element059  label="H_element : 0.098"  # scripted group (container) (typed FeaturePython)
  n = 0.0982341
FEATURE [App::DocumentObjectGroupPython] C_element065  label="C_element : 0.156"  # scripted group (container) (typed FeaturePython)
  n = 0.156214
FEATURE [App::DocumentObjectGroupPython] N_element027  label="N_element : 0.757"  # scripted group (container) (typed FeaturePython)
  n = 0.035451
FEATURE [App::DocumentObjectGroupPython] O_element067  label="O_element : 0.880"  # scripted group (container) (typed FeaturePython)
  n = 0.710101
FEATURE [App::DocumentObjectGroupPython] G4_MUSCLE_WITH_SUCROSE  # scripted group (container) (typed FeaturePython)
  Dunit = g/cm3
  Dvalue = 1.11
  Group = -> [H_element059,C_element065,N_element027,O_element067]
  conduct = 2
  density = 1
  expand = 3
  formula = G4_MUSCLE_WITH_SUCROSE
  name = G4_MUSCLE_WITH_SUCROSE
  specific = 4
FEATURE [App::DocumentObjectGroupPython] H_element060  label="H_element : 0.138"  # scripted group (container) (typed FeaturePython)
  n = 0.101969
FEATURE [App::DocumentObjectGroupPython] C_element066  label="C_element : 0.120"  # scripted group (container) (typed FeaturePython)
  n = 0.120058
FEATURE [App::DocumentObjectGroupPython] N_element028  label="N_element : 0.758"  # scripted group (container) (typed FeaturePython)
  n = 0.035451
FEATURE [App::DocumentObjectGroupPython] O_element068  label="O_element : 0.743"  # scripted group (container) (typed FeaturePython)
  n = 0.742522
FEATURE [App::DocumentObjectGroupPython] G4_MUSCLE_WITHOUT_SUCROSE  # scripted group (container) (typed FeaturePython)
  Dunit = g/cm3
  Dvalue = 1.07
  Group = -> [H_element060,C_element066,N_element028,O_element068]
  conduct = 2
  density = 1
  expand = 3
  formula = G4_MUSCLE_WITHOUT_SUCROSE
  name = G4_MUSCLE_WITHOUT_SUCROSE
  specific = 4
FEATURE [App::DocumentObjectGroupPython] C_element067  label="C_element : 10"  # scripted group (container) (typed FeaturePython)
  n = 10
  ref = C_element
FEATURE [App::DocumentObjectGroupPython] H_element061  label="H_element : 030"  # scripted group (container) (typed FeaturePython)
  n = 8
  ref = H_element
FEATURE [App::DocumentObjectGroupPython] G4_NAPHTHALENE  # scripted group (container) (typed FeaturePython)
  Dunit = g/cm3
  Dvalue = 1.145
  Group = -> [C_element067,H_element061]
  conduct = 2
  density = 1
  expand = 3
  formula = G4_NAPHTHALENE
  name = G4_NAPHTHALENE
  specific = 4
FEATURE [App::DocumentObjectGroupPython] C_element068  label="C_element : 034"  # scripted group (container) (typed FeaturePython)
  n = 6
  ref = C_element
FEATURE [App::DocumentObjectGroupPython] H_element062  label="H_element : 031"  # scripted group (container) (typed FeaturePython)
  n = 5
  ref = H_element
FEATURE [App::DocumentObjectGroupPython] N_element029  label="N_element : 012"  # scripted group (container) (typed FeaturePython)
  n = 1
  ref = N_element
FEATURE [App::DocumentObjectGroupPython] O_element069  label="O_element : 034"  # scripted group (container) (typed FeaturePython)
  n = 2
  ref = O_element
FEATURE [App::DocumentObjectGroupPython] G4_NITROBENZENE  # scripted group (container) (typed FeaturePython)
  Dunit = g/cm3
  Dvalue = 1.19867
  Group = -> [C_element068,H_element062,N_element029,O_element069]
  conduct = 2
  density = 1
  expand = 3
  formula = G4_NITROBENZENE
  name = G4_NITROBENZENE
  specific = 4
FEATURE [App::DocumentObjectGroupPython] N_element030  label="N_element : 013"  # scripted group (container) (typed FeaturePython)
  n = 2
  ref = N_element
FEATURE [App::DocumentObjectGroupPython] O_element070  label="O_element : 035"  # scripted group (container) (typed FeaturePython)
  n = 1
  ref = O_element
FEATURE [App::DocumentObjectGroupPython] G4_NITROUS_OXIDE  # scripted group (container) (typed FeaturePython)
  Dunit = g/cm3
  Dvalue = 0.00183094
  Group = -> [N_element030,O_element070]
  conduct = 2
  density = 1
  expand = 3
  formula = G4_NITROUS_OXIDE
  name = G4_NITROUS_OXIDE
  specific = 4
FEATURE [App::DocumentObjectGroupPython] H_element063  label="H_element : 0.104"  # scripted group (container) (typed FeaturePython)
  n = 0.103509
FEATURE [App::DocumentObjectGroupPython] C_element069  label="C_element : 0.648"  # scripted group (container) (typed FeaturePython)
  n = 0.648416
FEATURE [App::DocumentObjectGroupPython] N_element031  label="N_element : 0.100"  # scripted group (container) (typed FeaturePython)
  n = 0.0995361
FEATURE [App::DocumentObjectGroupPython] O_element071  label="O_element : 0.149"  # scripted group (container) (typed FeaturePython)
  n = 0.148539
FEATURE [App::DocumentObjectGroupPython] G4_NYLON_8062  label="G4_NYLON-8062"  # scripted group (container) (typed FeaturePython)
  Dunit = g/cm3
  Dvalue = 1.08
  Group = -> [H_element063,C_element069,N_element031,O_element071]
  conduct = 2
  density = 1
  expand = 3
  formula = G4_NYLON-8062
  name = G4_NYLON-8062
  specific = 4
FEATURE [App::DocumentObjectGroupPython] C_element070  label="C_element : 035"  # scripted group (container) (typed FeaturePython)
  n = 6
  ref = C_element
FEATURE [App::DocumentObjectGroupPython] H_element064  label="H_element : 11"  # scripted group (container) (typed FeaturePython)
  n = 11
  ref = H_element
FEATURE [App::DocumentObjectGroupPython] N_element032  label="N_element : 014"  # scripted group (container) (typed FeaturePython)
  n = 1
  ref = N_element
FEATURE [App::DocumentObjectGroupPython] O_element072  label="O_element : 036"  # scripted group (container) (typed FeaturePython)
  n = 1
  ref = O_element
FEATURE [App::DocumentObjectGroupPython] G4_NYLON_6_6  label="G4_NYLON-6-6"  # scripted group (container) (typed FeaturePython)
  Dunit = g/cm3
  Dvalue = 1.14
  Group = -> [C_element070,H_element064,N_element032,O_element072]
  conduct = 2
  density = 1
  expand = 3
  formula = G4_NYLON-6-6
  name = G4_NYLON-6-6
  specific = 4
FEATURE [App::DocumentObjectGroupPython] H_element065  label="H_element : 0.139"  # scripted group (container) (typed FeaturePython)
  n = 0.107062
FEATURE [App::DocumentObjectGroupPython] C_element071  label="C_element : 0.680"  # scripted group (container) (typed FeaturePython)
  n = 0.680449
FEATURE [App::DocumentObjectGroupPython] N_element033  label="N_element : 0.099"  # scripted group (container) (typed FeaturePython)
  n = 0.099189
FEATURE [App::DocumentObjectGroupPython] O_element073  label="O_element : 0.113"  # scripted group (container) (typed FeaturePython)
  n = 0.1133
FEATURE [App::DocumentObjectGroupPython] G4_NYLON_6_10  label="G4_NYLON-6-10"  # scripted group (container) (typed FeaturePython)
  Dunit = g/cm3
  Dvalue = 1.14
  Group = -> [H_element065,C_element071,N_element033,O_element073]
  conduct = 2
  density = 1
  expand = 3
  formula = G4_NYLON-6-10
  name = G4_NYLON-6-10
  specific = 4
FEATURE [App::DocumentObjectGroupPython] H_element066  label="H_element : 0.140"  # scripted group (container) (typed FeaturePython)
  n = 0.115476
FEATURE [App::DocumentObjectGroupPython] C_element072  label="C_element : 0.721"  # scripted group (container) (typed FeaturePython)
  n = 0.720818
FEATURE [App::DocumentObjectGroupPython] N_element034  label="N_element : 0.076"  # scripted group (container) (typed FeaturePython)
  n = 0.0764169
FEATURE [App::DocumentObjectGroupPython] O_element074  label="O_element : 0.087"  # scripted group (container) (typed FeaturePython)
  n = 0.0872889
FEATURE [App::DocumentObjectGroupPython] G4_NYLON_11_RILSAN  label="G4_NYLON-11_RILSAN"  # scripted group (container) (typed FeaturePython)
  Dunit = g/cm3
  Dvalue = 1.425
  Group = -> [H_element066,C_element072,N_element034,O_element074]
  conduct = 2
  density = 1
  expand = 3
  formula = G4_NYLON-11_RILSAN
  name = G4_NYLON-11_RILSAN
  specific = 4
FEATURE [App::DocumentObjectGroupPython] C_element073  label="C_element : 8"  # scripted group (container) (typed FeaturePython)
  n = 8
  ref = C_element
FEATURE [App::DocumentObjectGroupPython] H_element067  label="H_element : 18"  # scripted group (container) (typed FeaturePython)
  n = 18
  ref = H_element
FEATURE [App::DocumentObjectGroupPython] G4_OCTANE  # scripted group (container) (typed FeaturePython)
  Dunit = g/cm3
  Dvalue = 0.7026
  Group = -> [C_element073,H_element067]
  conduct = 2
  density = 1
  expand = 3
  formula = G4_OCTANE
  name = G4_OCTANE
  specific = 4
FEATURE [App::DocumentObjectGroupPython] C_element074  label="C_element : 25"  # scripted group (container) (typed FeaturePython)
  n = 25
  ref = C_element
FEATURE [App::DocumentObjectGroupPython] H_element068  label="H_element : 52"  # scripted group (container) (typed FeaturePython)
  n = 52
  ref = H_element
FEATURE [App::DocumentObjectGroupPython] G4_PARAFFIN  # scripted group (container) (typed FeaturePython)
  Dunit = g/cm3
  Dvalue = 0.93
  Group = -> [C_element074,H_element068]
  conduct = 2
  density = 1
  expand = 3
  formula = G4_PARAFFIN
  name = G4_PARAFFIN
  specific = 4
FEATURE [App::DocumentObjectGroupPython] C_element075  label="C_element : 036"  # scripted group (container) (typed FeaturePython)
  n = 5
  ref = C_element
FEATURE [App::DocumentObjectGroupPython] H_element069  label="H_element : 032"  # scripted group (container) (typed FeaturePython)
  n = 12
  ref = H_element
FEATURE [App::DocumentObjectGroupPython] G4_N_PENTANE  label="G4_N-PENTANE"  # scripted group (container) (typed FeaturePython)
  Dunit = g/cm3
  Dvalue = 0.6262
  Group = -> [C_element075,H_element069]
  conduct = 2
  density = 1
  expand = 3
  formula = G4_N-PENTANE
  name = G4_N-PENTANE
  specific = 4
FEATURE [App::DocumentObjectGroupPython] H_element070  label="H_element : 0.014"  # scripted group (container) (typed FeaturePython)
  n = 0.0141
FEATURE [App::DocumentObjectGroupPython] C_element076  label="C_element : 0.072"  # scripted group (container) (typed FeaturePython)
  n = 0.072261
FEATURE [App::DocumentObjectGroupPython] N_element035  label="N_element : 0.019"  # scripted group (container) (typed FeaturePython)
  n = 0.01932
FEATURE [App::DocumentObjectGroupPython] O_element075  label="O_element : 0.066"  # scripted group (container) (typed FeaturePython)
  n = 0.066101
FEATURE [App::DocumentObjectGroupPython] S_element019  label="S_element : 0.020"  # scripted group (container) (typed FeaturePython)
  n = 0.00189
FEATURE [App::DocumentObjectGroupPython] Br_element004  label="Br_element : 0.349"  # scripted group (container) (typed FeaturePython)
  n = 0.349103
FEATURE [App::DocumentObjectGroupPython] Ag_element001  label="Ag_element : 0.474"  # scripted group (container) (typed FeaturePython)
  n = 0.474105
FEATURE [App::DocumentObjectGroupPython] I_element005  label="I_element : 0.003"  # scripted group (container) (typed FeaturePython)
  n = 0.00312
FEATURE [App::DocumentObjectGroupPython] G4_PHOTO_EMULSION  # scripted group (container) (typed FeaturePython)
  Dunit = g/cm3
  Dvalue = 3.815
  Group = -> [H_element070,C_element076,N_element035,O_element075,S_element019,Br_element004,Ag_element001,I_element005]
  conduct = 2
  density = 1
  expand = 3
  formula = G4_PHOTO_EMULSION
  name = G4_PHOTO_EMULSION
  specific = 4
FEATURE [App::DocumentObjectGroupPython] C_element077  label="C_element : 9"  # scripted group (container) (typed FeaturePython)
  n = 9
  ref = C_element
FEATURE [App::DocumentObjectGroupPython] H_element071  label="H_element : 033"  # scripted group (container) (typed FeaturePython)
  n = 10
  ref = H_element
FEATURE [App::DocumentObjectGroupPython] G4_PLASTIC_SC_VINYLTOLUENE  # scripted group (container) (typed FeaturePython)
  Dunit = g/cm3
  Dvalue = 1.032
  Group = -> [C_element077,H_element071]
  conduct = 2
  density = 1
  expand = 3
  formula = G4_PLASTIC_SC_VINYLTOLUENE
  name = G4_PLASTIC_SC_VINYLTOLUENE
  specific = 4
FEATURE [App::DocumentObjectGroupPython] Pu_element001  label="Pu_element : 1"  # scripted group (container) (typed FeaturePython)
  n = 1
  ref = Pu_element
FEATURE [App::DocumentObjectGroupPython] O_element076  label="O_element : 037"  # scripted group (container) (typed FeaturePython)
  n = 2
  ref = O_element
FEATURE [App::DocumentObjectGroupPython] G4_PLUTONIUM_DIOXIDE  # scripted group (container) (typed FeaturePython)
  Dunit = g/cm3
  Dvalue = 11.46
  Group = -> [Pu_element001,O_element076]
  conduct = 2
  density = 1
  expand = 3
  formula = G4_PLUTONIUM_DIOXIDE
  name = G4_PLUTONIUM_DIOXIDE
  specific = 4
FEATURE [App::DocumentObjectGroupPython] C_element078  label="C_element : 037"  # scripted group (container) (typed FeaturePython)
  n = 3
  ref = C_element
FEATURE [App::DocumentObjectGroupPython] H_element072  label="H_element : 034"  # scripted group (container) (typed FeaturePython)
  n = 3
  ref = H_element
FEATURE [App::DocumentObjectGroupPython] N_element036  label="N_element : 015"  # scripted group (container) (typed FeaturePython)
  n = 1
  ref = N_element
FEATURE [App::DocumentObjectGroupPython] G4_POLYACRYLONITRILE  # scripted group (container) (typed FeaturePython)
  Dunit = g/cm3
  Dvalue = 1.17
  Group = -> [C_element078,H_element072,N_element036]
  conduct = 2
  density = 1
  expand = 3
  formula = G4_POLYACRYLONITRILE
  name = G4_POLYACRYLONITRILE
  specific = 4
FEATURE [App::DocumentObjectGroupPython] C_element079  label="C_element : 16"  # scripted group (container) (typed FeaturePython)
  n = 16
  ref = C_element
FEATURE [App::DocumentObjectGroupPython] H_element073  label="H_element : 035"  # scripted group (container) (typed FeaturePython)
  n = 14
  ref = H_element
FEATURE [App::DocumentObjectGroupPython] O_element077  label="O_element : 038"  # scripted group (container) (typed FeaturePython)
  n = 3
  ref = O_element
FEATURE [App::DocumentObjectGroupPython] G4_POLYCARBONATE  # scripted group (container) (typed FeaturePython)
  Dunit = g/cm3
  Dvalue = 1.2
  Group = -> [C_element079,H_element073,O_element077]
  conduct = 2
  density = 1
  expand = 3
  formula = G4_POLYCARBONATE
  name = G4_POLYCARBONATE
  specific = 4
FEATURE [App::DocumentObjectGroupPython] C_element080  label="C_element : 038"  # scripted group (container) (typed FeaturePython)
  n = 8
  ref = C_element
FEATURE [App::DocumentObjectGroupPython] H_element074  label="H_element : 036"  # scripted group (container) (typed FeaturePython)
  n = 7
  ref = H_element
FEATURE [App::DocumentObjectGroupPython] Cl_element017  label="Cl_element : 007"  # scripted group (container) (typed FeaturePython)
  n = 1
  ref = Cl_element
FEATURE [App::DocumentObjectGroupPython] G4_POLYCHLOROSTYRENE  # scripted group (container) (typed FeaturePython)
  Dunit = g/cm3
  Dvalue = 1.3
  Group = -> [C_element080,H_element074,Cl_element017]
  conduct = 2
  density = 1
  expand = 3
  formula = G4_POLYCHLOROSTYRENE
  name = G4_POLYCHLOROSTYRENE
  specific = 4
FEATURE [App::DocumentObjectGroupPython] C_element081  label="C_element : 039"  # scripted group (container) (typed FeaturePython)
  n = 1
  ref = C_element
FEATURE [App::DocumentObjectGroupPython] H_element075  label="H_element : 037"  # scripted group (container) (typed FeaturePython)
  n = 2
  ref = H_element
FEATURE [App::DocumentObjectGroupPython] G4_POLYETHYLENE  # scripted group (container) (typed FeaturePython)
  Dunit = g/cm3
  Dvalue = 0.94
  Group = -> [C_element081,H_element075]
  conduct = 2
  density = 1
  expand = 3
  formula = G4_POLYETHYLENE
  name = G4_POLYETHYLENE
  specific = 4
FEATURE [App::DocumentObjectGroupPython] C_element082  label="C_element : 040"  # scripted group (container) (typed FeaturePython)
  n = 10
  ref = C_element
FEATURE [App::DocumentObjectGroupPython] H_element076  label="H_element : 038"  # scripted group (container) (typed FeaturePython)
  n = 8
  ref = H_element
FEATURE [App::DocumentObjectGroupPython] O_element078  label="O_element : 039"  # scripted group (container) (typed FeaturePython)
  n = 4
  ref = O_element
FEATURE [App::DocumentObjectGroupPython] G4_MYLAR  # scripted group (container) (typed FeaturePython)
  Dunit = g/cm3
  Dvalue = 1.4
  Group = -> [C_element082,H_element076,O_element078]
  conduct = 2
  density = 1
  expand = 3
  formula = G4_MYLAR
  name = G4_MYLAR
  specific = 4
FEATURE [App::DocumentObjectGroupPython] C_element083  label="C_element : 041"  # scripted group (container) (typed FeaturePython)
  n = 5
  ref = C_element
FEATURE [App::DocumentObjectGroupPython] H_element077  label="H_element : 039"  # scripted group (container) (typed FeaturePython)
  n = 8
  ref = H_element
FEATURE [App::DocumentObjectGroupPython] O_element079  label="O_element : 040"  # scripted group (container) (typed FeaturePython)
  n = 2
  ref = O_element
FEATURE [App::DocumentObjectGroupPython] G4_PLEXIGLASS  # scripted group (container) (typed FeaturePython)
  Dunit = g/cm3
  Dvalue = 1.19
  Group = -> [C_element083,H_element077,O_element079]
  conduct = 2
  density = 1
  expand = 3
  formula = G4_PLEXIGLASS
  name = G4_PLEXIGLASS
  specific = 4
FEATURE [App::DocumentObjectGroupPython] C_element084  label="C_element : 042"  # scripted group (container) (typed FeaturePython)
  n = 1
  ref = C_element
FEATURE [App::DocumentObjectGroupPython] H_element078  label="H_element : 040"  # scripted group (container) (typed FeaturePython)
  n = 2
  ref = H_element
FEATURE [App::DocumentObjectGroupPython] O_element080  label="O_element : 041"  # scripted group (container) (typed FeaturePython)
  n = 1
  ref = O_element
FEATURE [App::DocumentObjectGroupPython] G4_POLYOXYMETHYLENE  # scripted group (container) (typed FeaturePython)
  Dunit = g/cm3
  Dvalue = 1.425
  Group = -> [C_element084,H_element078,O_element080]
  conduct = 2
  density = 1
  expand = 3
  formula = G4_POLYOXYMETHYLENE
  name = G4_POLYOXYMETHYLENE
  specific = 4
FEATURE [App::DocumentObjectGroupPython] C_element085  label="C_element : 043"  # scripted group (container) (typed FeaturePython)
  n = 2
  ref = C_element
FEATURE [App::DocumentObjectGroupPython] H_element079  label="H_element : 041"  # scripted group (container) (typed FeaturePython)
  n = 4
  ref = H_element
FEATURE [App::DocumentObjectGroupPython] G4_POLYPROPYLENE  # scripted group (container) (typed FeaturePython)
  Dunit = g/cm3
  Dvalue = 0.9
  Group = -> [C_element085,H_element079]
  conduct = 2
  density = 1
  expand = 3
  formula = G4_POLYPROPYLENE
  name = G4_POLYPROPYLENE
  specific = 4
FEATURE [App::DocumentObjectGroupPython] C_element086  label="C_element : 044"  # scripted group (container) (typed FeaturePython)
  n = 8
  ref = C_element
FEATURE [App::DocumentObjectGroupPython] H_element080  label="H_element : 042"  # scripted group (container) (typed FeaturePython)
  n = 8
  ref = H_element
FEATURE [App::DocumentObjectGroupPython] G4_POLYSTYRENE  # scripted group (container) (typed FeaturePython)
  Dunit = g/cm3
  Dvalue = 1.06
  Group = -> [C_element086,H_element080]
  conduct = 2
  density = 1
  expand = 3
  formula = G4_POLYSTYRENE
  name = G4_POLYSTYRENE
  specific = 4
FEATURE [App::DocumentObjectGroupPython] C_element087  label="C_element : 045"  # scripted group (container) (typed FeaturePython)
  n = 2
  ref = C_element
FEATURE [App::DocumentObjectGroupPython] F_element014  label="F_element : 4"  # scripted group (container) (typed FeaturePython)
  n = 4
  ref = F_element
FEATURE [App::DocumentObjectGroupPython] G4_TEFLON  # scripted group (container) (typed FeaturePython)
  Dunit = g/cm3
  Dvalue = 2.2
  Group = -> [C_element087,F_element014]
  conduct = 2
  density = 1
  expand = 3
  formula = G4_TEFLON
  name = G4_TEFLON
  specific = 4
FEATURE [App::DocumentObjectGroupPython] C_element088  label="C_element : 046"  # scripted group (container) (typed FeaturePython)
  n = 2
  ref = C_element
FEATURE [App::DocumentObjectGroupPython] F_element015  label="F_element : 006"  # scripted group (container) (typed FeaturePython)
  n = 3
  ref = F_element
FEATURE [App::DocumentObjectGroupPython] Cl_element018  label="Cl_element : 008"  # scripted group (container) (typed FeaturePython)
  n = 1
  ref = Cl_element
FEATURE [App::DocumentObjectGroupPython] G4_POLYTRIFLUOROCHLOROETHYLENE  # scripted group (container) (typed FeaturePython)
  Dunit = g/cm3
  Dvalue = 2.1
  Group = -> [C_element088,F_element015,Cl_element018]
  conduct = 2
  density = 1
  expand = 3
  formula = G4_POLYTRIFLUOROCHLOROETHYLENE
  name = G4_POLYTRIFLUOROCHLOROETHYLENE
  specific = 4
FEATURE [App::DocumentObjectGroupPython] C_element089  label="C_element : 047"  # scripted group (container) (typed FeaturePython)
  n = 4
  ref = C_element
FEATURE [App::DocumentObjectGroupPython] H_element081  label="H_element : 043"  # scripted group (container) (typed FeaturePython)
  n = 6
  ref = H_element
FEATURE [App::DocumentObjectGroupPython] O_element081  label="O_element : 042"  # scripted group (container) (typed FeaturePython)
  n = 2
  ref = O_element
FEATURE [App::DocumentObjectGroupPython] G4_POLYVINYL_ACETATE  # scripted group (container) (typed FeaturePython)
  Dunit = g/cm3
  Dvalue = 1.19
  Group = -> [C_element089,H_element081,O_element081]
  conduct = 2
  density = 1
  expand = 3
  formula = G4_POLYVINYL_ACETATE
  name = G4_POLYVINYL_ACETATE
  specific = 4
FEATURE [App::DocumentObjectGroupPython] C_element090  label="C_element : 048"  # scripted group (container) (typed FeaturePython)
  n = 2
  ref = C_element
FEATURE [App::DocumentObjectGroupPython] H_element082  label="H_element : 044"  # scripted group (container) (typed FeaturePython)
  n = 4
  ref = H_element
FEATURE [App::DocumentObjectGroupPython] O_element082  label="O_element : 043"  # scripted group (container) (typed FeaturePython)
  n = 1
  ref = O_element
FEATURE [App::DocumentObjectGroupPython] G4_POLYVINYL_ALCOHOL  # scripted group (container) (typed FeaturePython)
  Dunit = g/cm3
  Dvalue = 1.3
  Group = -> [C_element090,H_element082,O_element082]
  conduct = 2
  density = 1
  expand = 3
  formula = G4_POLYVINYL_ALCOHOL
  name = G4_POLYVINYL_ALCOHOL
  specific = 4
FEATURE [App::DocumentObjectGroupPython] C_element091  label="C_element : 049"  # scripted group (container) (typed FeaturePython)
  n = 8
  ref = C_element
FEATURE [App::DocumentObjectGroupPython] H_element083  label="H_element : 045"  # scripted group (container) (typed FeaturePython)
  n = 14
  ref = H_element
FEATURE [App::DocumentObjectGroupPython] O_element083  label="O_element : 044"  # scripted group (container) (typed FeaturePython)
  n = 2
  ref = O_element
FEATURE [App::DocumentObjectGroupPython] G4_POLYVINYL_BUTYRAL  # scripted group (container) (typed FeaturePython)
  Dunit = g/cm3
  Dvalue = 1.12
  Group = -> [C_element091,H_element083,O_element083]
  conduct = 2
  density = 1
  expand = 3
  formula = G4_POLYVINYL_BUTYRAL
  name = G4_POLYVINYL_BUTYRAL
  specific = 4
FEATURE [App::DocumentObjectGroupPython] C_element092  label="C_element : 050"  # scripted group (container) (typed FeaturePython)
  n = 2
  ref = C_element
FEATURE [App::DocumentObjectGroupPython] H_element084  label="H_element : 046"  # scripted group (container) (typed FeaturePython)
  n = 3
  ref = H_element
FEATURE [App::DocumentObjectGroupPython] Cl_element019  label="Cl_element : 009"  # scripted group (container) (typed FeaturePython)
  n = 1
  ref = Cl_element
FEATURE [App::DocumentObjectGroupPython] G4_POLYVINYL_CHLORIDE  # scripted group (container) (typed FeaturePython)
  Dunit = g/cm3
  Dvalue = 1.3
  Group = -> [C_element092,H_element084,Cl_element019]
  conduct = 2
  density = 1
  expand = 3
  formula = G4_POLYVINYL_CHLORIDE
  name = G4_POLYVINYL_CHLORIDE
  specific = 4
FEATURE [App::DocumentObjectGroupPython] C_element093  label="C_element : 051"  # scripted group (container) (typed FeaturePython)
  n = 2
  ref = C_element
FEATURE [App::DocumentObjectGroupPython] H_element085  label="H_element : 047"  # scripted group (container) (typed FeaturePython)
  n = 2
  ref = H_element
FEATURE [App::DocumentObjectGroupPython] Cl_element020  label="Cl_element : 010"  # scripted group (container) (typed FeaturePython)
  n = 2
  ref = Cl_element
FEATURE [App::DocumentObjectGroupPython] G4_POLYVINYLIDENE_CHLORIDE  # scripted group (container) (typed FeaturePython)
  Dunit = g/cm3
  Dvalue = 1.7
  Group = -> [C_element093,H_element085,Cl_element020]
  conduct = 2
  density = 1
  expand = 3
  formula = G4_POLYVINYLIDENE_CHLORIDE
  name = G4_POLYVINYLIDENE_CHLORIDE
  specific = 4
FEATURE [App::DocumentObjectGroupPython] C_element094  label="C_element : 052"  # scripted group (container) (typed FeaturePython)
  n = 2
  ref = C_element
FEATURE [App::DocumentObjectGroupPython] H_element086  label="H_element : 048"  # scripted group (container) (typed FeaturePython)
  n = 2
  ref = H_element
FEATURE [App::DocumentObjectGroupPython] F_element016  label="F_element : 007"  # scripted group (container) (typed FeaturePython)
  n = 2
  ref = F_element
FEATURE [App::DocumentObjectGroupPython] G4_POLYVINYLIDENE_FLUORIDE  # scripted group (container) (typed FeaturePython)
  Dunit = g/cm3
  Dvalue = 1.76
  Group = -> [C_element094,H_element086,F_element016]
  conduct = 2
  density = 1
  expand = 3
  formula = G4_POLYVINYLIDENE_FLUORIDE
  name = G4_POLYVINYLIDENE_FLUORIDE
  specific = 4
FEATURE [App::DocumentObjectGroupPython] C_element095  label="C_element : 053"  # scripted group (container) (typed FeaturePython)
  n = 6
  ref = C_element
FEATURE [App::DocumentObjectGroupPython] H_element087  label="H_element : 9"  # scripted group (container) (typed FeaturePython)
  n = 9
  ref = H_element
FEATURE [App::DocumentObjectGroupPython] N_element037  label="N_element : 016"  # scripted group (container) (typed FeaturePython)
  n = 1
  ref = N_element
FEATURE [App::DocumentObjectGroupPython] O_element084  label="O_element : 045"  # scripted group (container) (typed FeaturePython)
  n = 1
  ref = O_element
FEATURE [App::DocumentObjectGroupPython] G4_POLYVINYL_PYRROLIDONE  # scripted group (container) (typed FeaturePython)
  Dunit = g/cm3
  Dvalue = 1.25
  Group = -> [C_element095,H_element087,N_element037,O_element084]
  conduct = 2
  density = 1
  expand = 3
  formula = G4_POLYVINYL_PYRROLIDONE
  name = G4_POLYVINYL_PYRROLIDONE
  specific = 4
FEATURE [App::DocumentObjectGroupPython] K_element008  label="K_element : 1"  # scripted group (container) (typed FeaturePython)
  n = 1
  ref = K_element
FEATURE [App::DocumentObjectGroupPython] I_element006  label="I_element : 003"  # scripted group (container) (typed FeaturePython)
  n = 1
  ref = I_element
FEATURE [App::DocumentObjectGroupPython] G4_POTASSIUM_IODIDE  # scripted group (container) (typed FeaturePython)
  Dunit = g/cm3
  Dvalue = 3.13
  Group = -> [K_element008,I_element006]
  conduct = 2
  density = 1
  expand = 3
  formula = G4_POTASSIUM_IODIDE
  name = G4_POTASSIUM_IODIDE
  specific = 4
FEATURE [App::DocumentObjectGroupPython] K_element009  label="K_element : 2"  # scripted group (container) (typed FeaturePython)
  n = 2
  ref = K_element
FEATURE [App::DocumentObjectGroupPython] O_element085  label="O_element : 046"  # scripted group (container) (typed FeaturePython)
  n = 1
  ref = O_element
FEATURE [App::DocumentObjectGroupPython] G4_POTASSIUM_OXIDE  # scripted group (container) (typed FeaturePython)
  Dunit = g/cm3
  Dvalue = 2.32
  Group = -> [K_element009,O_element085]
  conduct = 2
  density = 1
  expand = 3
  formula = G4_POTASSIUM_OXIDE
  name = G4_POTASSIUM_OXIDE
  specific = 4
FEATURE [App::DocumentObjectGroupPython] C_element096  label="C_element : 054"  # scripted group (container) (typed FeaturePython)
  n = 3
  ref = C_element
FEATURE [App::DocumentObjectGroupPython] H_element088  label="H_element : 049"  # scripted group (container) (typed FeaturePython)
  n = 8
  ref = H_element
FEATURE [App::DocumentObjectGroupPython] G4_PROPANE  # scripted group (container) (typed FeaturePython)
  Dunit = g/cm3
  Dvalue = 0.00187939
  Group = -> [C_element096,H_element088]
  conduct = 2
  density = 1
  expand = 3
  formula = G4_PROPANE
  name = G4_PROPANE
  specific = 4
FEATURE [App::DocumentObjectGroupPython] C_element097  label="C_element : 055"  # scripted group (container) (typed FeaturePython)
  n = 3
  ref = C_element
FEATURE [App::DocumentObjectGroupPython] H_element089  label="H_element : 050"  # scripted group (container) (typed FeaturePython)
  n = 8
  ref = H_element
FEATURE [App::DocumentObjectGroupPython] G4_lPROPANE  # scripted group (container) (typed FeaturePython)
  Dunit = g/cm3
  Dvalue = 0.43
  Group = -> [C_element097,H_element089]
  conduct = 2
  density = 1
  expand = 3
  formula = G4_lPROPANE
  name = G4_lPROPANE
  specific = 4
FEATURE [App::DocumentObjectGroupPython] C_element098  label="C_element : 056"  # scripted group (container) (typed FeaturePython)
  n = 3
  ref = C_element
FEATURE [App::DocumentObjectGroupPython] H_element090  label="H_element : 051"  # scripted group (container) (typed FeaturePython)
  n = 8
  ref = H_element
FEATURE [App::DocumentObjectGroupPython] O_element086  label="O_element : 047"  # scripted group (container) (typed FeaturePython)
  n = 1
  ref = O_element
FEATURE [App::DocumentObjectGroupPython] G4_N_PROPYL_ALCOHOL  label="G4_N-PROPYL_ALCOHOL"  # scripted group (container) (typed FeaturePython)
  Dunit = g/cm3
  Dvalue = 0.8035
  Group = -> [C_element098,H_element090,O_element086]
  conduct = 2
  density = 1
  expand = 3
  formula = G4_N-PROPYL_ALCOHOL
  name = G4_N-PROPYL_ALCOHOL
  specific = 4
FEATURE [App::DocumentObjectGroupPython] C_element099  label="C_element : 057"  # scripted group (container) (typed FeaturePython)
  n = 5
  ref = C_element
FEATURE [App::DocumentObjectGroupPython] H_element091  label="H_element : 052"  # scripted group (container) (typed FeaturePython)
  n = 5
  ref = H_element
FEATURE [App::DocumentObjectGroupPython] N_element038  label="N_element : 017"  # scripted group (container) (typed FeaturePython)
  n = 1
  ref = N_element
FEATURE [App::DocumentObjectGroupPython] G4_PYRIDINE  # scripted group (container) (typed FeaturePython)
  Dunit = g/cm3
  Dvalue = 0.9819
  Group = -> [C_element099,H_element091,N_element038]
  conduct = 2
  density = 1
  expand = 3
  formula = G4_PYRIDINE
  name = G4_PYRIDINE
  specific = 4
FEATURE [App::DocumentObjectGroupPython] H_element092  label="H_element : 0.144"  # scripted group (container) (typed FeaturePython)
  n = 0.143711
FEATURE [App::DocumentObjectGroupPython] C_element100  label="C_element : 0.856"  # scripted group (container) (typed FeaturePython)
  n = 0.856289
FEATURE [App::DocumentObjectGroupPython] G4_RUBBER_BUTYL  # scripted group (container) (typed FeaturePython)
  Dunit = g/cm3
  Dvalue = 0.92
  Group = -> [H_element092,C_element100]
  conduct = 2
  density = 1
  expand = 3
  formula = G4_RUBBER_BUTYL
  name = G4_RUBBER_BUTYL
  specific = 4
FEATURE [App::DocumentObjectGroupPython] H_element093  label="H_element : 0.118"  # scripted group (container) (typed FeaturePython)
  n = 0.118371
FEATURE [App::DocumentObjectGroupPython] C_element101  label="C_element : 0.882"  # scripted group (container) (typed FeaturePython)
  n = 0.881629
FEATURE [App::DocumentObjectGroupPython] G4_RUBBER_NATURAL  # scripted group (container) (typed FeaturePython)
  Dunit = g/cm3
  Dvalue = 0.92
  Group = -> [H_element093,C_element101]
  conduct = 2
  density = 1
  expand = 3
  formula = G4_RUBBER_NATURAL
  name = G4_RUBBER_NATURAL
  specific = 4
FEATURE [App::DocumentObjectGroupPython] H_element094  label="H_element : 0.145"  # scripted group (container) (typed FeaturePython)
  n = 0.05692
FEATURE [App::DocumentObjectGroupPython] C_element102  label="C_element : 0.543"  # scripted group (container) (typed FeaturePython)
  n = 0.542646
FEATURE [App::DocumentObjectGroupPython] Cl_element021  label="Cl_element : 0.400"  # scripted group (container) (typed FeaturePython)
  n = 0.400434
FEATURE [App::DocumentObjectGroupPython] G4_RUBBER_NEOPRENE  # scripted group (container) (typed FeaturePython)
  Dunit = g/cm3
  Dvalue = 1.23
  Group = -> [H_element094,C_element102,Cl_element021]
  conduct = 2
  density = 1
  expand = 3
  formula = G4_RUBBER_NEOPRENE
  name = G4_RUBBER_NEOPRENE
  specific = 4
FEATURE [App::DocumentObjectGroupPython] Si_element006  label="Si_element : 1"  # scripted group (container) (typed FeaturePython)
  n = 1
  ref = Si_element
FEATURE [App::DocumentObjectGroupPython] O_element087  label="O_element : 048"  # scripted group (container) (typed FeaturePython)
  n = 2
  ref = O_element
FEATURE [App::DocumentObjectGroupPython] G4_SILICON_DIOXIDE  # scripted group (container) (typed FeaturePython)
  Dunit = g/cm3
  Dvalue = 2.32
  Group = -> [Si_element006,O_element087]
  conduct = 2
  density = 1
  expand = 3
  formula = G4_SILICON_DIOXIDE
  name = G4_SILICON_DIOXIDE
  specific = 4
FEATURE [App::DocumentObjectGroupPython] Ag_element002  label="Ag_element : 1"  # scripted group (container) (typed FeaturePython)
  n = 1
  ref = Ag_element
FEATURE [App::DocumentObjectGroupPython] Br_element005  label="Br_element : 003"  # scripted group (container) (typed FeaturePython)
  n = 1
  ref = Br_element
FEATURE [App::DocumentObjectGroupPython] G4_SILVER_BROMIDE  # scripted group (container) (typed FeaturePython)
  Dunit = g/cm3
  Dvalue = 6.473
  Group = -> [Ag_element002,Br_element005]
  conduct = 2
  density = 1
  expand = 3
  formula = G4_SILVER_BROMIDE
  name = G4_SILVER_BROMIDE
  specific = 4
FEATURE [App::DocumentObjectGroupPython] Ag_element003  label="Ag_element : 002"  # scripted group (container) (typed FeaturePython)
  n = 1
  ref = Ag_element
FEATURE [App::DocumentObjectGroupPython] Cl_element022  label="Cl_element : 011"  # scripted group (container) (typed FeaturePython)
  n = 1
  ref = Cl_element
FEATURE [App::DocumentObjectGroupPython] G4_SILVER_CHLORIDE  # scripted group (container) (typed FeaturePython)
  Dunit = g/cm3
  Dvalue = 5.56
  Group = -> [Ag_element003,Cl_element022]
  conduct = 2
  density = 1
  expand = 3
  formula = G4_SILVER_CHLORIDE
  name = G4_SILVER_CHLORIDE
  specific = 4
FEATURE [App::DocumentObjectGroupPython] Br_element006  label="Br_element : 0.423"  # scripted group (container) (typed FeaturePython)
  n = 0.422895
FEATURE [App::DocumentObjectGroupPython] Ag_element004  label="Ag_element : 0.574"  # scripted group (container) (typed FeaturePython)
  n = 0.573748
FEATURE [App::DocumentObjectGroupPython] I_element007  label="I_element : 0.649"  # scripted group (container) (typed FeaturePython)
  n = 0.003357
FEATURE [App::DocumentObjectGroupPython] G4_SILVER_HALIDES  # scripted group (container) (typed FeaturePython)
  Dunit = g/cm3
  Dvalue = 6.47
  Group = -> [Br_element006,Ag_element004,I_element007]
  conduct = 2
  density = 1
  expand = 3
  formula = G4_SILVER_HALIDES
  name = G4_SILVER_HALIDES
  specific = 4
FEATURE [App::DocumentObjectGroupPython] Ag_element005  label="Ag_element : 003"  # scripted group (container) (typed FeaturePython)
  n = 1
  ref = Ag_element
FEATURE [App::DocumentObjectGroupPython] I_element008  label="I_element : 004"  # scripted group (container) (typed FeaturePython)
  n = 1
  ref = I_element
FEATURE [App::DocumentObjectGroupPython] G4_SILVER_IODIDE  # scripted group (container) (typed FeaturePython)
  Dunit = g/cm3
  Dvalue = 6.01
  Group = -> [Ag_element005,I_element008]
  conduct = 2
  density = 1
  expand = 3
  formula = G4_SILVER_IODIDE
  name = G4_SILVER_IODIDE
  specific = 4
FEATURE [App::DocumentObjectGroupPython] H_element095  label="H_element : 0.100"  # scripted group (container) (typed FeaturePython)
  n = 0.1
FEATURE [App::DocumentObjectGroupPython] C_element103  label="C_element : 0.204"  # scripted group (container) (typed FeaturePython)
  n = 0.204
FEATURE [App::DocumentObjectGroupPython] N_element039  label="N_element : 0.759"  # scripted group (container) (typed FeaturePython)
  n = 0.042
FEATURE [App::DocumentObjectGroupPython] O_element088  label="O_element : 0.645"  # scripted group (container) (typed FeaturePython)
  n = 0.645
FEATURE [App::DocumentObjectGroupPython] Na_element013  label="Na_element : 0.100"  # scripted group (container) (typed FeaturePython)
  n = 0.002
FEATURE [App::DocumentObjectGroupPython] P_element009  label="P_element : 0.107"  # scripted group (container) (typed FeaturePython)
  n = 0.001
FEATURE [App::DocumentObjectGroupPython] S_element020  label="S_element : 0.021"  # scripted group (container) (typed FeaturePython)
  n = 0.002
FEATURE [App::DocumentObjectGroupPython] Cl_element023  label="Cl_element : 0.590"  # scripted group (container) (typed FeaturePython)
  n = 0.003
FEATURE [App::DocumentObjectGroupPython] K_element010  label="K_element : 0.001"  # scripted group (container) (typed FeaturePython)
  n = 0.001
FEATURE [App::DocumentObjectGroupPython] G4_SKIN_ICRP  # scripted group (container) (typed FeaturePython)
  Dunit = g/cm3
  Dvalue = 1.09
  Group = -> [H_element095,C_element103,N_element039,O_element088,Na_element013,P_element009,S_element020,Cl_element023,K_element010]
  conduct = 2
  density = 1
  expand = 3
  formula = G4_SKIN_ICRP
  name = G4_SKIN_ICRP
  specific = 4
FEATURE [App::DocumentObjectGroupPython] Na_element014  label="Na_element : 2"  # scripted group (container) (typed FeaturePython)
  n = 2
  ref = Na_element
FEATURE [App::DocumentObjectGroupPython] C_element104  label="C_element : 058"  # scripted group (container) (typed FeaturePython)
  n = 1
  ref = C_element
FEATURE [App::DocumentObjectGroupPython] O_element089  label="O_element : 049"  # scripted group (container) (typed FeaturePython)
  n = 3
  ref = O_element
FEATURE [App::DocumentObjectGroupPython] G4_SODIUM_CARBONATE  # scripted group (container) (typed FeaturePython)
  Dunit = g/cm3
  Dvalue = 2.532
  Group = -> [Na_element014,C_element104,O_element089]
  conduct = 2
  density = 1
  expand = 3
  formula = G4_SODIUM_CARBONATE
  name = G4_SODIUM_CARBONATE
  specific = 4
FEATURE [App::DocumentObjectGroupPython] Na_element015  label="Na_element : 1"  # scripted group (container) (typed FeaturePython)
  n = 1
  ref = Na_element
FEATURE [App::DocumentObjectGroupPython] I_element009  label="I_element : 005"  # scripted group (container) (typed FeaturePython)
  n = 1
  ref = I_element
FEATURE [App::DocumentObjectGroupPython] G4_SODIUM_IODIDE  # scripted group (container) (typed FeaturePython)
  Dunit = g/cm3
  Dvalue = 3.667
  Group = -> [Na_element015,I_element009]
  conduct = 2
  density = 1
  expand = 3
  formula = G4_SODIUM_IODIDE
  name = G4_SODIUM_IODIDE
  specific = 4
FEATURE [App::DocumentObjectGroupPython] Na_element016  label="Na_element : 003"  # scripted group (container) (typed FeaturePython)
  n = 2
  ref = Na_element
FEATURE [App::DocumentObjectGroupPython] O_element090  label="O_element : 050"  # scripted group (container) (typed FeaturePython)
  n = 1
  ref = O_element
FEATURE [App::DocumentObjectGroupPython] G4_SODIUM_MONOXIDE  # scripted group (container) (typed FeaturePython)
  Dunit = g/cm3
  Dvalue = 2.27
  Group = -> [Na_element016,O_element090]
  conduct = 2
  density = 1
  expand = 3
  formula = G4_SODIUM_MONOXIDE
  name = G4_SODIUM_MONOXIDE
  specific = 4
FEATURE [App::DocumentObjectGroupPython] Na_element017  label="Na_element : 004"  # scripted group (container) (typed FeaturePython)
  n = 1
  ref = Na_element
FEATURE [App::DocumentObjectGroupPython] N_element040  label="N_element : 018"  # scripted group (container) (typed FeaturePython)
  n = 1
  ref = N_element
FEATURE [App::DocumentObjectGroupPython] O_element091  label="O_element : 051"  # scripted group (container) (typed FeaturePython)
  n = 3
  ref = O_element
FEATURE [App::DocumentObjectGroupPython] G4_SODIUM_NITRATE  # scripted group (container) (typed FeaturePython)
  Dunit = g/cm3
  Dvalue = 2.261
  Group = -> [Na_element017,N_element040,O_element091]
  conduct = 2
  density = 1
  expand = 3
  formula = G4_SODIUM_NITRATE
  name = G4_SODIUM_NITRATE
  specific = 4
FEATURE [App::DocumentObjectGroupPython] C_element105  label="C_element : 059"  # scripted group (container) (typed FeaturePython)
  n = 14
  ref = C_element
FEATURE [App::DocumentObjectGroupPython] H_element096  label="H_element : 053"  # scripted group (container) (typed FeaturePython)
  n = 12
  ref = H_element
FEATURE [App::DocumentObjectGroupPython] G4_STILBENE  # scripted group (container) (typed FeaturePython)
  Dunit = g/cm3
  Dvalue = 0.9707
  Group = -> [C_element105,H_element096]
  conduct = 2
  density = 1
  expand = 3
  formula = G4_STILBENE
  name = G4_STILBENE
  specific = 4
FEATURE [App::DocumentObjectGroupPython] C_element106  label="C_element : 12"  # scripted group (container) (typed FeaturePython)
  n = 12
  ref = C_element
FEATURE [App::DocumentObjectGroupPython] H_element097  label="H_element : 22"  # scripted group (container) (typed FeaturePython)
  n = 22
  ref = H_element
FEATURE [App::DocumentObjectGroupPython] O_element092  label="O_element : 11"  # scripted group (container) (typed FeaturePython)
  n = 11
  ref = O_element
FEATURE [App::DocumentObjectGroupPython] G4_SUCROSE  # scripted group (container) (typed FeaturePython)
  Dunit = g/cm3
  Dvalue = 1.5805
  Group = -> [C_element106,H_element097,O_element092]
  conduct = 2
  density = 1
  expand = 3
  formula = G4_SUCROSE
  name = G4_SUCROSE
  specific = 4
FEATURE [App::DocumentObjectGroupPython] C_element107  label="C_element : 18"  # scripted group (container) (typed FeaturePython)
  n = 18
  ref = C_element
FEATURE [App::DocumentObjectGroupPython] H_element098  label="H_element : 054"  # scripted group (container) (typed FeaturePython)
  n = 14
  ref = H_element
FEATURE [App::DocumentObjectGroupPython] G4_TERPHENYL  # scripted group (container) (typed FeaturePython)
  Dunit = g/cm3
  Dvalue = 1.24
  Group = -> [C_element107,H_element098]
  conduct = 2
  density = 1
  expand = 3
  formula = G4_TERPHENYL
  name = G4_TERPHENYL
  specific = 4
FEATURE [App::DocumentObjectGroupPython] H_element099  label="H_element : 0.146"  # scripted group (container) (typed FeaturePython)
  n = 0.106
FEATURE [App::DocumentObjectGroupPython] C_element108  label="C_element : 0.883"  # scripted group (container) (typed FeaturePython)
  n = 0.099
FEATURE [App::DocumentObjectGroupPython] N_element041  label="N_element : 0.020"  # scripted group (container) (typed FeaturePython)
  n = 0.02
FEATURE [App::DocumentObjectGroupPython] O_element093  label="O_element : 0.766"  # scripted group (container) (typed FeaturePython)
  n = 0.766
FEATURE [App::DocumentObjectGroupPython] Na_element018  label="Na_element : 0.101"  # scripted group (container) (typed FeaturePython)
  n = 0.002
FEATURE [App::DocumentObjectGroupPython] P_element010  label="P_element : 0.108"  # scripted group (container) (typed FeaturePython)
  n = 0.001
FEATURE [App::DocumentObjectGroupPython] S_element021  label="S_element : 0.022"  # scripted group (container) (typed FeaturePython)
  n = 0.002
FEATURE [App::DocumentObjectGroupPython] Cl_element024  label="Cl_element : 0.002"  # scripted group (container) (typed FeaturePython)
  n = 0.002
FEATURE [App::DocumentObjectGroupPython] K_element011  label="K_element : 0.017"  # scripted group (container) (typed FeaturePython)
  n = 0.002
FEATURE [App::DocumentObjectGroupPython] G4_TESTIS_ICRP  # scripted group (container) (typed FeaturePython)
  Dunit = g/cm3
  Dvalue = 1.04
  Group = -> [H_element099,C_element108,N_element041,O_element093,Na_element018,P_element010,S_element021,Cl_element024,K_element011]
  conduct = 2
  density = 1
  expand = 3
  formula = G4_TESTIS_ICRP
  name = G4_TESTIS_ICRP
  specific = 4
FEATURE [App::DocumentObjectGroupPython] C_element109  label="C_element : 060"  # scripted group (container) (typed FeaturePython)
  n = 2
  ref = C_element
FEATURE [App::DocumentObjectGroupPython] Cl_element025  label="Cl_element : 012"  # scripted group (container) (typed FeaturePython)
  n = 4
  ref = Cl_element
FEATURE [App::DocumentObjectGroupPython] G4_TETRACHLOROETHYLENE  # scripted group (container) (typed FeaturePython)
  Dunit = g/cm3
  Dvalue = 1.625
  Group = -> [C_element109,Cl_element025]
  conduct = 2
  density = 1
  expand = 3
  formula = G4_TETRACHLOROETHYLENE
  name = G4_TETRACHLOROETHYLENE
  specific = 4
FEATURE [App::DocumentObjectGroupPython] Tl_element001  label="Tl_element : 1"  # scripted group (container) (typed FeaturePython)
  n = 1
  ref = Tl_element
FEATURE [App::DocumentObjectGroupPython] Cl_element026  label="Cl_element : 013"  # scripted group (container) (typed FeaturePython)
  n = 1
  ref = Cl_element
FEATURE [App::DocumentObjectGroupPython] G4_THALLIUM_CHLORIDE  # scripted group (container) (typed FeaturePython)
  Dunit = g/cm3
  Dvalue = 7.004
  Group = -> [Tl_element001,Cl_element026]
  conduct = 2
  density = 1
  expand = 3
  formula = G4_THALLIUM_CHLORIDE
  name = G4_THALLIUM_CHLORIDE
  specific = 4
FEATURE [App::DocumentObjectGroupPython] H_element100  label="H_element : 0.147"  # scripted group (container) (typed FeaturePython)
  n = 0.105
FEATURE [App::DocumentObjectGroupPython] C_element110  label="C_element : 0.256"  # scripted group (container) (typed FeaturePython)
  n = 0.256
FEATURE [App::DocumentObjectGroupPython] N_element042  label="N_element : 0.760"  # scripted group (container) (typed FeaturePython)
  n = 0.027
FEATURE [App::DocumentObjectGroupPython] O_element094  label="O_element : 0.602"  # scripted group (container) (typed FeaturePython)
  n = 0.602
FEATURE [App::DocumentObjectGroupPython] Na_element019  label="Na_element : 0.102"  # scripted group (container) (typed FeaturePython)
  n = 0.001
FEATURE [App::DocumentObjectGroupPython] P_element011  label="P_element : 0.109"  # scripted group (container) (typed FeaturePython)
  n = 0.002
FEATURE [App::DocumentObjectGroupPython] S_element022  label="S_element : 0.023"  # scripted group (container) (typed FeaturePython)
  n = 0.003
FEATURE [App::DocumentObjectGroupPython] Cl_element027  label="Cl_element : 0.591"  # scripted group (container) (typed FeaturePython)
  n = 0.002
FEATURE [App::DocumentObjectGroupPython] K_element012  label="K_element : 0.018"  # scripted group (container) (typed FeaturePython)
  n = 0.002
FEATURE [App::DocumentObjectGroupPython] G4_TISSUE_SOFT_ICRP  # scripted group (container) (typed FeaturePython)
  Dunit = g/cm3
  Dvalue = 1.03
  Group = -> [H_element100,C_element110,N_element042,O_element094,Na_element019,P_element011,S_element022,Cl_element027,K_element012]
  conduct = 2
  density = 1
  expand = 3
  formula = G4_TISSUE_SOFT_ICRP
  name = G4_TISSUE_SOFT_ICRP
  specific = 4
FEATURE [App::DocumentObjectGroupPython] H_element101  label="H_element : 0.148"  # scripted group (container) (typed FeaturePython)
  n = 0.101
FEATURE [App::DocumentObjectGroupPython] C_element111  label="C_element : 0.111"  # scripted group (container) (typed FeaturePython)
  n = 0.111
FEATURE [App::DocumentObjectGroupPython] N_element043  label="N_element : 0.026"  # scripted group (container) (typed FeaturePython)
  n = 0.026
FEATURE [App::DocumentObjectGroupPython] O_element095  label="O_element : 0.762"  # scripted group (container) (typed FeaturePython)
  n = 0.762
FEATURE [App::DocumentObjectGroupPython] G4_TISSUE_SOFT_ICRU_4  label="G4_TISSUE_SOFT_ICRU-4"  # scripted group (container) (typed FeaturePython)
  Dunit = g/cm3
  Dvalue = 1
  Group = -> [H_element101,C_element111,N_element043,O_element095]
  conduct = 2
  density = 1
  expand = 3
  formula = G4_TISSUE_SOFT_ICRU-4
  name = G4_TISSUE_SOFT_ICRU-4
  specific = 4
FEATURE [App::DocumentObjectGroupPython] H_element102  label="H_element : 0.149"  # scripted group (container) (typed FeaturePython)
  n = 0.101869
FEATURE [App::DocumentObjectGroupPython] C_element112  label="C_element : 0.456"  # scripted group (container) (typed FeaturePython)
  n = 0.456179
FEATURE [App::DocumentObjectGroupPython] N_element044  label="N_element : 0.761"  # scripted group (container) (typed FeaturePython)
  n = 0.035172
FEATURE [App::DocumentObjectGroupPython] O_element096  label="O_element : 0.407"  # scripted group (container) (typed FeaturePython)
  n = 0.40678
FEATURE [App::DocumentObjectGroupPython] G4_TISSUE_METHANE  label="G4_TISSUE-METHANE"  # scripted group (container) (typed FeaturePython)
  Dunit = g/cm3
  Dvalue = 0.00106409
  Group = -> [H_element102,C_element112,N_element044,O_element096]
  conduct = 2
  density = 1
  expand = 3
  formula = G4_TISSUE-METHANE
  name = G4_TISSUE-METHANE
  specific = 4
FEATURE [App::DocumentObjectGroupPython] H_element103  label="H_element : 0.103"  # scripted group (container) (typed FeaturePython)
  n = 0.102672
FEATURE [App::DocumentObjectGroupPython] C_element113  label="C_element : 0.569"  # scripted group (container) (typed FeaturePython)
  n = 0.56894
FEATURE [App::DocumentObjectGroupPython] N_element045  label="N_element : 0.762"  # scripted group (container) (typed FeaturePython)
  n = 0.035022
FEATURE [App::DocumentObjectGroupPython] O_element097  label="O_element : 0.293"  # scripted group (container) (typed FeaturePython)
  n = 0.293366
FEATURE [App::DocumentObjectGroupPython] G4_TISSUE_PROPANE  label="G4_TISSUE-PROPANE"  # scripted group (container) (typed FeaturePython)
  Dunit = g/cm3
  Dvalue = 0.00182628
  Group = -> [H_element103,C_element113,N_element045,O_element097]
  conduct = 2
  density = 1
  expand = 3
  formula = G4_TISSUE-PROPANE
  name = G4_TISSUE-PROPANE
  specific = 4
FEATURE [App::DocumentObjectGroupPython] Ti_element003  label="Ti_element : 1"  # scripted group (container) (typed FeaturePython)
  n = 1
  ref = Ti_element
FEATURE [App::DocumentObjectGroupPython] O_element098  label="O_element : 052"  # scripted group (container) (typed FeaturePython)
  n = 2
  ref = O_element
FEATURE [App::DocumentObjectGroupPython] G4_TITANIUM_DIOXIDE  # scripted group (container) (typed FeaturePython)
  Dunit = g/cm3
  Dvalue = 4.26
  Group = -> [Ti_element003,O_element098]
  conduct = 2
  density = 1
  expand = 3
  formula = G4_TITANIUM_DIOXIDE
  name = G4_TITANIUM_DIOXIDE
  specific = 4
FEATURE [App::DocumentObjectGroupPython] C_element114  label="C_element : 061"  # scripted group (container) (typed FeaturePython)
  n = 7
  ref = C_element
FEATURE [App::DocumentObjectGroupPython] H_element104  label="H_element : 055"  # scripted group (container) (typed FeaturePython)
  n = 8
  ref = H_element
FEATURE [App::DocumentObjectGroupPython] G4_TOLUENE  # scripted group (container) (typed FeaturePython)
  Dunit = g/cm3
  Dvalue = 0.8669
  Group = -> [C_element114,H_element104]
  conduct = 2
  density = 1
  expand = 3
  formula = G4_TOLUENE
  name = G4_TOLUENE
  specific = 4
FEATURE [App::DocumentObjectGroupPython] C_element115  label="C_element : 062"  # scripted group (container) (typed FeaturePython)
  n = 2
  ref = C_element
FEATURE [App::DocumentObjectGroupPython] H_element105  label="H_element : 056"  # scripted group (container) (typed FeaturePython)
  n = 1
  ref = H_element
FEATURE [App::DocumentObjectGroupPython] Cl_element028  label="Cl_element : 014"  # scripted group (container) (typed FeaturePython)
  n = 3
  ref = Cl_element
FEATURE [App::DocumentObjectGroupPython] G4_TRICHLOROETHYLENE  # scripted group (container) (typed FeaturePython)
  Dunit = g/cm3
  Dvalue = 1.46
  Group = -> [C_element115,H_element105,Cl_element028]
  conduct = 2
  density = 1
  expand = 3
  formula = G4_TRICHLOROETHYLENE
  name = G4_TRICHLOROETHYLENE
  specific = 4
FEATURE [App::DocumentObjectGroupPython] C_element116  label="C_element : 063"  # scripted group (container) (typed FeaturePython)
  n = 6
  ref = C_element
FEATURE [App::DocumentObjectGroupPython] H_element106  label="H_element : 15"  # scripted group (container) (typed FeaturePython)
  n = 15
  ref = H_element
FEATURE [App::DocumentObjectGroupPython] O_element099  label="O_element : 053"  # scripted group (container) (typed FeaturePython)
  n = 4
  ref = O_element
FEATURE [App::DocumentObjectGroupPython] P_element012  label="P_element : 1"  # scripted group (container) (typed FeaturePython)
  n = 1
  ref = P_element
FEATURE [App::DocumentObjectGroupPython] G4_TRIETHYL_PHOSPHATE  # scripted group (container) (typed FeaturePython)
  Dunit = g/cm3
  Dvalue = 1.07
  Group = -> [C_element116,H_element106,O_element099,P_element012]
  conduct = 2
  density = 1
  expand = 3
  formula = G4_TRIETHYL_PHOSPHATE
  name = G4_TRIETHYL_PHOSPHATE
  specific = 4
FEATURE [App::DocumentObjectGroupPython] W_element003  label="W_element : 003"  # scripted group (container) (typed FeaturePython)
  n = 1
  ref = W_element
FEATURE [App::DocumentObjectGroupPython] F_element017  label="F_element : 6"  # scripted group (container) (typed FeaturePython)
  n = 6
  ref = F_element
FEATURE [App::DocumentObjectGroupPython] G4_TUNGSTEN_HEXAFLUORIDE  # scripted group (container) (typed FeaturePython)
  Dunit = g/cm3
  Dvalue = 2.4
  Group = -> [W_element003,F_element017]
  conduct = 2
  density = 1
  expand = 3
  formula = G4_TUNGSTEN_HEXAFLUORIDE
  name = G4_TUNGSTEN_HEXAFLUORIDE
  specific = 4
FEATURE [App::DocumentObjectGroupPython] U_element001  label="U_element : 1"  # scripted group (container) (typed FeaturePython)
  n = 1
  ref = U_element
FEATURE [App::DocumentObjectGroupPython] C_element117  label="C_element : 064"  # scripted group (container) (typed FeaturePython)
  n = 2
  ref = C_element
FEATURE [App::DocumentObjectGroupPython] G4_URANIUM_DICARBIDE  # scripted group (container) (typed FeaturePython)
  Dunit = g/cm3
  Dvalue = 11.28
  Group = -> [U_element001,C_element117]
  conduct = 2
  density = 1
  expand = 3
  formula = G4_URANIUM_DICARBIDE
  name = G4_URANIUM_DICARBIDE
  specific = 4
FEATURE [App::DocumentObjectGroupPython] U_element002  label="U_element : 002"  # scripted group (container) (typed FeaturePython)
  n = 1
  ref = U_element
FEATURE [App::DocumentObjectGroupPython] C_element118  label="C_element : 065"  # scripted group (container) (typed FeaturePython)
  n = 1
  ref = C_element
FEATURE [App::DocumentObjectGroupPython] G4_URANIUM_MONOCARBIDE  # scripted group (container) (typed FeaturePython)
  Dunit = g/cm3
  Dvalue = 13.63
  Group = -> [U_element002,C_element118]
  conduct = 2
  density = 1
  expand = 3
  formula = G4_URANIUM_MONOCARBIDE
  name = G4_URANIUM_MONOCARBIDE
  specific = 4
FEATURE [App::DocumentObjectGroupPython] U_element003  label="U_element : 003"  # scripted group (container) (typed FeaturePython)
  n = 1
  ref = U_element
FEATURE [App::DocumentObjectGroupPython] O_element100  label="O_element : 054"  # scripted group (container) (typed FeaturePython)
  n = 2
  ref = O_element
FEATURE [App::DocumentObjectGroupPython] G4_URANIUM_OXIDE  # scripted group (container) (typed FeaturePython)
  Dunit = g/cm3
  Dvalue = 10.96
  Group = -> [U_element003,O_element100]
  conduct = 2
  density = 1
  expand = 3
  formula = G4_URANIUM_OXIDE
  name = G4_URANIUM_OXIDE
  specific = 4
FEATURE [App::DocumentObjectGroupPython] C_element119  label="C_element : 066"  # scripted group (container) (typed FeaturePython)
  n = 1
  ref = C_element
FEATURE [App::DocumentObjectGroupPython] H_element107  label="H_element : 057"  # scripted group (container) (typed FeaturePython)
  n = 4
  ref = H_element
FEATURE [App::DocumentObjectGroupPython] N_element046  label="N_element : 019"  # scripted group (container) (typed FeaturePython)
  n = 2
  ref = N_element
FEATURE [App::DocumentObjectGroupPython] O_element101  label="O_element : 055"  # scripted group (container) (typed FeaturePython)
  n = 1
  ref = O_element
FEATURE [App::DocumentObjectGroupPython] G4_UREA  # scripted group (container) (typed FeaturePython)
  Dunit = g/cm3
  Dvalue = 1.323
  Group = -> [C_element119,H_element107,N_element046,O_element101]
  conduct = 2
  density = 1
  expand = 3
  formula = G4_UREA
  name = G4_UREA
  specific = 4
FEATURE [App::DocumentObjectGroupPython] C_element120  label="C_element : 067"  # scripted group (container) (typed FeaturePython)
  n = 5
  ref = C_element
FEATURE [App::DocumentObjectGroupPython] H_element108  label="H_element : 058"  # scripted group (container) (typed FeaturePython)
  n = 11
  ref = H_element
FEATURE [App::DocumentObjectGroupPython] N_element047  label="N_element : 020"  # scripted group (container) (typed FeaturePython)
  n = 1
  ref = N_element
FEATURE [App::DocumentObjectGroupPython] O_element102  label="O_element : 056"  # scripted group (container) (typed FeaturePython)
  n = 2
  ref = O_element
FEATURE [App::DocumentObjectGroupPython] G4_VALINE  # scripted group (container) (typed FeaturePython)
  Dunit = g/cm3
  Dvalue = 1.23
  Group = -> [C_element120,H_element108,N_element047,O_element102]
  conduct = 2
  density = 1
  expand = 3
  formula = G4_VALINE
  name = G4_VALINE
  specific = 4
FEATURE [App::DocumentObjectGroupPython] H_element109  label="H_element : 0.009"  # scripted group (container) (typed FeaturePython)
  n = 0.009417
FEATURE [App::DocumentObjectGroupPython] C_element121  label="C_element : 0.281"  # scripted group (container) (typed FeaturePython)
  n = 0.280555
FEATURE [App::DocumentObjectGroupPython] F_element018  label="F_element : 0.710"  # scripted group (container) (typed FeaturePython)
  n = 0.710028
FEATURE [App::DocumentObjectGroupPython] G4_VITON  # scripted group (container) (typed FeaturePython)
  Dunit = g/cm3
  Dvalue = 1.8
  Group = -> [H_element109,C_element121,F_element018]
  conduct = 2
  density = 1
  expand = 3
  formula = G4_VITON
  name = G4_VITON
  specific = 4
FEATURE [App::DocumentObjectGroupPython] H_element110  label="H_element : 059"  # scripted group (container) (typed FeaturePython)
  n = 2
  ref = H_element
FEATURE [App::DocumentObjectGroupPython] O_element103  label="O_element : 057"  # scripted group (container) (typed FeaturePython)
  n = 1
  ref = O_element
FEATURE [App::DocumentObjectGroupPython] G4_WATER  # scripted group (container) (typed FeaturePython)
  Dunit = g/cm3
  Dvalue = 1
  Group = -> [H_element110,O_element103]
  conduct = 2
  density = 1
  expand = 3
  formula = G4_WATER
  name = G4_WATER
  specific = 4
FEATURE [App::DocumentObjectGroupPython] H_element111  label="H_element : 060"  # scripted group (container) (typed FeaturePython)
  n = 2
  ref = H_element
FEATURE [App::DocumentObjectGroupPython] O_element104  label="O_element : 058"  # scripted group (container) (typed FeaturePython)
  n = 1
  ref = O_element
FEATURE [App::DocumentObjectGroupPython] G4_WATER_VAPOR  # scripted group (container) (typed FeaturePython)
  Dunit = g/cm3
  Dvalue = 0.000756182
  Group = -> [H_element111,O_element104]
  conduct = 2
  density = 1
  expand = 3
  formula = G4_WATER_VAPOR
  name = G4_WATER_VAPOR
  specific = 4
FEATURE [App::DocumentObjectGroupPython] C_element122  label="C_element : 068"  # scripted group (container) (typed FeaturePython)
  n = 8
  ref = C_element
FEATURE [App::DocumentObjectGroupPython] H_element112  label="H_element : 061"  # scripted group (container) (typed FeaturePython)
  n = 10
  ref = H_element
FEATURE [App::DocumentObjectGroupPython] G4_XYLENE  # scripted group (container) (typed FeaturePython)
  Dunit = g/cm3
  Dvalue = 0.87
  Group = -> [C_element122,H_element112]
  conduct = 2
  density = 1
  expand = 3
  formula = G4_XYLENE
  name = G4_XYLENE
  specific = 4
FEATURE [App::DocumentObjectGroupPython] C_element123  label="C_element : 069"  # scripted group (container) (typed FeaturePython)
  n = 1
  ref = C_element
FEATURE [App::DocumentObjectGroupPython] G4_GRAPHITE  # scripted group (container) (typed FeaturePython)
  Dunit = g/cm3
  Dvalue = 2.21
  Group = -> [C_element123]
  conduct = 2
  density = 1
  expand = 3
  formula = G4_GRAPHITE
  name = G4_GRAPHITE
  specific = 4
FEATURE [App::DocumentObjectGroupPython] NIST  # scripted group (container) (typed FeaturePython)
  Group = -> [G4_A_150_TISSUE,G4_ACETONE,G4_ACETYLENE,G4_ADENINE,G4_ADIPOSE_TISSUE_ICRP,G4_AIR,G4_ALANINE,G4_ALUMINUM_OXIDE,G4_AMBER,G4_AMMONIA,G4_ANILINE,G4_ANTHRACENE,G4_B_100_BONE,G4_BAKELITE,G4_BARIUM_FLUORIDE,G4_BARIUM_SULFATE,G4_BENZENE,G4_BERYLLIUM_OXIDE,G4_BGO,G4_BLOOD_ICRP,G4_BONE_COMPACT_ICRU,G4_BONE_CORTICAL_ICRP,G4_BORON_CARBIDE,G4_BORON_OXIDE,G4_BRAIN_ICRP,G4_BUTANE,G4_N_BUTYL_ALCOHOL,G4_C_552,+152 more]
FEATURE [App::DocumentObjectGroupPython] H_element113  label="H_element : 062"  # scripted group (container) (typed FeaturePython)
  n = 1
  ref = H_element
FEATURE [App::DocumentObjectGroupPython] G4_H  # scripted group (container) (typed FeaturePython)
  Dunit = g/cm3
  Dvalue = 8.3748e-05
  Group = -> [H_element113]
  conduct = 2
  density = 1
  expand = 3
  formula = H
  name = G4_H
  specific = 4
FEATURE [App::DocumentObjectGroupPython] He_element001  label="He_element : 1"  # scripted group (container) (typed FeaturePython)
  n = 1
  ref = He_element
FEATURE [App::DocumentObjectGroupPython] G4_He  # scripted group (container) (typed FeaturePython)
  Dunit = g/cm3
  Dvalue = 0.000166322
  Group = -> [He_element001]
  conduct = 2
  density = 1
  expand = 3
  formula = He
  name = G4_He
  specific = 4
FEATURE [App::DocumentObjectGroupPython] Li_element008  label="Li_element : 008"  # scripted group (container) (typed FeaturePython)
  n = 1
  ref = Li_element
FEATURE [App::DocumentObjectGroupPython] G4_Li  # scripted group (container) (typed FeaturePython)
  Dunit = g/cm3
  Dvalue = 0.534
  Group = -> [Li_element008]
  conduct = 2
  density = 1
  expand = 3
  formula = Li
  name = G4_Li
  specific = 4
FEATURE [App::DocumentObjectGroupPython] Be_element002  label="Be_element : 002"  # scripted group (container) (typed FeaturePython)
  n = 1
  ref = Be_element
FEATURE [App::DocumentObjectGroupPython] G4_Be  # scripted group (container) (typed FeaturePython)
  Dunit = g/cm3
  Dvalue = 1.848
  Group = -> [Be_element002]
  conduct = 2
  density = 1
  expand = 3
  formula = Be
  name = G4_Be
  specific = 4
FEATURE [App::DocumentObjectGroupPython] B_element007  label="B_element : 007"  # scripted group (container) (typed FeaturePython)
  n = 1
  ref = B_element
FEATURE [App::DocumentObjectGroupPython] G4_B  # scripted group (container) (typed FeaturePython)
  Dunit = g/cm3
  Dvalue = 2.37
  Group = -> [B_element007]
  conduct = 2
  density = 1
  expand = 3
  formula = B
  name = G4_B
  specific = 4
FEATURE [App::DocumentObjectGroupPython] C_element124  label="C_element : 070"  # scripted group (container) (typed FeaturePython)
  n = 1
  ref = C_element
FEATURE [App::DocumentObjectGroupPython] G4_C  # scripted group (container) (typed FeaturePython)
  Dunit = g/cm3
  Dvalue = 2
  Group = -> [C_element124]
  conduct = 2
  density = 1
  expand = 3
  formula = C
  name = G4_C
  specific = 4
FEATURE [App::DocumentObjectGroupPython] N_element048  label="N_element : 021"  # scripted group (container) (typed FeaturePython)
  n = 1
  ref = N_element
FEATURE [App::DocumentObjectGroupPython] G4_N  # scripted group (container) (typed FeaturePython)
  Dunit = g/cm3
  Dvalue = 0.0011652
  Group = -> [N_element048]
  conduct = 2
  density = 1
  expand = 3
  formula = N
  name = G4_N
  specific = 4
FEATURE [App::DocumentObjectGroupPython] O_element105  label="O_element : 059"  # scripted group (container) (typed FeaturePython)
  n = 1
  ref = O_element
FEATURE [App::DocumentObjectGroupPython] G4_O  # scripted group (container) (typed FeaturePython)
  Dunit = g/cm3
  Dvalue = 0.00133151
  Group = -> [O_element105]
  conduct = 2
  density = 1
  expand = 3
  formula = O
  name = G4_O
  specific = 4
FEATURE [App::DocumentObjectGroupPython] F_element019  label="F_element : 008"  # scripted group (container) (typed FeaturePython)
  n = 1
  ref = F_element
FEATURE [App::DocumentObjectGroupPython] G4_F  # scripted group (container) (typed FeaturePython)
  Dunit = g/cm3
  Dvalue = 0.00158029
  Group = -> [F_element019]
  conduct = 2
  density = 1
  expand = 3
  formula = F
  name = G4_F
  specific = 4
FEATURE [App::DocumentObjectGroupPython] Ne_element001  label="Ne_element : 1"  # scripted group (container) (typed FeaturePython)
  n = 1
  ref = Ne_element
FEATURE [App::DocumentObjectGroupPython] G4_Ne  # scripted group (container) (typed FeaturePython)
  Dunit = g/cm3
  Dvalue = 0.000838505
  Group = -> [Ne_element001]
  conduct = 2
  density = 1
  expand = 3
  formula = Ne
  name = G4_Ne
  specific = 4
FEATURE [App::DocumentObjectGroupPython] Na_element020  label="Na_element : 005"  # scripted group (container) (typed FeaturePython)
  n = 1
  ref = Na_element
FEATURE [App::DocumentObjectGroupPython] G4_Na  # scripted group (container) (typed FeaturePython)
  Dunit = g/cm3
  Dvalue = 0.971
  Group = -> [Na_element020]
  conduct = 2
  density = 1
  expand = 3
  formula = Na
  name = G4_Na
  specific = 4
FEATURE [App::DocumentObjectGroupPython] Mg_element011  label="Mg_element : 005"  # scripted group (container) (typed FeaturePython)
  n = 1
  ref = Mg_element
FEATURE [App::DocumentObjectGroupPython] G4_Mg  # scripted group (container) (typed FeaturePython)
  Dunit = g/cm3
  Dvalue = 1.74
  Group = -> [Mg_element011]
  conduct = 2
  density = 1
  expand = 3
  formula = Mg
  name = G4_Mg
  specific = 4
FEATURE [App::DocumentObjectGroupPython] Al_element004  label="Al_element : 1"  # scripted group (container) (typed FeaturePython)
  n = 1
  ref = Al_element
FEATURE [App::DocumentObjectGroupPython] G4_Al  # scripted group (container) (typed FeaturePython)
  Dunit = g/cm3
  Dvalue = 2.699
  Group = -> [Al_element004]
  conduct = 2
  density = 1
  expand = 3
  formula = Al
  name = G4_Al
  specific = 4
FEATURE [App::DocumentObjectGroupPython] Si_element007  label="Si_element : 002"  # scripted group (container) (typed FeaturePython)
  n = 1
  ref = Si_element
FEATURE [App::DocumentObjectGroupPython] G4_Si  # scripted group (container) (typed FeaturePython)
  Dunit = g/cm3
  Dvalue = 2.33
  Group = -> [Si_element007]
  conduct = 2
  density = 1
  expand = 3
  formula = Si
  name = G4_Si
  specific = 4
FEATURE [App::DocumentObjectGroupPython] P_element013  label="P_element : 002"  # scripted group (container) (typed FeaturePython)
  n = 1
  ref = P_element
FEATURE [App::DocumentObjectGroupPython] G4_P  # scripted group (container) (typed FeaturePython)
  Dunit = g/cm3
  Dvalue = 2.2
  Group = -> [P_element013]
  conduct = 2
  density = 1
  expand = 3
  formula = P
  name = G4_P
  specific = 4
FEATURE [App::DocumentObjectGroupPython] S_element023  label="S_element : 007"  # scripted group (container) (typed FeaturePython)
  n = 1
  ref = S_element
FEATURE [App::DocumentObjectGroupPython] G4_S  # scripted group (container) (typed FeaturePython)
  Dunit = g/cm3
  Dvalue = 2
  Group = -> [S_element023]
  conduct = 2
  density = 1
  expand = 3
  formula = S
  name = G4_S
  specific = 4
FEATURE [App::DocumentObjectGroupPython] Cl_element029  label="Cl_element : 015"  # scripted group (container) (typed FeaturePython)
  n = 1
  ref = Cl_element
FEATURE [App::DocumentObjectGroupPython] G4_Cl  # scripted group (container) (typed FeaturePython)
  Dunit = g/cm3
  Dvalue = 0.00299473
  Group = -> [Cl_element029]
  conduct = 2
  density = 1
  expand = 3
  formula = Cl
  name = G4_Cl
  specific = 4
FEATURE [App::DocumentObjectGroupPython] Ar_element002  label="Ar_element : 1"  # scripted group (container) (typed FeaturePython)
  n = 1
  ref = Ar_element
FEATURE [App::DocumentObjectGroupPython] G4_Ar  # scripted group (container) (typed FeaturePython)
  Dunit = g/cm3
  Dvalue = 0.00166201
  Group = -> [Ar_element002]
  conduct = 2
  density = 1
  expand = 3
  formula = Ar
  name = G4_Ar
  specific = 4
FEATURE [App::DocumentObjectGroupPython] K_element013  label="K_element : 003"  # scripted group (container) (typed FeaturePython)
  n = 1
  ref = K_element
FEATURE [App::DocumentObjectGroupPython] G4_K  # scripted group (container) (typed FeaturePython)
  Dunit = g/cm3
  Dvalue = 0.862
  Group = -> [K_element013]
  conduct = 2
  density = 1
  expand = 3
  formula = K
  name = G4_K
  specific = 4
FEATURE [App::DocumentObjectGroupPython] Ca_element014  label="Ca_element : 007"  # scripted group (container) (typed FeaturePython)
  n = 1
  ref = Ca_element
FEATURE [App::DocumentObjectGroupPython] G4_Ca  # scripted group (container) (typed FeaturePython)
  Dunit = g/cm3
  Dvalue = 1.55
  Group = -> [Ca_element014]
  conduct = 2
  density = 1
  expand = 3
  formula = Ca
  name = G4_Ca
  specific = 4
FEATURE [App::DocumentObjectGroupPython] Sc_element001  label="Sc_element : 1"  # scripted group (container) (typed FeaturePython)
  n = 1
  ref = Sc_element
FEATURE [App::DocumentObjectGroupPython] G4_Sc  # scripted group (container) (typed FeaturePython)
  Dunit = g/cm3
  Dvalue = 2.989
  Group = -> [Sc_element001]
  conduct = 2
  density = 1
  expand = 3
  formula = Sc
  name = G4_Sc
  specific = 4
FEATURE [App::DocumentObjectGroupPython] Ti_element004  label="Ti_element : 002"  # scripted group (container) (typed FeaturePython)
  n = 1
  ref = Ti_element
FEATURE [App::DocumentObjectGroupPython] G4_Ti  # scripted group (container) (typed FeaturePython)
  Dunit = g/cm3
  Dvalue = 4.54
  Group = -> [Ti_element004]
  conduct = 2
  density = 1
  expand = 3
  formula = Ti
  name = G4_Ti
  specific = 4
FEATURE [App::DocumentObjectGroupPython] V_element001  label="V_element : 1"  # scripted group (container) (typed FeaturePython)
  n = 1
  ref = V_element
FEATURE [App::DocumentObjectGroupPython] G4_V  # scripted group (container) (typed FeaturePython)
  Dunit = g/cm3
  Dvalue = 6.11
  Group = -> [V_element001]
  conduct = 2
  density = 1
  expand = 3
  formula = V
  name = G4_V
  specific = 4
FEATURE [App::DocumentObjectGroupPython] Cr_element001  label="Cr_element : 1"  # scripted group (container) (typed FeaturePython)
  n = 1
  ref = Cr_element
FEATURE [App::DocumentObjectGroupPython] G4_Cr  # scripted group (container) (typed FeaturePython)
  Dunit = g/cm3
  Dvalue = 7.18
  Group = -> [Cr_element001]
  conduct = 2
  density = 1
  expand = 3
  formula = Cr
  name = G4_Cr
  specific = 4
FEATURE [App::DocumentObjectGroupPython] Mn_element001  label="Mn_element : 1"  # scripted group (container) (typed FeaturePython)
  n = 1
  ref = Mn_element
FEATURE [App::DocumentObjectGroupPython] G4_Mn  # scripted group (container) (typed FeaturePython)
  Dunit = g/cm3
  Dvalue = 7.44
  Group = -> [Mn_element001]
  conduct = 2
  density = 1
  expand = 3
  formula = Mn
  name = G4_Mn
  specific = 4
FEATURE [App::DocumentObjectGroupPython] Fe_element007  label="Fe_element : 004"  # scripted group (container) (typed FeaturePython)
  n = 1
  ref = Fe_element
FEATURE [App::DocumentObjectGroupPython] G4_Fe  # scripted group (container) (typed FeaturePython)
  Dunit = g/cm3
  Dvalue = 7.874
  Group = -> [Fe_element007]
  conduct = 2
  density = 1
  expand = 3
  formula = Fe
  name = G4_Fe
  specific = 4
FEATURE [App::DocumentObjectGroupPython] Co_element001  label="Co_element : 1"  # scripted group (container) (typed FeaturePython)
  n = 1
  ref = Co_element
FEATURE [App::DocumentObjectGroupPython] G4_Co  # scripted group (container) (typed FeaturePython)
  Dunit = g/cm3
  Dvalue = 8.9
  Group = -> [Co_element001]
  conduct = 2
  density = 1
  expand = 3
  formula = Co
  name = G4_Co
  specific = 4
FEATURE [App::DocumentObjectGroupPython] Ni_element001  label="Ni_element : 1"  # scripted group (container) (typed FeaturePython)
  n = 1
  ref = Ni_element
FEATURE [App::DocumentObjectGroupPython] G4_Ni  # scripted group (container) (typed FeaturePython)
  Dunit = g/cm3
  Dvalue = 8.902
  Group = -> [Ni_element001]
  conduct = 2
  density = 1
  expand = 3
  formula = Ni
  name = G4_Ni
  specific = 4
FEATURE [App::DocumentObjectGroupPython] Cu_element001  label="Cu_element : 1"  # scripted group (container) (typed FeaturePython)
  n = 1
  ref = Cu_element
FEATURE [App::DocumentObjectGroupPython] G4_Cu  # scripted group (container) (typed FeaturePython)
  Dunit = g/cm3
  Dvalue = 8.96
  Group = -> [Cu_element001]
  conduct = 2
  density = 1
  expand = 3
  formula = Cu
  name = G4_Cu
  specific = 4
FEATURE [App::DocumentObjectGroupPython] Zn_element001  label="Zn_element : 1"  # scripted group (container) (typed FeaturePython)
  n = 1
  ref = Zn_element
FEATURE [App::DocumentObjectGroupPython] G4_Zn  # scripted group (container) (typed FeaturePython)
  Dunit = g/cm3
  Dvalue = 7.133
  Group = -> [Zn_element001]
  conduct = 2
  density = 1
  expand = 3
  formula = Zn
  name = G4_Zn
  specific = 4
FEATURE [App::DocumentObjectGroupPython] Ga_element002  label="Ga_element : 002"  # scripted group (container) (typed FeaturePython)
  n = 1
  ref = Ga_element
FEATURE [App::DocumentObjectGroupPython] G4_Ga  # scripted group (container) (typed FeaturePython)
  Dunit = g/cm3
  Dvalue = 5.904
  Group = -> [Ga_element002]
  conduct = 2
  density = 1
  expand = 3
  formula = Ga
  name = G4_Ga
  specific = 4
FEATURE [App::DocumentObjectGroupPython] Ge_element002  label="Ge_element : 1"  # scripted group (container) (typed FeaturePython)
  n = 1
  ref = Ge_element
FEATURE [App::DocumentObjectGroupPython] G4_Ge  # scripted group (container) (typed FeaturePython)
  Dunit = g/cm3
  Dvalue = 5.323
  Group = -> [Ge_element002]
  conduct = 2
  density = 1
  expand = 3
  formula = Ge
  name = G4_Ge
  specific = 4
FEATURE [App::DocumentObjectGroupPython] As_element003  label="As_element : 002"  # scripted group (container) (typed FeaturePython)
  n = 1
  ref = As_element
FEATURE [App::DocumentObjectGroupPython] G4_As  # scripted group (container) (typed FeaturePython)
  Dunit = g/cm3
  Dvalue = 5.73
  Group = -> [As_element003]
  conduct = 2
  density = 1
  expand = 3
  formula = As
  name = G4_As
  specific = 4
FEATURE [App::DocumentObjectGroupPython] Se_element001  label="Se_element : 1"  # scripted group (container) (typed FeaturePython)
  n = 1
  ref = Se_element
FEATURE [App::DocumentObjectGroupPython] G4_Se  # scripted group (container) (typed FeaturePython)
  Dunit = g/cm3
  Dvalue = 4.5
  Group = -> [Se_element001]
  conduct = 2
  density = 1
  expand = 3
  formula = Se
  name = G4_Se
  specific = 4
FEATURE [App::DocumentObjectGroupPython] Br_element007  label="Br_element : 004"  # scripted group (container) (typed FeaturePython)
  n = 1
  ref = Br_element
FEATURE [App::DocumentObjectGroupPython] G4_Br  # scripted group (container) (typed FeaturePython)
  Dunit = g/cm3
  Dvalue = 0.0070721
  Group = -> [Br_element007]
  conduct = 2
  density = 1
  expand = 3
  formula = Br
  name = G4_Br
  specific = 4
FEATURE [App::DocumentObjectGroupPython] Kr_element001  label="Kr_element : 1"  # scripted group (container) (typed FeaturePython)
  n = 1
  ref = Kr_element
FEATURE [App::DocumentObjectGroupPython] G4_Kr  # scripted group (container) (typed FeaturePython)
  Dunit = g/cm3
  Dvalue = 0.00347832
  Group = -> [Kr_element001]
  conduct = 2
  density = 1
  expand = 3
  formula = Kr
  name = G4_Kr
  specific = 4
FEATURE [App::DocumentObjectGroupPython] Rb_element001  label="Rb_element : 1"  # scripted group (container) (typed FeaturePython)
  n = 1
  ref = Rb_element
FEATURE [App::DocumentObjectGroupPython] G4_Rb  # scripted group (container) (typed FeaturePython)
  Dunit = g/cm3
  Dvalue = 1.532
  Group = -> [Rb_element001]
  conduct = 2
  density = 1
  expand = 3
  formula = Rb
  name = G4_Rb
  specific = 4
FEATURE [App::DocumentObjectGroupPython] Sr_element001  label="Sr_element : 1"  # scripted group (container) (typed FeaturePython)
  n = 1
  ref = Sr_element
FEATURE [App::DocumentObjectGroupPython] G4_Sr  # scripted group (container) (typed FeaturePython)
  Dunit = g/cm3
  Dvalue = 2.54
  Group = -> [Sr_element001]
  conduct = 2
  density = 1
  expand = 3
  formula = Sr
  name = G4_Sr
  specific = 4
FEATURE [App::DocumentObjectGroupPython] Y_element001  label="Y_element : 1"  # scripted group (container) (typed FeaturePython)
  n = 1
  ref = Y_element
FEATURE [App::DocumentObjectGroupPython] G4_Y  # scripted group (container) (typed FeaturePython)
  Dunit = g/cm3
  Dvalue = 4.469
  Group = -> [Y_element001]
  conduct = 2
  density = 1
  expand = 3
  formula = Y
  name = G4_Y
  specific = 4
FEATURE [App::DocumentObjectGroupPython] Zr_element001  label="Zr_element : 1"  # scripted group (container) (typed FeaturePython)
  n = 1
  ref = Zr_element
FEATURE [App::DocumentObjectGroupPython] G4_Zr  # scripted group (container) (typed FeaturePython)
  Dunit = g/cm3
  Dvalue = 6.506
  Group = -> [Zr_element001]
  conduct = 2
  density = 1
  expand = 3
  formula = Zr
  name = G4_Zr
  specific = 4
FEATURE [App::DocumentObjectGroupPython] Nb_element001  label="Nb_element : 1"  # scripted group (container) (typed FeaturePython)
  n = 1
  ref = Nb_element
FEATURE [App::DocumentObjectGroupPython] G4_Nb  # scripted group (container) (typed FeaturePython)
  Dunit = g/cm3
  Dvalue = 8.57
  Group = -> [Nb_element001]
  conduct = 2
  density = 1
  expand = 3
  formula = Nb
  name = G4_Nb
  specific = 4
FEATURE [App::DocumentObjectGroupPython] Mo_element001  label="Mo_element : 1"  # scripted group (container) (typed FeaturePython)
  n = 1
  ref = Mo_element
FEATURE [App::DocumentObjectGroupPython] G4_Mo  # scripted group (container) (typed FeaturePython)
  Dunit = g/cm3
  Dvalue = 10.22
  Group = -> [Mo_element001]
  conduct = 2
  density = 1
  expand = 3
  formula = Mo
  name = G4_Mo
  specific = 4
FEATURE [App::DocumentObjectGroupPython] Tc_element001  label="Tc_element : 1"  # scripted group (container) (typed FeaturePython)
  n = 1
  ref = Tc_element
FEATURE [App::DocumentObjectGroupPython] G4_Tc  # scripted group (container) (typed FeaturePython)
  Dunit = g/cm3
  Dvalue = 11.5
  Group = -> [Tc_element001]
  conduct = 2
  density = 1
  expand = 3
  formula = Tc
  name = G4_Tc
  specific = 4
FEATURE [App::DocumentObjectGroupPython] Ru_element001  label="Ru_element : 1"  # scripted group (container) (typed FeaturePython)
  n = 1
  ref = Ru_element
FEATURE [App::DocumentObjectGroupPython] G4_Ru  # scripted group (container) (typed FeaturePython)
  Dunit = g/cm3
  Dvalue = 12.41
  Group = -> [Ru_element001]
  conduct = 2
  density = 1
  expand = 3
  formula = Ru
  name = G4_Ru
  specific = 4
FEATURE [App::DocumentObjectGroupPython] Rh_element001  label="Rh_element : 1"  # scripted group (container) (typed FeaturePython)
  n = 1
  ref = Rh_element
FEATURE [App::DocumentObjectGroupPython] G4_Rh  # scripted group (container) (typed FeaturePython)
  Dunit = g/cm3
  Dvalue = 12.41
  Group = -> [Rh_element001]
  conduct = 2
  density = 1
  expand = 3
  formula = Rh
  name = G4_Rh
  specific = 4
FEATURE [App::DocumentObjectGroupPython] Pd_element001  label="Pd_element : 1"  # scripted group (container) (typed FeaturePython)
  n = 1
  ref = Pd_element
FEATURE [App::DocumentObjectGroupPython] G4_Pd  # scripted group (container) (typed FeaturePython)
  Dunit = g/cm3
  Dvalue = 12.02
  Group = -> [Pd_element001]
  conduct = 2
  density = 1
  expand = 3
  formula = Pd
  name = G4_Pd
  specific = 4
FEATURE [App::DocumentObjectGroupPython] Ag_element006  label="Ag_element : 004"  # scripted group (container) (typed FeaturePython)
  n = 1
  ref = Ag_element
FEATURE [App::DocumentObjectGroupPython] G4_Ag  # scripted group (container) (typed FeaturePython)
  Dunit = g/cm3
  Dvalue = 10.5
  Group = -> [Ag_element006]
  conduct = 2
  density = 1
  expand = 3
  formula = Ag
  name = G4_Ag
  specific = 4
FEATURE [App::DocumentObjectGroupPython] Cd_element003  label="Cd_element : 003"  # scripted group (container) (typed FeaturePython)
  n = 1
  ref = Cd_element
FEATURE [App::DocumentObjectGroupPython] G4_Cd  # scripted group (container) (typed FeaturePython)
  Dunit = g/cm3
  Dvalue = 8.65
  Group = -> [Cd_element003]
  conduct = 2
  density = 1
  expand = 3
  formula = Cd
  name = G4_Cd
  specific = 4
FEATURE [App::DocumentObjectGroupPython] In_element001  label="In_element : 1"  # scripted group (container) (typed FeaturePython)
  n = 1
  ref = In_element
FEATURE [App::DocumentObjectGroupPython] G4_In  # scripted group (container) (typed FeaturePython)
  Dunit = g/cm3
  Dvalue = 7.31
  Group = -> [In_element001]
  conduct = 2
  density = 1
  expand = 3
  formula = In
  name = G4_In
  specific = 4
FEATURE [App::DocumentObjectGroupPython] Sn_element001  label="Sn_element : 1"  # scripted group (container) (typed FeaturePython)
  n = 1
  ref = Sn_element
FEATURE [App::DocumentObjectGroupPython] G4_Sn  # scripted group (container) (typed FeaturePython)
  Dunit = g/cm3
  Dvalue = 7.31
  Group = -> [Sn_element001]
  conduct = 2
  density = 1
  expand = 3
  formula = Sn
  name = G4_Sn
  specific = 4
FEATURE [App::DocumentObjectGroupPython] Sb_element001  label="Sb_element : 1"  # scripted group (container) (typed FeaturePython)
  n = 1
  ref = Sb_element
FEATURE [App::DocumentObjectGroupPython] G4_Sb  # scripted group (container) (typed FeaturePython)
  Dunit = g/cm3
  Dvalue = 6.691
  Group = -> [Sb_element001]
  conduct = 2
  density = 1
  expand = 3
  formula = Sb
  name = G4_Sb
  specific = 4
FEATURE [App::DocumentObjectGroupPython] Te_element002  label="Te_element : 002"  # scripted group (container) (typed FeaturePython)
  n = 1
  ref = Te_element
FEATURE [App::DocumentObjectGroupPython] G4_Te  # scripted group (container) (typed FeaturePython)
  Dunit = g/cm3
  Dvalue = 6.24
  Group = -> [Te_element002]
  conduct = 2
  density = 1
  expand = 3
  formula = Te
  name = G4_Te
  specific = 4
FEATURE [App::DocumentObjectGroupPython] I_element010  label="I_element : 006"  # scripted group (container) (typed FeaturePython)
  n = 1
  ref = I_element
FEATURE [App::DocumentObjectGroupPython] G4_I  # scripted group (container) (typed FeaturePython)
  Dunit = g/cm3
  Dvalue = 4.93
  Group = -> [I_element010]
  conduct = 2
  density = 1
  expand = 3
  formula = I
  name = G4_I
  specific = 4
FEATURE [App::DocumentObjectGroupPython] Xe_element001  label="Xe_element : 1"  # scripted group (container) (typed FeaturePython)
  n = 1
  ref = Xe_element
FEATURE [App::DocumentObjectGroupPython] G4_Xe  # scripted group (container) (typed FeaturePython)
  Dunit = g/cm3
  Dvalue = 0.00548536
  Group = -> [Xe_element001]
  conduct = 2
  density = 1
  expand = 3
  formula = Xe
  name = G4_Xe
  specific = 4
FEATURE [App::DocumentObjectGroupPython] Cs_element003  label="Cs_element : 003"  # scripted group (container) (typed FeaturePython)
  n = 1
  ref = Cs_element
FEATURE [App::DocumentObjectGroupPython] G4_Cs  # scripted group (container) (typed FeaturePython)
  Dunit = g/cm3
  Dvalue = 1.873
  Group = -> [Cs_element003]
  conduct = 2
  density = 1
  expand = 3
  formula = Cs
  name = G4_Cs
  specific = 4
FEATURE [App::DocumentObjectGroupPython] Ba_element003  label="Ba_element : 003"  # scripted group (container) (typed FeaturePython)
  n = 1
  ref = Ba_element
FEATURE [App::DocumentObjectGroupPython] G4_Ba  # scripted group (container) (typed FeaturePython)
  Dunit = g/cm3
  Dvalue = 3.5
  Group = -> [Ba_element003]
  conduct = 2
  density = 1
  expand = 3
  formula = Ba
  name = G4_Ba
  specific = 4
FEATURE [App::DocumentObjectGroupPython] La_element003  label="La_element : 003"  # scripted group (container) (typed FeaturePython)
  n = 1
  ref = La_element
FEATURE [App::DocumentObjectGroupPython] G4_La  # scripted group (container) (typed FeaturePython)
  Dunit = g/cm3
  Dvalue = 6.154
  Group = -> [La_element003]
  conduct = 2
  density = 1
  expand = 3
  formula = La
  name = G4_La
  specific = 4
FEATURE [App::DocumentObjectGroupPython] Ce_element002  label="Ce_element : 1"  # scripted group (container) (typed FeaturePython)
  n = 1
  ref = Ce_element
FEATURE [App::DocumentObjectGroupPython] G4_Ce  # scripted group (container) (typed FeaturePython)
  Dunit = g/cm3
  Dvalue = 6.657
  Group = -> [Ce_element002]
  conduct = 2
  density = 1
  expand = 3
  formula = Ce
  name = G4_Ce
  specific = 4
FEATURE [App::DocumentObjectGroupPython] Pr_element001  label="Pr_element : 1"  # scripted group (container) (typed FeaturePython)
  n = 1
  ref = Pr_element
FEATURE [App::DocumentObjectGroupPython] G4_Pr  # scripted group (container) (typed FeaturePython)
  Dunit = g/cm3
  Dvalue = 6.71
  Group = -> [Pr_element001]
  conduct = 2
  density = 1
  expand = 3
  formula = Pr
  name = G4_Pr
  specific = 4
FEATURE [App::DocumentObjectGroupPython] Nd_element001  label="Nd_element : 1"  # scripted group (container) (typed FeaturePython)
  n = 1
  ref = Nd_element
FEATURE [App::DocumentObjectGroupPython] G4_Nd  # scripted group (container) (typed FeaturePython)
  Dunit = g/cm3
  Dvalue = 6.9
  Group = -> [Nd_element001]
  conduct = 2
  density = 1
  expand = 3
  formula = Nd
  name = G4_Nd
  specific = 4
FEATURE [App::DocumentObjectGroupPython] Pm_element001  label="Pm_element : 1"  # scripted group (container) (typed FeaturePython)
  n = 1
  ref = Pm_element
FEATURE [App::DocumentObjectGroupPython] G4_Pm  # scripted group (container) (typed FeaturePython)
  Dunit = g/cm3
  Dvalue = 7.22
  Group = -> [Pm_element001]
  conduct = 2
  density = 1
  expand = 3
  formula = Pm
  name = G4_Pm
  specific = 4
FEATURE [App::DocumentObjectGroupPython] Sm_element001  label="Sm_element : 1"  # scripted group (container) (typed FeaturePython)
  n = 1
  ref = Sm_element
FEATURE [App::DocumentObjectGroupPython] G4_Sm  # scripted group (container) (typed FeaturePython)
  Dunit = g/cm3
  Dvalue = 7.46
  Group = -> [Sm_element001]
  conduct = 2
  density = 1
  expand = 3
  formula = Sm
  name = G4_Sm
  specific = 4
FEATURE [App::DocumentObjectGroupPython] Eu_element001  label="Eu_element : 1"  # scripted group (container) (typed FeaturePython)
  n = 1
  ref = Eu_element
FEATURE [App::DocumentObjectGroupPython] G4_Eu  # scripted group (container) (typed FeaturePython)
  Dunit = g/cm3
  Dvalue = 5.243
  Group = -> [Eu_element001]
  conduct = 2
  density = 1
  expand = 3
  formula = Eu
  name = G4_Eu
  specific = 4
FEATURE [App::DocumentObjectGroupPython] Gd_element002  label="Gd_element : 1"  # scripted group (container) (typed FeaturePython)
  n = 1
  ref = Gd_element
FEATURE [App::DocumentObjectGroupPython] G4_Gd  # scripted group (container) (typed FeaturePython)
  Dunit = g/cm3
  Dvalue = 7.9004
  Group = -> [Gd_element002]
  conduct = 2
  density = 1
  expand = 3
  formula = Gd
  name = G4_Gd
  specific = 4
FEATURE [App::DocumentObjectGroupPython] Tb_element001  label="Tb_element : 1"  # scripted group (container) (typed FeaturePython)
  n = 1
  ref = Tb_element
FEATURE [App::DocumentObjectGroupPython] G4_Tb  # scripted group (container) (typed FeaturePython)
  Dunit = g/cm3
  Dvalue = 8.229
  Group = -> [Tb_element001]
  conduct = 2
  density = 1
  expand = 3
  formula = Tb
  name = G4_Tb
  specific = 4
FEATURE [App::DocumentObjectGroupPython] Dy_element001  label="Dy_element : 1"  # scripted group (container) (typed FeaturePython)
  n = 1
  ref = Dy_element
FEATURE [App::DocumentObjectGroupPython] G4_Dy  # scripted group (container) (typed FeaturePython)
  Dunit = g/cm3
  Dvalue = 8.55
  Group = -> [Dy_element001]
  conduct = 2
  density = 1
  expand = 3
  formula = Dy
  name = G4_Dy
  specific = 4
FEATURE [App::DocumentObjectGroupPython] Ho_element001  label="Ho_element : 1"  # scripted group (container) (typed FeaturePython)
  n = 1
  ref = Ho_element
FEATURE [App::DocumentObjectGroupPython] G4_Ho  # scripted group (container) (typed FeaturePython)
  Dunit = g/cm3
  Dvalue = 8.795
  Group = -> [Ho_element001]
  conduct = 2
  density = 1
  expand = 3
  formula = Ho
  name = G4_Ho
  specific = 4
FEATURE [App::DocumentObjectGroupPython] Er_element001  label="Er_element : 1"  # scripted group (container) (typed FeaturePython)
  n = 1
  ref = Er_element
FEATURE [App::DocumentObjectGroupPython] G4_Er  # scripted group (container) (typed FeaturePython)
  Dunit = g/cm3
  Dvalue = 9.066
  Group = -> [Er_element001]
  conduct = 2
  density = 1
  expand = 3
  formula = Er
  name = G4_Er
  specific = 4
FEATURE [App::DocumentObjectGroupPython] Tm_element001  label="Tm_element : 1"  # scripted group (container) (typed FeaturePython)
  n = 1
  ref = Tm_element
FEATURE [App::DocumentObjectGroupPython] G4_Tm  # scripted group (container) (typed FeaturePython)
  Dunit = g/cm3
  Dvalue = 9.321
  Group = -> [Tm_element001]
  conduct = 2
  density = 1
  expand = 3
  formula = Tm
  name = G4_Tm
  specific = 4
FEATURE [App::DocumentObjectGroupPython] Yb_element001  label="Yb_element : 1"  # scripted group (container) (typed FeaturePython)
  n = 1
  ref = Yb_element
FEATURE [App::DocumentObjectGroupPython] G4_Yb  # scripted group (container) (typed FeaturePython)
  Dunit = g/cm3
  Dvalue = 6.73
  Group = -> [Yb_element001]
  conduct = 2
  density = 1
  expand = 3
  formula = Yb
  name = G4_Yb
  specific = 4
FEATURE [App::DocumentObjectGroupPython] Lu_element001  label="Lu_element : 1"  # scripted group (container) (typed FeaturePython)
  n = 1
  ref = Lu_element
FEATURE [App::DocumentObjectGroupPython] G4_Lu  # scripted group (container) (typed FeaturePython)
  Dunit = g/cm3
  Dvalue = 9.84
  Group = -> [Lu_element001]
  conduct = 2
  density = 1
  expand = 3
  formula = Lu
  name = G4_Lu
  specific = 4
FEATURE [App::DocumentObjectGroupPython] Hf_element001  label="Hf_element : 1"  # scripted group (container) (typed FeaturePython)
  n = 1
  ref = Hf_element
FEATURE [App::DocumentObjectGroupPython] G4_Hf  # scripted group (container) (typed FeaturePython)
  Dunit = g/cm3
  Dvalue = 13.31
  Group = -> [Hf_element001]
  conduct = 2
  density = 1
  expand = 3
  formula = Hf
  name = G4_Hf
  specific = 4
FEATURE [App::DocumentObjectGroupPython] Ta_element001  label="Ta_element : 1"  # scripted group (container) (typed FeaturePython)
  n = 1
  ref = Ta_element
FEATURE [App::DocumentObjectGroupPython] G4_Ta  # scripted group (container) (typed FeaturePython)
  Dunit = g/cm3
  Dvalue = 16.654
  Group = -> [Ta_element001]
  conduct = 2
  density = 1
  expand = 3
  formula = Ta
  name = G4_Ta
  specific = 4
FEATURE [App::DocumentObjectGroupPython] W_element004  label="W_element : 004"  # scripted group (container) (typed FeaturePython)
  n = 1
  ref = W_element
FEATURE [App::DocumentObjectGroupPython] G4_W  # scripted group (container) (typed FeaturePython)
  Dunit = g/cm3
  Dvalue = 19.3
  Group = -> [W_element004]
  conduct = 2
  density = 1
  expand = 3
  formula = W
  name = G4_W
  specific = 4
FEATURE [App::DocumentObjectGroupPython] Re_element001  label="Re_element : 1"  # scripted group (container) (typed FeaturePython)
  n = 1
  ref = Re_element
FEATURE [App::DocumentObjectGroupPython] G4_Re  # scripted group (container) (typed FeaturePython)
  Dunit = g/cm3
  Dvalue = 21.02
  Group = -> [Re_element001]
  conduct = 2
  density = 1
  expand = 3
  formula = Re
  name = G4_Re
  specific = 4
FEATURE [App::DocumentObjectGroupPython] Os_element001  label="Os_element : 1"  # scripted group (container) (typed FeaturePython)
  n = 1
  ref = Os_element
FEATURE [App::DocumentObjectGroupPython] G4_Os  # scripted group (container) (typed FeaturePython)
  Dunit = g/cm3
  Dvalue = 22.57
  Group = -> [Os_element001]
  conduct = 2
  density = 1
  expand = 3
  formula = Os
  name = G4_Os
  specific = 4
FEATURE [App::DocumentObjectGroupPython] Ir_element001  label="Ir_element : 1"  # scripted group (container) (typed FeaturePython)
  n = 1
  ref = Ir_element
FEATURE [App::DocumentObjectGroupPython] G4_Ir  # scripted group (container) (typed FeaturePython)
  Dunit = g/cm3
  Dvalue = 22.42
  Group = -> [Ir_element001]
  conduct = 2
  density = 1
  expand = 3
  formula = Ir
  name = G4_Ir
  specific = 4
FEATURE [App::DocumentObjectGroupPython] Pt_element001  label="Pt_element : 1"  # scripted group (container) (typed FeaturePython)
  n = 1
  ref = Pt_element
FEATURE [App::DocumentObjectGroupPython] G4_Pt  # scripted group (container) (typed FeaturePython)
  Dunit = g/cm3
  Dvalue = 21.45
  Group = -> [Pt_element001]
  conduct = 2
  density = 1
  expand = 3
  formula = Pt
  name = G4_Pt
  specific = 4
FEATURE [App::DocumentObjectGroupPython] Au_element001  label="Au_element : 1"  # scripted group (container) (typed FeaturePython)
  n = 1
  ref = Au_element
FEATURE [App::DocumentObjectGroupPython] G4_Au  # scripted group (container) (typed FeaturePython)
  Dunit = g/cm3
  Dvalue = 19.32
  Group = -> [Au_element001]
  conduct = 2
  density = 1
  expand = 3
  formula = Au
  name = G4_Au
  specific = 4
FEATURE [App::DocumentObjectGroupPython] Hg_element002  label="Hg_element : 002"  # scripted group (container) (typed FeaturePython)
  n = 1
  ref = Hg_element
FEATURE [App::DocumentObjectGroupPython] G4_Hg  # scripted group (container) (typed FeaturePython)
  Dunit = g/cm3
  Dvalue = 13.546
  Group = -> [Hg_element002]
  conduct = 2
  density = 1
  expand = 3
  formula = Hg
  name = G4_Hg
  specific = 4
FEATURE [App::DocumentObjectGroupPython] Tl_element002  label="Tl_element : 002"  # scripted group (container) (typed FeaturePython)
  n = 1
  ref = Tl_element
FEATURE [App::DocumentObjectGroupPython] G4_Tl  # scripted group (container) (typed FeaturePython)
  Dunit = g/cm3
  Dvalue = 11.72
  Group = -> [Tl_element002]
  conduct = 2
  density = 1
  expand = 3
  formula = Tl
  name = G4_Tl
  specific = 4
FEATURE [App::DocumentObjectGroupPython] Pb_element003  label="Pb_element : 1"  # scripted group (container) (typed FeaturePython)
  n = 1
  ref = Pb_element
FEATURE [App::DocumentObjectGroupPython] G4_Pb  # scripted group (container) (typed FeaturePython)
  Dunit = g/cm3
  Dvalue = 11.35
  Group = -> [Pb_element003]
  conduct = 2
  density = 1
  expand = 3
  formula = Pb
  name = G4_Pb
  specific = 4
FEATURE [App::DocumentObjectGroupPython] Bi_element002  label="Bi_element : 1"  # scripted group (container) (typed FeaturePython)
  n = 1
  ref = Bi_element
FEATURE [App::DocumentObjectGroupPython] G4_Bi  # scripted group (container) (typed FeaturePython)
  Dunit = g/cm3
  Dvalue = 9.747
  Group = -> [Bi_element002]
  conduct = 2
  density = 1
  expand = 3
  formula = Bi
  name = G4_Bi
  specific = 4
FEATURE [App::DocumentObjectGroupPython] Po_element001  label="Po_element : 1"  # scripted group (container) (typed FeaturePython)
  n = 1
  ref = Po_element
FEATURE [App::DocumentObjectGroupPython] G4_Po  # scripted group (container) (typed FeaturePython)
  Dunit = g/cm3
  Dvalue = 9.32
  Group = -> [Po_element001]
  conduct = 2
  density = 1
  expand = 3
  formula = Po
  name = G4_Po
  specific = 4
FEATURE [App::DocumentObjectGroupPython] At_element001  label="At_element : 1"  # scripted group (container) (typed FeaturePython)
  n = 1
  ref = At_element
FEATURE [App::DocumentObjectGroupPython] G4_At  # scripted group (container) (typed FeaturePython)
  Dunit = g/cm3
  Dvalue = 9.32
  Group = -> [At_element001]
  conduct = 2
  density = 1
  expand = 3
  formula = At
  name = G4_At
  specific = 4
FEATURE [App::DocumentObjectGroupPython] Rn_element001  label="Rn_element : 1"  # scripted group (container) (typed FeaturePython)
  n = 1
  ref = Rn_element
FEATURE [App::DocumentObjectGroupPython] G4_Rn  # scripted group (container) (typed FeaturePython)
  Dunit = g/cm3
  Dvalue = 0.00900662
  Group = -> [Rn_element001]
  conduct = 2
  density = 1
  expand = 3
  formula = Rn
  name = G4_Rn
  specific = 4
FEATURE [App::DocumentObjectGroupPython] Fr_element001  label="Fr_element : 1"  # scripted group (container) (typed FeaturePython)
  n = 1
  ref = Fr_element
FEATURE [App::DocumentObjectGroupPython] G4_Fr  # scripted group (container) (typed FeaturePython)
  Dunit = g/cm3
  Dvalue = 1
  Group = -> [Fr_element001]
  conduct = 2
  density = 1
  expand = 3
  formula = Fr
  name = G4_Fr
  specific = 4
FEATURE [App::DocumentObjectGroupPython] Ra_element001  label="Ra_element : 1"  # scripted group (container) (typed FeaturePython)
  n = 1
  ref = Ra_element
FEATURE [App::DocumentObjectGroupPython] G4_Ra  # scripted group (container) (typed FeaturePython)
  Dunit = g/cm3
  Dvalue = 5
  Group = -> [Ra_element001]
  conduct = 2
  density = 1
  expand = 3
  formula = Ra
  name = G4_Ra
  specific = 4
FEATURE [App::DocumentObjectGroupPython] Ac_element001  label="Ac_element : 1"  # scripted group (container) (typed FeaturePython)
  n = 1
  ref = Ac_element
FEATURE [App::DocumentObjectGroupPython] G4_Ac  # scripted group (container) (typed FeaturePython)
  Dunit = g/cm3
  Dvalue = 10.07
  Group = -> [Ac_element001]
  conduct = 2
  density = 1
  expand = 3
  formula = Ac
  name = G4_Ac
  specific = 4
FEATURE [App::DocumentObjectGroupPython] Th_element001  label="Th_element : 1"  # scripted group (container) (typed FeaturePython)
  n = 1
  ref = Th_element
FEATURE [App::DocumentObjectGroupPython] G4_Th  # scripted group (container) (typed FeaturePython)
  Dunit = g/cm3
  Dvalue = 11.72
  Group = -> [Th_element001]
  conduct = 2
  density = 1
  expand = 3
  formula = Th
  name = G4_Th
  specific = 4
FEATURE [App::DocumentObjectGroupPython] Pa_element001  label="Pa_element : 1"  # scripted group (container) (typed FeaturePython)
  n = 1
  ref = Pa_element
FEATURE [App::DocumentObjectGroupPython] G4_Pa  # scripted group (container) (typed FeaturePython)
  Dunit = g/cm3
  Dvalue = 15.37
  Group = -> [Pa_element001]
  conduct = 2
  density = 1
  expand = 3
  formula = Pa
  name = G4_Pa
  specific = 4
FEATURE [App::DocumentObjectGroupPython] U_element004  label="U_element : 004"  # scripted group (container) (typed FeaturePython)
  n = 1
  ref = U_element
FEATURE [App::DocumentObjectGroupPython] G4_U  # scripted group (container) (typed FeaturePython)
  Dunit = g/cm3
  Dvalue = 18.95
  Group = -> [U_element004]
  conduct = 2
  density = 1
  expand = 3
  formula = U
  name = G4_U
  specific = 4
FEATURE [App::DocumentObjectGroupPython] Np_element001  label="Np_element : 1"  # scripted group (container) (typed FeaturePython)
  n = 1
  ref = Np_element
FEATURE [App::DocumentObjectGroupPython] G4_Np  # scripted group (container) (typed FeaturePython)
  Dunit = g/cm3
  Dvalue = 20.25
  Group = -> [Np_element001]
  conduct = 2
  density = 1
  expand = 3
  formula = Np
  name = G4_Np
  specific = 4
FEATURE [App::DocumentObjectGroupPython] Pu_element002  label="Pu_element : 002"  # scripted group (container) (typed FeaturePython)
  n = 1
  ref = Pu_element
FEATURE [App::DocumentObjectGroupPython] G4_Pu  # scripted group (container) (typed FeaturePython)
  Dunit = g/cm3
  Dvalue = 19.84
  Group = -> [Pu_element002]
  conduct = 2
  density = 1
  expand = 3
  formula = Pu
  name = G4_Pu
  specific = 4
FEATURE [App::DocumentObjectGroupPython] Am_element001  label="Am_element : 1"  # scripted group (container) (typed FeaturePython)
  n = 1
  ref = Am_element
FEATURE [App::DocumentObjectGroupPython] G4_Am  # scripted group (container) (typed FeaturePython)
  Dunit = g/cm3
  Dvalue = 13.67
  Group = -> [Am_element001]
  conduct = 2
  density = 1
  expand = 3
  formula = Am
  name = G4_Am
  specific = 4
FEATURE [App::DocumentObjectGroupPython] Cm_element001  label="Cm_element : 1"  # scripted group (container) (typed FeaturePython)
  n = 1
  ref = Cm_element
FEATURE [App::DocumentObjectGroupPython] G4_Cm  # scripted group (container) (typed FeaturePython)
  Dunit = g/cm3
  Dvalue = 13.51
  Group = -> [Cm_element001]
  conduct = 2
  density = 1
  expand = 3
  formula = Cm
  name = G4_Cm
  specific = 4
FEATURE [App::DocumentObjectGroupPython] Bk_element001  label="Bk_element : 1"  # scripted group (container) (typed FeaturePython)
  n = 1
  ref = Bk_element
FEATURE [App::DocumentObjectGroupPython] G4_Bk  # scripted group (container) (typed FeaturePython)
  Dunit = g/cm3
  Dvalue = 14
  Group = -> [Bk_element001]
  conduct = 2
  density = 1
  expand = 3
  formula = Bk
  name = G4_Bk
  specific = 4
FEATURE [App::DocumentObjectGroupPython] Cf_element001  label="Cf_element : 1"  # scripted group (container) (typed FeaturePython)
  n = 1
  ref = Cf_element
FEATURE [App::DocumentObjectGroupPython] G4_Cf  # scripted group (container) (typed FeaturePython)
  Dunit = g/cm3
  Dvalue = 10
  Group = -> [Cf_element001]
  conduct = 2
  density = 1
  expand = 3
  formula = Cf
  name = G4_Cf
  specific = 4
FEATURE [App::DocumentObjectGroupPython] Element  # scripted group (container) (typed FeaturePython)
  Group = -> [G4_H,G4_He,G4_Li,G4_Be,G4_B,G4_C,G4_N,G4_O,G4_F,G4_Ne,G4_Na,G4_Mg,G4_Al,G4_Si,G4_P,G4_S,G4_Cl,G4_Ar,G4_K,G4_Ca,G4_Sc,G4_Ti,G4_V,G4_Cr,G4_Mn,G4_Fe,G4_Co,G4_Ni,G4_Cu,G4_Zn,G4_Ga,G4_Ge,G4_As,G4_Se,G4_Br,G4_Kr,G4_Rb,G4_Sr,G4_Y,G4_Zr,G4_Nb,G4_Mo,G4_Tc,G4_Ru,G4_Rh,G4_Pd,G4_Ag,G4_Cd,G4_In,G4_Sn,G4_Sb,G4_Te,G4_I,G4_Xe,G4_Cs,G4_Ba,G4_La,G4_Ce,G4_Pr,G4_Nd,G4_Pm,G4_Sm,G4_Eu,G4_Gd,G4_Tb,G4_Dy,G4_Ho,G4_Er,+30 more]
FEATURE [App::DocumentObjectGroupPython] H_element114  label="H_element : 063"  # scripted group (container) (typed FeaturePython)
  n = 2
  ref = H_element
FEATURE [App::DocumentObjectGroupPython] G4_lH2  # scripted group (container) (typed FeaturePython)
  Dunit = g/cm3
  Dvalue = 0.0708
  Group = -> [H_element114]
  conduct = 2
  density = 1
  expand = 3
  formula = G4_lH2
  name = G4_lH2
  specific = 4
FEATURE [App::DocumentObjectGroupPython] N_element049  label="N_element : 022"  # scripted group (container) (typed FeaturePython)
  n = 2
  ref = N_element
FEATURE [App::DocumentObjectGroupPython] G4_lN2  # scripted group (container) (typed FeaturePython)
  Dunit = g/cm3
  Dvalue = 0.807
  Group = -> [N_element049]
  conduct = 2
  density = 1
  expand = 3
  formula = G4_lN2
  name = G4_lN2
  specific = 4
FEATURE [App::DocumentObjectGroupPython] O_element106  label="O_element : 060"  # scripted group (container) (typed FeaturePython)
  n = 2
  ref = O_element
FEATURE [App::DocumentObjectGroupPython] G4_lO2  # scripted group (container) (typed FeaturePython)
  Dunit = g/cm3
  Dvalue = 1.141
  Group = -> [O_element106]
  conduct = 2
  density = 1
  expand = 3
  formula = G4_lO2
  name = G4_lO2
  specific = 4
FEATURE [App::DocumentObjectGroupPython] Ar  label="Ar : 1"  # scripted group (container) (typed FeaturePython)
  n = 1
  ref = Ar
FEATURE [App::DocumentObjectGroupPython] G4_lAr  # scripted group (container) (typed FeaturePython)
  Dunit = g/cm3
  Dvalue = 1.396
  Group = -> [Ar]
  conduct = 2
  density = 1
  expand = 3
  formula = G4_lAr
  name = G4_lAr
  specific = 4
FEATURE [App::DocumentObjectGroupPython] Br  label="Br : 1"  # scripted group (container) (typed FeaturePython)
  n = 1
  ref = Br
FEATURE [App::DocumentObjectGroupPython] G4_lBr  # scripted group (container) (typed FeaturePython)
  Dunit = g/cm3
  Dvalue = 3.1028
  Group = -> [Br]
  conduct = 2
  density = 1
  expand = 3
  formula = G4_lBr
  name = G4_lBr
  specific = 4
FEATURE [App::DocumentObjectGroupPython] Kr  label="Kr : 1"  # scripted group (container) (typed FeaturePython)
  n = 1
  ref = Kr
FEATURE [App::DocumentObjectGroupPython] G4_lKr  # scripted group (container) (typed FeaturePython)
  Dunit = g/cm3
  Dvalue = 2.418
  Group = -> [Kr]
  conduct = 2
  density = 1
  expand = 3
  formula = G4_lKr
  name = G4_lKr
  specific = 4
FEATURE [App::DocumentObjectGroupPython] Xe  label="Xe : 1"  # scripted group (container) (typed FeaturePython)
  n = 1
  ref = Xe
FEATURE [App::DocumentObjectGroupPython] G4_lXe  # scripted group (container) (typed FeaturePython)
  Dunit = g/cm3
  Dvalue = 2.953
  Group = -> [Xe]
  conduct = 2
  density = 1
  expand = 3
  formula = G4_lXe
  name = G4_lXe
  specific = 4
FEATURE [App::DocumentObjectGroupPython] O_element107  label="O_element : 061"  # scripted group (container) (typed FeaturePython)
  n = 4
  ref = O_element
FEATURE [App::DocumentObjectGroupPython] Pb_element004  label="Pb_element : 002"  # scripted group (container) (typed FeaturePython)
  n = 1
  ref = Pb_element
FEATURE [App::DocumentObjectGroupPython] W_element005  label="W_element : 005"  # scripted group (container) (typed FeaturePython)
  n = 1
  ref = W_element
FEATURE [App::DocumentObjectGroupPython] G4_PbWO4  # scripted group (container) (typed FeaturePython)
  Dunit = g/cm3
  Dvalue = 8.28
  Group = -> [O_element107,Pb_element004,W_element005]
  conduct = 2
  density = 1
  expand = 3
  formula = G4_PbWO4
  name = G4_PbWO4
  specific = 4
FEATURE [App::DocumentObjectGroupPython] alactic  label="alactic : 1"  # scripted group (container) (typed FeaturePython)
  n = 1
  ref = alactic
FEATURE [App::DocumentObjectGroupPython] G4_Galactic  # scripted group (container) (typed FeaturePython)
  Dunit = g/cm3
  Dvalue = 0
  Group = -> [alactic]
  conduct = 2
  density = 1
  expand = 3
  formula = G4_Galactic
  name = G4_Galactic
  specific = 4
FEATURE [App::DocumentObjectGroupPython] RAPHITE_POROUS  label="RAPHITE_POROUS : 1"  # scripted group (container) (typed FeaturePython)
  n = 1
  ref = RAPHITE_POROUS
FEATURE [App::DocumentObjectGroupPython] G4_GRAPHITE_POROUS  # scripted group (container) (typed FeaturePython)
  Dunit = g/cm3
  Dvalue = 1.7
  Group = -> [RAPHITE_POROUS]
  conduct = 2
  density = 1
  expand = 3
  formula = G4_GRAPHITE_POROUS
  name = G4_GRAPHITE_POROUS
  specific = 4
FEATURE [App::DocumentObjectGroupPython] H_element115  label="H_element : 0.150"  # scripted group (container) (typed FeaturePython)
  n = 0.080538
FEATURE [App::DocumentObjectGroupPython] C_element125  label="C_element : 0.600"  # scripted group (container) (typed FeaturePython)
  n = 0.599848
FEATURE [App::DocumentObjectGroupPython] O_element108  label="O_element : 0.320"  # scripted group (container) (typed FeaturePython)
  n = 0.319614
FEATURE [App::DocumentObjectGroupPython] G4_LUCITE  # scripted group (container) (typed FeaturePython)
  Dunit = g/cm3
  Dvalue = 1.19
  Group = -> [H_element115,C_element125,O_element108]
  conduct = 2
  density = 1
  expand = 3
  formula = G4_LUCITE
  name = G4_LUCITE
  specific = 4
FEATURE [App::DocumentObjectGroupPython] Cu_element002  label="Cu_element : 62"  # scripted group (container) (typed FeaturePython)
  n = 62
  ref = Cu_element
FEATURE [App::DocumentObjectGroupPython] Zn_element002  label="Zn_element : 35"  # scripted group (container) (typed FeaturePython)
  n = 35
  ref = Zn_element
FEATURE [App::DocumentObjectGroupPython] Pb_element005  label="Pb_element : 3"  # scripted group (container) (typed FeaturePython)
  n = 3
  ref = Pb_element
FEATURE [App::DocumentObjectGroupPython] G4_BRASS  # scripted group (container) (typed FeaturePython)
  Dunit = g/cm3
  Dvalue = 8.52
  Group = -> [Cu_element002,Zn_element002,Pb_element005]
  conduct = 2
  density = 1
  expand = 3
  formula = G4_BRASS
  name = G4_BRASS
  specific = 4
FEATURE [App::DocumentObjectGroupPython] Cu_element003  label="Cu_element : 89"  # scripted group (container) (typed FeaturePython)
  n = 89
  ref = Cu_element
FEATURE [App::DocumentObjectGroupPython] Zn_element003  label="Zn_element : 9"  # scripted group (container) (typed FeaturePython)
  n = 9
  ref = Zn_element
FEATURE [App::DocumentObjectGroupPython] Pb_element006  label="Pb_element : 2"  # scripted group (container) (typed FeaturePython)
  n = 2
  ref = Pb_element
FEATURE [App::DocumentObjectGroupPython] G4_BRONZE  # scripted group (container) (typed FeaturePython)
  Dunit = g/cm3
  Dvalue = 8.82
  Group = -> [Cu_element003,Zn_element003,Pb_element006]
  conduct = 2
  density = 1
  expand = 3
  formula = G4_BRONZE
  name = G4_BRONZE
  specific = 4
FEATURE [App::DocumentObjectGroupPython] Fe_element008  label="Fe_element : 74"  # scripted group (container) (typed FeaturePython)
  n = 74
  ref = Fe_element
FEATURE [App::DocumentObjectGroupPython] Cr_element002  label="Cr_element : 18"  # scripted group (container) (typed FeaturePython)
  n = 18
  ref = Cr_element
FEATURE [App::DocumentObjectGroupPython] Ni_element002  label="Ni_element : 8"  # scripted group (container) (typed FeaturePython)
  n = 8
  ref = Ni_element
FEATURE [App::DocumentObjectGroupPython] G4_STAINLESS_STEEL  label="G4_STAINLESS-STEEL"  # scripted group (container) (typed FeaturePython)
  Dunit = g/cm3
  Dvalue = 8
  Group = -> [Fe_element008,Cr_element002,Ni_element002]
  conduct = 2
  density = 1
  expand = 3
  formula = G4_STAINLESS-STEEL
  name = G4_STAINLESS-STEEL
  specific = 4
FEATURE [App::DocumentObjectGroupPython] H_element116  label="H_element : 064"  # scripted group (container) (typed FeaturePython)
  n = 18
  ref = H_element
FEATURE [App::DocumentObjectGroupPython] C_element126  label="C_element : 071"  # scripted group (container) (typed FeaturePython)
  n = 12
  ref = C_element
FEATURE [App::DocumentObjectGroupPython] O_element109  label="O_element : 062"  # scripted group (container) (typed FeaturePython)
  n = 7
  ref = O_element
FEATURE [App::DocumentObjectGroupPython] G4_CR39  # scripted group (container) (typed FeaturePython)
  Dunit = g/cm3
  Dvalue = 1.32
  Group = -> [H_element116,C_element126,O_element109]
  conduct = 2
  density = 1
  expand = 3
  formula = G4_CR39
  name = G4_CR39
  specific = 4
FEATURE [App::DocumentObjectGroupPython] H_element117  label="H_element : 38"  # scripted group (container) (typed FeaturePython)
  n = 38
  ref = H_element
FEATURE [App::DocumentObjectGroupPython] C_element127  label="C_element : 072"  # scripted group (container) (typed FeaturePython)
  n = 18
  ref = C_element
FEATURE [App::DocumentObjectGroupPython] O_element110  label="O_element : 063"  # scripted group (container) (typed FeaturePython)
  n = 1
  ref = O_element
FEATURE [App::DocumentObjectGroupPython] G4_OCTADECANOL  # scripted group (container) (typed FeaturePython)
  Dunit = g/cm3
  Dvalue = 0.812
  Group = -> [H_element117,C_element127,O_element110]
  conduct = 2
  density = 1
  expand = 3
  formula = G4_OCTADECANOL
  name = G4_OCTADECANOL
  specific = 4
FEATURE [App::DocumentObjectGroupPython] HEP  # scripted group (container) (typed FeaturePython)
  Group = -> [G4_lH2,G4_lN2,G4_lO2,G4_lAr,G4_lBr,G4_lKr,G4_lXe,G4_PbWO4,G4_Galactic,G4_GRAPHITE_POROUS,G4_LUCITE,G4_BRASS,G4_BRONZE,G4_STAINLESS_STEEL,G4_CR39,G4_OCTADECANOL]
FEATURE [App::DocumentObjectGroupPython] C_element128  label="C_element : 073"  # scripted group (container) (typed FeaturePython)
  n = 14
  ref = C_element
FEATURE [App::DocumentObjectGroupPython] H_element118  label="H_element : 065"  # scripted group (container) (typed FeaturePython)
  n = 10
  ref = H_element
FEATURE [App::DocumentObjectGroupPython] O_element111  label="O_element : 064"  # scripted group (container) (typed FeaturePython)
  n = 2
  ref = O_element
FEATURE [App::DocumentObjectGroupPython] N_element050  label="N_element : 023"  # scripted group (container) (typed FeaturePython)
  n = 2
  ref = N_element
FEATURE [App::DocumentObjectGroupPython] G4_KEVLAR  # scripted group (container) (typed FeaturePython)
  Dunit = g/cm3
  Dvalue = 1.44
  Group = -> [C_element128,H_element118,O_element111,N_element050]
  conduct = 2
  density = 1
  expand = 3
  formula = G4_KEVLAR
  name = G4_KEVLAR
  specific = 4
FEATURE [App::DocumentObjectGroupPython] C_element129  label="C_element : 074"  # scripted group (container) (typed FeaturePython)
  n = 10
  ref = C_element
FEATURE [App::DocumentObjectGroupPython] H_element119  label="H_element : 066"  # scripted group (container) (typed FeaturePython)
  n = 8
  ref = H_element
FEATURE [App::DocumentObjectGroupPython] O_element112  label="O_element : 065"  # scripted group (container) (typed FeaturePython)
  n = 4
  ref = O_element
FEATURE [App::DocumentObjectGroupPython] G4_DACRON  # scripted group (container) (typed FeaturePython)
  Dunit = g/cm3
  Dvalue = 1.4
  Group = -> [C_element129,H_element119,O_element112]
  conduct = 2
  density = 1
  expand = 3
  formula = G4_DACRON
  name = G4_DACRON
  specific = 4
FEATURE [App::DocumentObjectGroupPython] C_element130  label="C_element : 075"  # scripted group (container) (typed FeaturePython)
  n = 4
  ref = C_element
FEATURE [App::DocumentObjectGroupPython] H_element120  label="H_element : 067"  # scripted group (container) (typed FeaturePython)
  n = 5
  ref = H_element
FEATURE [App::DocumentObjectGroupPython] Cl_element030  label="Cl_element : 016"  # scripted group (container) (typed FeaturePython)
  n = 1
  ref = Cl_element
FEATURE [App::DocumentObjectGroupPython] G4_NEOPRENE  # scripted group (container) (typed FeaturePython)
  Dunit = g/cm3
  Dvalue = 1.23
  Group = -> [C_element130,H_element120,Cl_element030]
  conduct = 2
  density = 1
  expand = 3
  formula = G4_NEOPRENE
  name = G4_NEOPRENE
  specific = 4
FEATURE [App::DocumentObjectGroupPython] Space  # scripted group (container) (typed FeaturePython)
  Group = -> [G4_KEVLAR,G4_DACRON,G4_NEOPRENE]
FEATURE [App::DocumentObjectGroupPython] H_element121  label="H_element : 068"  # scripted group (container) (typed FeaturePython)
  n = 5
  ref = H_element
FEATURE [App::DocumentObjectGroupPython] C_element131  label="C_element : 076"  # scripted group (container) (typed FeaturePython)
  n = 4
  ref = C_element
FEATURE [App::DocumentObjectGroupPython] N_element051  label="N_element : 3"  # scripted group (container) (typed FeaturePython)
  n = 3
  ref = N_element
FEATURE [App::DocumentObjectGroupPython] O_element113  label="O_element : 066"  # scripted group (container) (typed FeaturePython)
  n = 1
  ref = O_element
FEATURE [App::DocumentObjectGroupPython] G4_CYTOSINE  # scripted group (container) (typed FeaturePython)
  Dunit = g/cm3
  Dvalue = 1.55
  Group = -> [H_element121,C_element131,N_element051,O_element113]
  conduct = 2
  density = 1
  expand = 3
  formula = G4_CYTOSINE
  name = G4_CYTOSINE
  specific = 4
FEATURE [App::DocumentObjectGroupPython] H_element122  label="H_element : 069"  # scripted group (container) (typed FeaturePython)
  n = 6
  ref = H_element
FEATURE [App::DocumentObjectGroupPython] C_element132  label="C_element : 077"  # scripted group (container) (typed FeaturePython)
  n = 5
  ref = C_element
FEATURE [App::DocumentObjectGroupPython] N_element052  label="N_element : 024"  # scripted group (container) (typed FeaturePython)
  n = 2
  ref = N_element
FEATURE [App::DocumentObjectGroupPython] O_element114  label="O_element : 067"  # scripted group (container) (typed FeaturePython)
  n = 2
  ref = O_element
FEATURE [App::DocumentObjectGroupPython] G4_THYMINE  # scripted group (container) (typed FeaturePython)
  Dunit = g/cm3
  Dvalue = 1.23
  Group = -> [H_element122,C_element132,N_element052,O_element114]
  conduct = 2
  density = 1
  expand = 3
  formula = G4_THYMINE
  name = G4_THYMINE
  specific = 4
FEATURE [App::DocumentObjectGroupPython] H_element123  label="H_element : 070"  # scripted group (container) (typed FeaturePython)
  n = 4
  ref = H_element
FEATURE [App::DocumentObjectGroupPython] C_element133  label="C_element : 078"  # scripted group (container) (typed FeaturePython)
  n = 4
  ref = C_element
FEATURE [App::DocumentObjectGroupPython] N_element053  label="N_element : 025"  # scripted group (container) (typed FeaturePython)
  n = 2
  ref = N_element
FEATURE [App::DocumentObjectGroupPython] O_element115  label="O_element : 068"  # scripted group (container) (typed FeaturePython)
  n = 2
  ref = O_element
FEATURE [App::DocumentObjectGroupPython] G4_URACIL  # scripted group (container) (typed FeaturePython)
  Dunit = g/cm3
  Dvalue = 1.32
  Group = -> [H_element123,C_element133,N_element053,O_element115]
  conduct = 2
  density = 1
  expand = 3
  formula = G4_URACIL
  name = G4_URACIL
  specific = 4
FEATURE [App::DocumentObjectGroupPython] H_element124  label="H_element : 071"  # scripted group (container) (typed FeaturePython)
  n = 4
  ref = H_element
FEATURE [App::DocumentObjectGroupPython] C_element134  label="C_element : 079"  # scripted group (container) (typed FeaturePython)
  n = 5
  ref = C_element
FEATURE [App::DocumentObjectGroupPython] N_element054  label="N_element : 026"  # scripted group (container) (typed FeaturePython)
  n = 5
  ref = N_element
FEATURE [App::DocumentObjectGroupPython] G4_DNA_ADENINE  # scripted group (container) (typed FeaturePython)
  Dunit = g/cm3
  Dvalue = 1
  Group = -> [H_element124,C_element134,N_element054]
  conduct = 2
  density = 1
  expand = 3
  formula = G4_DNA_ADENINE
  name = G4_DNA_ADENINE
  specific = 4
FEATURE [App::DocumentObjectGroupPython] H_element125  label="H_element : 072"  # scripted group (container) (typed FeaturePython)
  n = 4
  ref = H_element
FEATURE [App::DocumentObjectGroupPython] C_element135  label="C_element : 080"  # scripted group (container) (typed FeaturePython)
  n = 5
  ref = C_element
FEATURE [App::DocumentObjectGroupPython] N_element055  label="N_element : 027"  # scripted group (container) (typed FeaturePython)
  n = 5
  ref = N_element
FEATURE [App::DocumentObjectGroupPython] O_element116  label="O_element : 069"  # scripted group (container) (typed FeaturePython)
  n = 1
  ref = O_element
FEATURE [App::DocumentObjectGroupPython] G4_DNA_GUANINE  # scripted group (container) (typed FeaturePython)
  Dunit = g/cm3
  Dvalue = 1
  Group = -> [H_element125,C_element135,N_element055,O_element116]
  conduct = 2
  density = 1
  expand = 3
  formula = G4_DNA_GUANINE
  name = G4_DNA_GUANINE
  specific = 4
FEATURE [App::DocumentObjectGroupPython] H_element126  label="H_element : 073"  # scripted group (container) (typed FeaturePython)
  n = 4
  ref = H_element
FEATURE [App::DocumentObjectGroupPython] C_element136  label="C_element : 081"  # scripted group (container) (typed FeaturePython)
  n = 4
  ref = C_element
FEATURE [App::DocumentObjectGroupPython] N_element056  label="N_element : 028"  # scripted group (container) (typed FeaturePython)
  n = 3
  ref = N_element
FEATURE [App::DocumentObjectGroupPython] O_element117  label="O_element : 070"  # scripted group (container) (typed FeaturePython)
  n = 1
  ref = O_element
FEATURE [App::DocumentObjectGroupPython] G4_DNA_CYTOSINE  # scripted group (container) (typed FeaturePython)
  Dunit = g/cm3
  Dvalue = 1
  Group = -> [H_element126,C_element136,N_element056,O_element117]
  conduct = 2
  density = 1
  expand = 3
  formula = G4_DNA_CYTOSINE
  name = G4_DNA_CYTOSINE
  specific = 4
FEATURE [App::DocumentObjectGroupPython] H_element127  label="H_element : 074"  # scripted group (container) (typed FeaturePython)
  n = 5
  ref = H_element
FEATURE [App::DocumentObjectGroupPython] C_element137  label="C_element : 082"  # scripted group (container) (typed FeaturePython)
  n = 5
  ref = C_element
FEATURE [App::DocumentObjectGroupPython] N_element057  label="N_element : 029"  # scripted group (container) (typed FeaturePython)
  n = 2
  ref = N_element
FEATURE [App::DocumentObjectGroupPython] O_element118  label="O_element : 071"  # scripted group (container) (typed FeaturePython)
  n = 2
  ref = O_element
FEATURE [App::DocumentObjectGroupPython] G4_DNA_THYMINE  # scripted group (container) (typed FeaturePython)
  Dunit = g/cm3
  Dvalue = 1
  Group = -> [H_element127,C_element137,N_element057,O_element118]
  conduct = 2
  density = 1
  expand = 3
  formula = G4_DNA_THYMINE
  name = G4_DNA_THYMINE
  specific = 4
FEATURE [App::DocumentObjectGroupPython] H_element128  label="H_element : 075"  # scripted group (container) (typed FeaturePython)
  n = 3
  ref = H_element
FEATURE [App::DocumentObjectGroupPython] C_element138  label="C_element : 083"  # scripted group (container) (typed FeaturePython)
  n = 4
  ref = C_element
FEATURE [App::DocumentObjectGroupPython] N_element058  label="N_element : 030"  # scripted group (container) (typed FeaturePython)
  n = 2
  ref = N_element
FEATURE [App::DocumentObjectGroupPython] O_element119  label="O_element : 072"  # scripted group (container) (typed FeaturePython)
  n = 2
  ref = O_element
FEATURE [App::DocumentObjectGroupPython] G4_DNA_URACIL  # scripted group (container) (typed FeaturePython)
  Dunit = g/cm3
  Dvalue = 1
  Group = -> [H_element128,C_element138,N_element058,O_element119]
  conduct = 2
  density = 1
  expand = 3
  formula = G4_DNA_URACIL
  name = G4_DNA_URACIL
  specific = 4
FEATURE [App::DocumentObjectGroupPython] H_element129  label="H_element : 076"  # scripted group (container) (typed FeaturePython)
  n = 10
  ref = H_element
FEATURE [App::DocumentObjectGroupPython] C_element139  label="C_element : 084"  # scripted group (container) (typed FeaturePython)
  n = 10
  ref = C_element
FEATURE [App::DocumentObjectGroupPython] N_element059  label="N_element : 031"  # scripted group (container) (typed FeaturePython)
  n = 5
  ref = N_element
FEATURE [App::DocumentObjectGroupPython] O_element120  label="O_element : 073"  # scripted group (container) (typed FeaturePython)
  n = 4
  ref = O_element
FEATURE [App::DocumentObjectGroupPython] G4_DNA_ADENOSINE  # scripted group (container) (typed FeaturePython)
  Dunit = g/cm3
  Dvalue = 1
  Group = -> [H_element129,C_element139,N_element059,O_element120]
  conduct = 2
  density = 1
  expand = 3
  formula = G4_DNA_ADENOSINE
  name = G4_DNA_ADENOSINE
  specific = 4
FEATURE [App::DocumentObjectGroupPython] H_element130  label="H_element : 077"  # scripted group (container) (typed FeaturePython)
  n = 10
  ref = H_element
FEATURE [App::DocumentObjectGroupPython] C_element140  label="C_element : 085"  # scripted group (container) (typed FeaturePython)
  n = 10
  ref = C_element
FEATURE [App::DocumentObjectGroupPython] N_element060  label="N_element : 032"  # scripted group (container) (typed FeaturePython)
  n = 5
  ref = N_element
FEATURE [App::DocumentObjectGroupPython] O_element121  label="O_element : 074"  # scripted group (container) (typed FeaturePython)
  n = 5
  ref = O_element
FEATURE [App::DocumentObjectGroupPython] G4_DNA_GUANOSINE  # scripted group (container) (typed FeaturePython)
  Dunit = g/cm3
  Dvalue = 1
  Group = -> [H_element130,C_element140,N_element060,O_element121]
  conduct = 2
  density = 1
  expand = 3
  formula = G4_DNA_GUANOSINE
  name = G4_DNA_GUANOSINE
  specific = 4
FEATURE [App::DocumentObjectGroupPython] H_element131  label="H_element : 078"  # scripted group (container) (typed FeaturePython)
  n = 10
  ref = H_element
FEATURE [App::DocumentObjectGroupPython] C_element141  label="C_element : 086"  # scripted group (container) (typed FeaturePython)
  n = 9
  ref = C_element
FEATURE [App::DocumentObjectGroupPython] N_element061  label="N_element : 033"  # scripted group (container) (typed FeaturePython)
  n = 3
  ref = N_element
FEATURE [App::DocumentObjectGroupPython] O_element122  label="O_element : 075"  # scripted group (container) (typed FeaturePython)
  n = 5
  ref = O_element
FEATURE [App::DocumentObjectGroupPython] G4_DNA_CYTIDINE  # scripted group (container) (typed FeaturePython)
  Dunit = g/cm3
  Dvalue = 1
  Group = -> [H_element131,C_element141,N_element061,O_element122]
  conduct = 2
  density = 1
  expand = 3
  formula = G4_DNA_CYTIDINE
  name = G4_DNA_CYTIDINE
  specific = 4
FEATURE [App::DocumentObjectGroupPython] H_element132  label="H_element : 079"  # scripted group (container) (typed FeaturePython)
  n = 9
  ref = H_element
FEATURE [App::DocumentObjectGroupPython] C_element142  label="C_element : 087"  # scripted group (container) (typed FeaturePython)
  n = 9
  ref = C_element
FEATURE [App::DocumentObjectGroupPython] N_element062  label="N_element : 034"  # scripted group (container) (typed FeaturePython)
  n = 2
  ref = N_element
FEATURE [App::DocumentObjectGroupPython] O_element123  label="O_element : 076"  # scripted group (container) (typed FeaturePython)
  n = 6
  ref = O_element
FEATURE [App::DocumentObjectGroupPython] G4_DNA_URIDINE  # scripted group (container) (typed FeaturePython)
  Dunit = g/cm3
  Dvalue = 1
  Group = -> [H_element132,C_element142,N_element062,O_element123]
  conduct = 2
  density = 1
  expand = 3
  formula = G4_DNA_URIDINE
  name = G4_DNA_URIDINE
  specific = 4
FEATURE [App::DocumentObjectGroupPython] H_element133  label="H_element : 080"  # scripted group (container) (typed FeaturePython)
  n = 11
  ref = H_element
FEATURE [App::DocumentObjectGroupPython] C_element143  label="C_element : 088"  # scripted group (container) (typed FeaturePython)
  n = 10
  ref = C_element
FEATURE [App::DocumentObjectGroupPython] N_element063  label="N_element : 035"  # scripted group (container) (typed FeaturePython)
  n = 2
  ref = N_element
FEATURE [App::DocumentObjectGroupPython] O_element124  label="O_element : 077"  # scripted group (container) (typed FeaturePython)
  n = 6
  ref = O_element
FEATURE [App::DocumentObjectGroupPython] G4_DNA_METHYLURIDINE  # scripted group (container) (typed FeaturePython)
  Dunit = g/cm3
  Dvalue = 1
  Group = -> [H_element133,C_element143,N_element063,O_element124]
  conduct = 2
  density = 1
  expand = 3
  formula = G4_DNA_METHYLURIDINE
  name = G4_DNA_METHYLURIDINE
  specific = 4
FEATURE [App::DocumentObjectGroupPython] P_element014  label="P_element : 003"  # scripted group (container) (typed FeaturePython)
  n = 1
  ref = P_element
FEATURE [App::DocumentObjectGroupPython] O_element125  label="O_element : 078"  # scripted group (container) (typed FeaturePython)
  n = 3
  ref = O_element
FEATURE [App::DocumentObjectGroupPython] G4_DNA_MONOPHOSPHATE  # scripted group (container) (typed FeaturePython)
  Dunit = g/cm3
  Dvalue = 1
  Group = -> [P_element014,O_element125]
  conduct = 2
  density = 1
  expand = 3
  formula = G4_DNA_MONOPHOSPHATE
  name = G4_DNA_MONOPHOSPHATE
  specific = 4
FEATURE [App::DocumentObjectGroupPython] H_element134  label="H_element : 081"  # scripted group (container) (typed FeaturePython)
  n = 10
  ref = H_element
FEATURE [App::DocumentObjectGroupPython] C_element144  label="C_element : 089"  # scripted group (container) (typed FeaturePython)
  n = 10
  ref = C_element
FEATURE [App::DocumentObjectGroupPython] N_element064  label="N_element : 036"  # scripted group (container) (typed FeaturePython)
  n = 5
  ref = N_element
FEATURE [App::DocumentObjectGroupPython] O_element126  label="O_element : 079"  # scripted group (container) (typed FeaturePython)
  n = 7
  ref = O_element
FEATURE [App::DocumentObjectGroupPython] P_element015  label="P_element : 004"  # scripted group (container) (typed FeaturePython)
  n = 1
  ref = P_element
FEATURE [App::DocumentObjectGroupPython] G4_DNA_A  # scripted group (container) (typed FeaturePython)
  Dunit = g/cm3
  Dvalue = 1
  Group = -> [H_element134,C_element144,N_element064,O_element126,P_element015]
  conduct = 2
  density = 1
  expand = 3
  formula = G4_DNA_A
  name = G4_DNA_A
  specific = 4
FEATURE [App::DocumentObjectGroupPython] H_element135  label="H_element : 082"  # scripted group (container) (typed FeaturePython)
  n = 10
  ref = H_element
FEATURE [App::DocumentObjectGroupPython] C_element145  label="C_element : 090"  # scripted group (container) (typed FeaturePython)
  n = 10
  ref = C_element
FEATURE [App::DocumentObjectGroupPython] N_element065  label="N_element : 037"  # scripted group (container) (typed FeaturePython)
  n = 5
  ref = N_element
FEATURE [App::DocumentObjectGroupPython] O_element127  label="O_element : 8"  # scripted group (container) (typed FeaturePython)
  n = 8
  ref = O_element
FEATURE [App::DocumentObjectGroupPython] P_element016  label="P_element : 005"  # scripted group (container) (typed FeaturePython)
  n = 1
  ref = P_element
FEATURE [App::DocumentObjectGroupPython] G4_DNA_G  # scripted group (container) (typed FeaturePython)
  Dunit = g/cm3
  Dvalue = 1
  Group = -> [H_element135,C_element145,N_element065,O_element127,P_element016]
  conduct = 2
  density = 1
  expand = 3
  formula = G4_DNA_G
  name = G4_DNA_G
  specific = 4
FEATURE [App::DocumentObjectGroupPython] H_element136  label="H_element : 083"  # scripted group (container) (typed FeaturePython)
  n = 10
  ref = H_element
FEATURE [App::DocumentObjectGroupPython] C_element146  label="C_element : 091"  # scripted group (container) (typed FeaturePython)
  n = 9
  ref = C_element
FEATURE [App::DocumentObjectGroupPython] N_element066  label="N_element : 038"  # scripted group (container) (typed FeaturePython)
  n = 3
  ref = N_element
FEATURE [App::DocumentObjectGroupPython] O_element128  label="O_element : 080"  # scripted group (container) (typed FeaturePython)
  n = 8
  ref = O_element
FEATURE [App::DocumentObjectGroupPython] P_element017  label="P_element : 006"  # scripted group (container) (typed FeaturePython)
  n = 1
  ref = P_element
FEATURE [App::DocumentObjectGroupPython] G4_DNA_C  # scripted group (container) (typed FeaturePython)
  Dunit = g/cm3
  Dvalue = 1
  Group = -> [H_element136,C_element146,N_element066,O_element128,P_element017]
  conduct = 2
  density = 1
  expand = 3
  formula = G4_DNA_C
  name = G4_DNA_C
  specific = 4
FEATURE [App::DocumentObjectGroupPython] H_element137  label="H_element : 084"  # scripted group (container) (typed FeaturePython)
  n = 9
  ref = H_element
FEATURE [App::DocumentObjectGroupPython] C_element147  label="C_element : 092"  # scripted group (container) (typed FeaturePython)
  n = 9
  ref = C_element
FEATURE [App::DocumentObjectGroupPython] N_element067  label="N_element : 039"  # scripted group (container) (typed FeaturePython)
  n = 2
  ref = N_element
FEATURE [App::DocumentObjectGroupPython] O_element129  label="O_element : 9"  # scripted group (container) (typed FeaturePython)
  n = 9
  ref = O_element
FEATURE [App::DocumentObjectGroupPython] P_element018  label="P_element : 007"  # scripted group (container) (typed FeaturePython)
  n = 1
  ref = P_element
FEATURE [App::DocumentObjectGroupPython] G4_DNA_U  # scripted group (container) (typed FeaturePython)
  Dunit = g/cm3
  Dvalue = 1
  Group = -> [H_element137,C_element147,N_element067,O_element129,P_element018]
  conduct = 2
  density = 1
  expand = 3
  formula = G4_DNA_U
  name = G4_DNA_U
  specific = 4
FEATURE [App::DocumentObjectGroupPython] H_element138  label="H_element : 085"  # scripted group (container) (typed FeaturePython)
  n = 11
  ref = H_element
FEATURE [App::DocumentObjectGroupPython] C_element148  label="C_element : 093"  # scripted group (container) (typed FeaturePython)
  n = 10
  ref = C_element
FEATURE [App::DocumentObjectGroupPython] N_element068  label="N_element : 040"  # scripted group (container) (typed FeaturePython)
  n = 2
  ref = N_element
FEATURE [App::DocumentObjectGroupPython] O_element130  label="O_element : 081"  # scripted group (container) (typed FeaturePython)
  n = 9
  ref = O_element
FEATURE [App::DocumentObjectGroupPython] P_element019  label="P_element : 008"  # scripted group (container) (typed FeaturePython)
  n = 1
  ref = P_element
FEATURE [App::DocumentObjectGroupPython] G4_DNA_MU  # scripted group (container) (typed FeaturePython)
  Dunit = g/cm3
  Dvalue = 1
  Group = -> [H_element138,C_element148,N_element068,O_element130,P_element019]
  conduct = 2
  density = 1
  expand = 3
  formula = G4_DNA_MU
  name = G4_DNA_MU
  specific = 4
FEATURE [App::DocumentObjectGroupPython] BioChemical  # scripted group (container) (typed FeaturePython)
  Group = -> [G4_CYTOSINE,G4_THYMINE,G4_URACIL,G4_DNA_ADENINE,G4_DNA_GUANINE,G4_DNA_CYTOSINE,G4_DNA_THYMINE,G4_DNA_URACIL,G4_DNA_ADENOSINE,G4_DNA_GUANOSINE,G4_DNA_CYTIDINE,G4_DNA_URIDINE,G4_DNA_METHYLURIDINE,G4_DNA_MONOPHOSPHATE,G4_DNA_A,G4_DNA_G,G4_DNA_C,G4_DNA_U,G4_DNA_MU]
FEATURE [App::DocumentObjectGroupPython] G4Materials  # scripted group (container) (typed FeaturePython)
  Group = -> [NIST,Element,HEP,Space,BioChemical]
  version = 1
FEATURE [App::DocumentObjectGroupPython] Geant4  # scripted group (container) (typed FeaturePython)
  Group = -> [G4Isotopes,G4Elements,G4Materials]
FEATURE [App::DocumentObjectGroupPython] Materials  # scripted group (container) (typed FeaturePython)
  Group = -> [Geant4]
FEATURE [Part::FeaturePython] GDMLBox_WorldBox  # WARN: FeaturePython — macro-defined, semantics opaque (R4)
  lunit = 2
  material = 5
  x = 119.6
  y = 117
  z = 31.2
FEATURE [Part::Cone] Cone
  Angle = 360
  AttacherType = Attacher::AttachEngine3D
  Height = 10
  Radius1 = 0
  Radius2 = 5
FEATURE [Part::Vertex] Vertex
  AttacherType = Attacher::AttachEngine3D
  Placement = pos=(0,0,0) rot=(0,0,1;0.349066rad)
  X = 0
  Y = 0
  Z = 0
FEATURE [Part::Vertex] Vertex001
  AttacherType = Attacher::AttachEngine3D
  Placement = pos=(20,20,0) rot=(0,0,1;0rad)
  X = 0
  Y = 0
  Z = 0
FEATURE [Part::Vertex] Vertex002
  AttacherType = Attacher::AttachEngine3D
  Placement = pos=(35,35,0) rot=(0,0,1;0rad)
  X = 0
  Y = 0
  Z = 0
FEATURE [Part::Vertex] Vertex003
  AttacherType = Attacher::AttachEngine3D
  Placement = pos=(40,0,0) rot=(0,0,1;0rad)
  X = 0
  Y = 0
  Z = 0
FEATURE [Part::Vertex] Vertex004
  AttacherType = Attacher::AttachEngine3D
  Placement = pos=(0,40,0) rot=(0,0,1;0rad)
  X = 0
  Y = 0
  Z = 0
FEATURE [Part::Compound] Compound
  Links = -> [Vertex,Vertex001,Vertex002,Vertex003,Vertex004]
FEATURE [Part::FeaturePython] GDMLBox_Box  # WARN: FeaturePython — macro-defined, semantics opaque (R4)
  Placement = pos=(0,0,5) rot=(0,0,1;0rad)
  lunit = 2
  material = 0
  x = 12
  y = 10
  z = 14
FEATURE [Part::Cone] Cone001
  Angle = 360
  AttacherType = Attacher::AttachEngine3D
  Height = 10
  Radius1 = 0
  Radius2 = 5
FEATURE [App::Part] Part001
  Group = -> [Cone001]
  Origin = -> Origin003
FEATURE [App::Part] LV_Box
  Group = -> [GDMLBox_Box,Part001]
  Origin = -> Origin002
FEATURE [Part::FeaturePython] PointArray001  # Draft array (typed FeaturePython)
  Base = -> LV_Box
  Count = 5
  PointObject = -> Compound
FEATURE [App::Part] Part
  Group = -> [Vertex,Cone,Vertex002,Compound,Vertex003,Vertex004,Vertex001,LV_Box,PointArray001]
  Origin = -> Origin001
FEATURE [App::Part] worldVOL
  Group = -> [GDMLBox_WorldBox,Part]
  Origin = -> Origin
